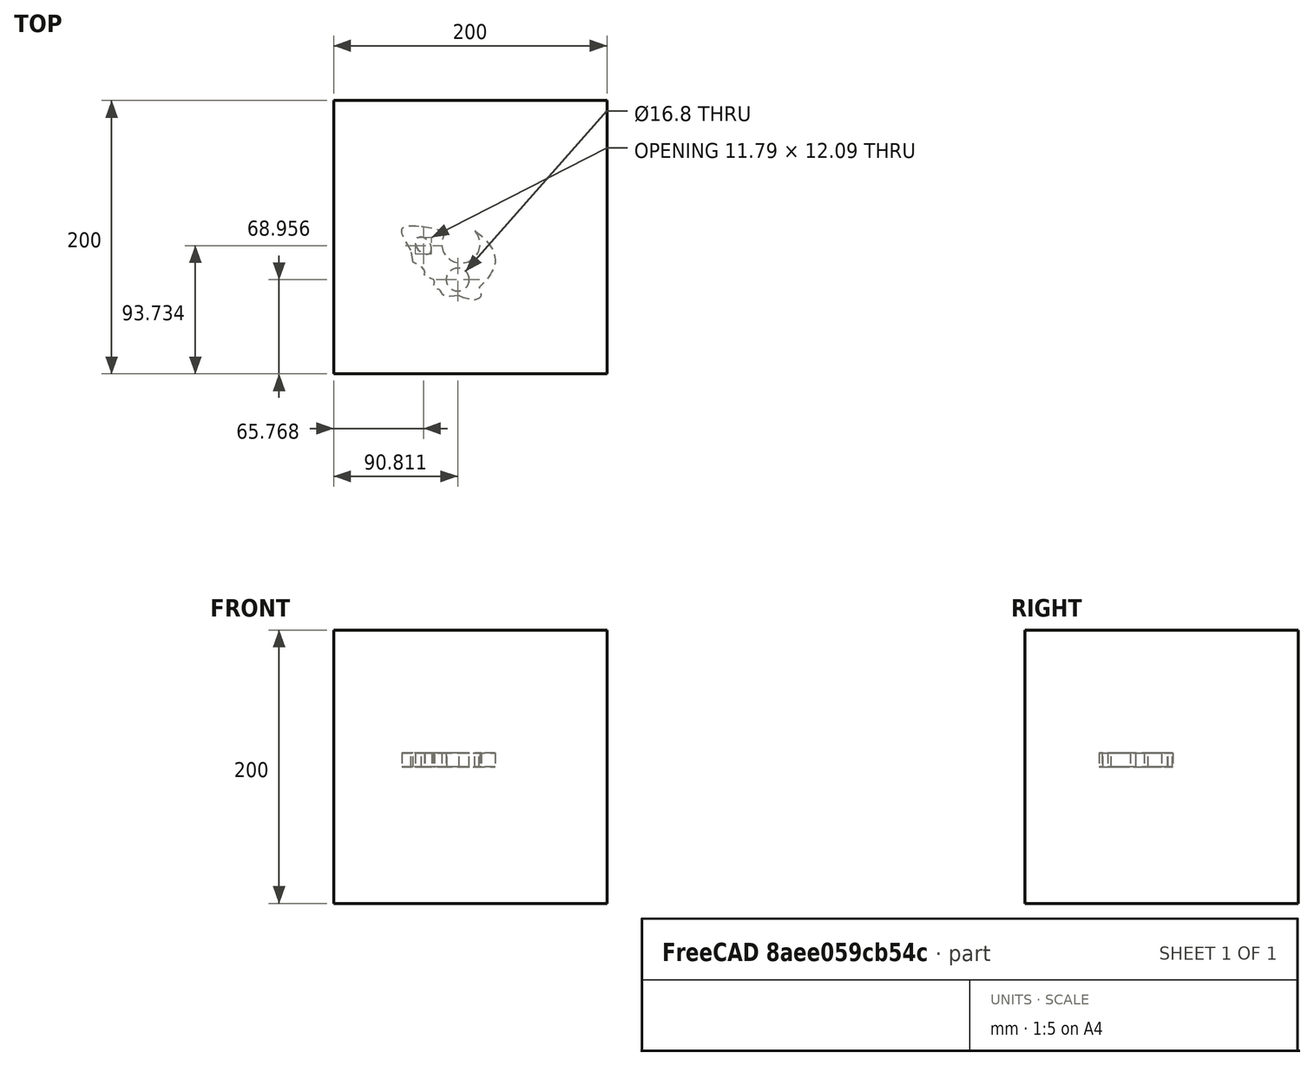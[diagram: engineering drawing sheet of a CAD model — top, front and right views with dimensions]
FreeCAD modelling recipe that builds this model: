
FCSTD DOCUMENT  (FreeCAD 0.21R33694 (Git))
Label: extrudeAllShapes
License: All rights reserved
LicenseURL: http://en.wikipedia.org/wiki/All_rights_reserved
objects: App::DocumentObjectGroupPython×1248, App::Part×2, Part::FeaturePython×1, Sketcher::SketchObject×1, Part::Extrusion×1
note: 3 computed .brp shape members not serialized (recipe doc carries the construction recipe); baked Part::Feature solids carry a one-line shape summary decoded from their .brp

FEATURE [App::DocumentObjectGroupPython] HALFPI  # scripted group (container) (typed FeaturePython)
  name = HALFPI
  value = pi/2.
FEATURE [App::DocumentObjectGroupPython] PI  # scripted group (container) (typed FeaturePython)
  name = PI
  value = 1.*pi
FEATURE [App::DocumentObjectGroupPython] TWOPI  # scripted group (container) (typed FeaturePython)
  name = TWOPI
  value = 2.*pi
FEATURE [App::DocumentObjectGroupPython] Constants  # scripted group (container) (typed FeaturePython)
  Group = -> [HALFPI,PI,TWOPI]
FEATURE [App::DocumentObjectGroupPython] Variables  # scripted group (container) (typed FeaturePython)
FEATURE [App::DocumentObjectGroupPython] Quantities  # scripted group (container) (typed FeaturePython)
FEATURE [App::DocumentObjectGroupPython] Isotopes  # scripted group (container) (typed FeaturePython)
FEATURE [App::DocumentObjectGroupPython] Elements  # scripted group (container) (typed FeaturePython)
FEATURE [App::DocumentObjectGroupPython] G4Isotopes  # scripted group (container) (typed FeaturePython)
FEATURE [App::DocumentObjectGroupPython] H_element  # scripted group (container) (typed FeaturePython)
  Z = 1
  atom_value = 1.008
  formula = H
  name = H_element
FEATURE [App::DocumentObjectGroupPython] He_element  # scripted group (container) (typed FeaturePython)
  Z = 2
  atom_value = 4.0026
  formula = He
  name = He_element
FEATURE [App::DocumentObjectGroupPython] Li_element  # scripted group (container) (typed FeaturePython)
  Z = 3
  atom_value = 6.94
  formula = Li
  name = Li_element
FEATURE [App::DocumentObjectGroupPython] Be_element  # scripted group (container) (typed FeaturePython)
  Z = 4
  atom_value = 9.01218
  formula = Be
  name = Be_element
FEATURE [App::DocumentObjectGroupPython] B_element  # scripted group (container) (typed FeaturePython)
  Z = 5
  atom_value = 10.81
  formula = B
  name = B_element
FEATURE [App::DocumentObjectGroupPython] C_element  # scripted group (container) (typed FeaturePython)
  Z = 6
  atom_value = 12.011
  formula = C
  name = C_element
FEATURE [App::DocumentObjectGroupPython] N_element  # scripted group (container) (typed FeaturePython)
  Z = 7
  atom_value = 14.007
  formula = N
  name = N_element
FEATURE [App::DocumentObjectGroupPython] O_element  # scripted group (container) (typed FeaturePython)
  Z = 8
  atom_value = 15.999
  formula = O
  name = O_element
FEATURE [App::DocumentObjectGroupPython] F_element  # scripted group (container) (typed FeaturePython)
  Z = 9
  atom_value = 18.9984
  formula = F
  name = F_element
FEATURE [App::DocumentObjectGroupPython] Ne_element  # scripted group (container) (typed FeaturePython)
  Z = 10
  atom_value = 20.1797
  formula = Ne
  name = Ne_element
FEATURE [App::DocumentObjectGroupPython] Na_element  # scripted group (container) (typed FeaturePython)
  Z = 11
  atom_value = 22.9898
  formula = Na
  name = Na_element
FEATURE [App::DocumentObjectGroupPython] Mg_element  # scripted group (container) (typed FeaturePython)
  Z = 12
  atom_value = 24.305
  formula = Mg
  name = Mg_element
FEATURE [App::DocumentObjectGroupPython] Al_element  # scripted group (container) (typed FeaturePython)
  Z = 13
  atom_value = 26.9815
  formula = Al
  name = Al_element
FEATURE [App::DocumentObjectGroupPython] Si_element  # scripted group (container) (typed FeaturePython)
  Z = 14
  atom_value = 28.085
  formula = Si
  name = Si_element
FEATURE [App::DocumentObjectGroupPython] P_element  # scripted group (container) (typed FeaturePython)
  Z = 15
  atom_value = 30.9738
  formula = P
  name = P_element
FEATURE [App::DocumentObjectGroupPython] S_element  # scripted group (container) (typed FeaturePython)
  Z = 16
  atom_value = 32.06
  formula = S
  name = S_element
FEATURE [App::DocumentObjectGroupPython] Cl_element  # scripted group (container) (typed FeaturePython)
  Z = 17
  atom_value = 35.45
  formula = Cl
  name = Cl_element
FEATURE [App::DocumentObjectGroupPython] Ar_element  # scripted group (container) (typed FeaturePython)
  Z = 18
  atom_value = 39.95
  formula = Ar
  name = Ar_element
FEATURE [App::DocumentObjectGroupPython] K_element  # scripted group (container) (typed FeaturePython)
  Z = 19
  atom_value = 39.0983
  formula = K
  name = K_element
FEATURE [App::DocumentObjectGroupPython] Ca_element  # scripted group (container) (typed FeaturePython)
  Z = 20
  atom_value = 40.078
  formula = Ca
  name = Ca_element
FEATURE [App::DocumentObjectGroupPython] Sc_element  # scripted group (container) (typed FeaturePython)
  Z = 21
  atom_value = 44.9559
  formula = Sc
  name = Sc_element
FEATURE [App::DocumentObjectGroupPython] Ti_element  # scripted group (container) (typed FeaturePython)
  Z = 22
  atom_value = 47.867
  formula = Ti
  name = Ti_element
FEATURE [App::DocumentObjectGroupPython] V_element  # scripted group (container) (typed FeaturePython)
  Z = 23
  atom_value = 50.9415
  formula = V
  name = V_element
FEATURE [App::DocumentObjectGroupPython] Cr_element  # scripted group (container) (typed FeaturePython)
  Z = 24
  atom_value = 51.9961
  formula = Cr
  name = Cr_element
FEATURE [App::DocumentObjectGroupPython] Mn_element  # scripted group (container) (typed FeaturePython)
  Z = 25
  atom_value = 54.938
  formula = Mn
  name = Mn_element
FEATURE [App::DocumentObjectGroupPython] Fe_element  # scripted group (container) (typed FeaturePython)
  Z = 26
  atom_value = 55.845
  formula = Fe
  name = Fe_element
FEATURE [App::DocumentObjectGroupPython] Co_element  # scripted group (container) (typed FeaturePython)
  Z = 27
  atom_value = 58.9332
  formula = Co
  name = Co_element
FEATURE [App::DocumentObjectGroupPython] Ni_element  # scripted group (container) (typed FeaturePython)
  Z = 28
  atom_value = 58.6934
  formula = Ni
  name = Ni_element
FEATURE [App::DocumentObjectGroupPython] Cu_element  # scripted group (container) (typed FeaturePython)
  Z = 29
  atom_value = 63.546
  formula = Cu
  name = Cu_element
FEATURE [App::DocumentObjectGroupPython] Zn_element  # scripted group (container) (typed FeaturePython)
  Z = 30
  atom_value = 65.38
  formula = Zn
  name = Zn_element
FEATURE [App::DocumentObjectGroupPython] Ga_element  # scripted group (container) (typed FeaturePython)
  Z = 31
  atom_value = 69.723
  formula = Ga
  name = Ga_element
FEATURE [App::DocumentObjectGroupPython] Ge_element  # scripted group (container) (typed FeaturePython)
  Z = 32
  atom_value = 72.63
  formula = Ge
  name = Ge_element
FEATURE [App::DocumentObjectGroupPython] As_element  # scripted group (container) (typed FeaturePython)
  Z = 33
  atom_value = 74.9216
  formula = As
  name = As_element
FEATURE [App::DocumentObjectGroupPython] Se_element  # scripted group (container) (typed FeaturePython)
  Z = 34
  atom_value = 78.971
  formula = Se
  name = Se_element
FEATURE [App::DocumentObjectGroupPython] Br_element  # scripted group (container) (typed FeaturePython)
  Z = 35
  atom_value = 79.904
  formula = Br
  name = Br_element
FEATURE [App::DocumentObjectGroupPython] Kr_element  # scripted group (container) (typed FeaturePython)
  Z = 36
  atom_value = 83.798
  formula = Kr
  name = Kr_element
FEATURE [App::DocumentObjectGroupPython] Rb_element  # scripted group (container) (typed FeaturePython)
  Z = 37
  atom_value = 85.4678
  formula = Rb
  name = Rb_element
FEATURE [App::DocumentObjectGroupPython] Sr_element  # scripted group (container) (typed FeaturePython)
  Z = 38
  atom_value = 87.62
  formula = Sr
  name = Sr_element
FEATURE [App::DocumentObjectGroupPython] Y_element  # scripted group (container) (typed FeaturePython)
  Z = 39
  atom_value = 88.9058
  formula = Y
  name = Y_element
FEATURE [App::DocumentObjectGroupPython] Zr_element  # scripted group (container) (typed FeaturePython)
  Z = 40
  atom_value = 91.224
  formula = Zr
  name = Zr_element
FEATURE [App::DocumentObjectGroupPython] Nb_element  # scripted group (container) (typed FeaturePython)
  Z = 41
  atom_value = 92.9064
  formula = Nb
  name = Nb_element
FEATURE [App::DocumentObjectGroupPython] Mo_element  # scripted group (container) (typed FeaturePython)
  Z = 42
  atom_value = 95.95
  formula = Mo
  name = Mo_element
FEATURE [App::DocumentObjectGroupPython] Tc_element  # scripted group (container) (typed FeaturePython)
  Z = 43
  atom_value = 97
  formula = Tc
  name = Tc_element
FEATURE [App::DocumentObjectGroupPython] Ru_element  # scripted group (container) (typed FeaturePython)
  Z = 44
  atom_value = 101.07
  formula = Ru
  name = Ru_element
FEATURE [App::DocumentObjectGroupPython] Rh_element  # scripted group (container) (typed FeaturePython)
  Z = 45
  atom_value = 102.905
  formula = Rh
  name = Rh_element
FEATURE [App::DocumentObjectGroupPython] Pd_element  # scripted group (container) (typed FeaturePython)
  Z = 46
  atom_value = 106.42
  formula = Pd
  name = Pd_element
FEATURE [App::DocumentObjectGroupPython] Ag_element  # scripted group (container) (typed FeaturePython)
  Z = 47
  atom_value = 107.868
  formula = Ag
  name = Ag_element
FEATURE [App::DocumentObjectGroupPython] Cd_element  # scripted group (container) (typed FeaturePython)
  Z = 48
  atom_value = 112.414
  formula = Cd
  name = Cd_element
FEATURE [App::DocumentObjectGroupPython] In_element  # scripted group (container) (typed FeaturePython)
  Z = 49
  atom_value = 114.818
  formula = In
  name = In_element
FEATURE [App::DocumentObjectGroupPython] Sn_element  # scripted group (container) (typed FeaturePython)
  Z = 50
  atom_value = 118.71
  formula = Sn
  name = Sn_element
FEATURE [App::DocumentObjectGroupPython] Sb_element  # scripted group (container) (typed FeaturePython)
  Z = 51
  atom_value = 121.76
  formula = Sb
  name = Sb_element
FEATURE [App::DocumentObjectGroupPython] Te_element  # scripted group (container) (typed FeaturePython)
  Z = 52
  atom_value = 127.6
  formula = Te
  name = Te_element
FEATURE [App::DocumentObjectGroupPython] I_element  # scripted group (container) (typed FeaturePython)
  Z = 53
  atom_value = 126.904
  formula = I
  name = I_element
FEATURE [App::DocumentObjectGroupPython] Xe_element  # scripted group (container) (typed FeaturePython)
  Z = 54
  atom_value = 131.293
  formula = Xe
  name = Xe_element
FEATURE [App::DocumentObjectGroupPython] Cs_element  # scripted group (container) (typed FeaturePython)
  Z = 55
  atom_value = 132.905
  formula = Cs
  name = Cs_element
FEATURE [App::DocumentObjectGroupPython] Ba_element  # scripted group (container) (typed FeaturePython)
  Z = 56
  atom_value = 137.327
  formula = Ba
  name = Ba_element
FEATURE [App::DocumentObjectGroupPython] La_element  # scripted group (container) (typed FeaturePython)
  Z = 57
  atom_value = 138.905
  formula = La
  name = La_element
FEATURE [App::DocumentObjectGroupPython] Ce_element  # scripted group (container) (typed FeaturePython)
  Z = 58
  atom_value = 140.116
  formula = Ce
  name = Ce_element
FEATURE [App::DocumentObjectGroupPython] Pr_element  # scripted group (container) (typed FeaturePython)
  Z = 59
  atom_value = 140.908
  formula = Pr
  name = Pr_element
FEATURE [App::DocumentObjectGroupPython] Nd_element  # scripted group (container) (typed FeaturePython)
  Z = 60
  atom_value = 144.242
  formula = Nd
  name = Nd_element
FEATURE [App::DocumentObjectGroupPython] Pm_element  # scripted group (container) (typed FeaturePython)
  Z = 61
  atom_value = 145
  formula = Pm
  name = Pm_element
FEATURE [App::DocumentObjectGroupPython] Sm_element  # scripted group (container) (typed FeaturePython)
  Z = 62
  atom_value = 150.36
  formula = Sm
  name = Sm_element
FEATURE [App::DocumentObjectGroupPython] Eu_element  # scripted group (container) (typed FeaturePython)
  Z = 63
  atom_value = 151.964
  formula = Eu
  name = Eu_element
FEATURE [App::DocumentObjectGroupPython] Gd_element  # scripted group (container) (typed FeaturePython)
  Z = 64
  atom_value = 157.25
  formula = Gd
  name = Gd_element
FEATURE [App::DocumentObjectGroupPython] Tb_element  # scripted group (container) (typed FeaturePython)
  Z = 65
  atom_value = 158.925
  formula = Tb
  name = Tb_element
FEATURE [App::DocumentObjectGroupPython] Dy_element  # scripted group (container) (typed FeaturePython)
  Z = 66
  atom_value = 162.5
  formula = Dy
  name = Dy_element
FEATURE [App::DocumentObjectGroupPython] Ho_element  # scripted group (container) (typed FeaturePython)
  Z = 67
  atom_value = 164.93
  formula = Ho
  name = Ho_element
FEATURE [App::DocumentObjectGroupPython] Er_element  # scripted group (container) (typed FeaturePython)
  Z = 68
  atom_value = 167.259
  formula = Er
  name = Er_element
FEATURE [App::DocumentObjectGroupPython] Tm_element  # scripted group (container) (typed FeaturePython)
  Z = 69
  atom_value = 168.934
  formula = Tm
  name = Tm_element
FEATURE [App::DocumentObjectGroupPython] Yb_element  # scripted group (container) (typed FeaturePython)
  Z = 70
  atom_value = 173.045
  formula = Yb
  name = Yb_element
FEATURE [App::DocumentObjectGroupPython] Lu_element  # scripted group (container) (typed FeaturePython)
  Z = 71
  atom_value = 174.967
  formula = Lu
  name = Lu_element
FEATURE [App::DocumentObjectGroupPython] Hf_element  # scripted group (container) (typed FeaturePython)
  Z = 72
  atom_value = 178.49
  formula = Hf
  name = Hf_element
FEATURE [App::DocumentObjectGroupPython] Ta_element  # scripted group (container) (typed FeaturePython)
  Z = 73
  atom_value = 180.948
  formula = Ta
  name = Ta_element
FEATURE [App::DocumentObjectGroupPython] W_element  # scripted group (container) (typed FeaturePython)
  Z = 74
  atom_value = 183.84
  formula = W
  name = W_element
FEATURE [App::DocumentObjectGroupPython] Re_element  # scripted group (container) (typed FeaturePython)
  Z = 75
  atom_value = 186.207
  formula = Re
  name = Re_element
FEATURE [App::DocumentObjectGroupPython] Os_element  # scripted group (container) (typed FeaturePython)
  Z = 76
  atom_value = 190.23
  formula = Os
  name = Os_element
FEATURE [App::DocumentObjectGroupPython] Ir_element  # scripted group (container) (typed FeaturePython)
  Z = 77
  atom_value = 192.217
  formula = Ir
  name = Ir_element
FEATURE [App::DocumentObjectGroupPython] Pt_element  # scripted group (container) (typed FeaturePython)
  Z = 78
  atom_value = 195.084
  formula = Pt
  name = Pt_element
FEATURE [App::DocumentObjectGroupPython] Au_element  # scripted group (container) (typed FeaturePython)
  Z = 79
  atom_value = 196.967
  formula = Au
  name = Au_element
FEATURE [App::DocumentObjectGroupPython] Hg_element  # scripted group (container) (typed FeaturePython)
  Z = 80
  atom_value = 200.592
  formula = Hg
  name = Hg_element
FEATURE [App::DocumentObjectGroupPython] Tl_element  # scripted group (container) (typed FeaturePython)
  Z = 81
  atom_value = 204.38
  formula = Tl
  name = Tl_element
FEATURE [App::DocumentObjectGroupPython] Pb_element  # scripted group (container) (typed FeaturePython)
  Z = 82
  atom_value = 207.2
  formula = Pb
  name = Pb_element
FEATURE [App::DocumentObjectGroupPython] Bi_element  # scripted group (container) (typed FeaturePython)
  Z = 83
  atom_value = 208.98
  formula = Bi
  name = Bi_element
FEATURE [App::DocumentObjectGroupPython] Po_element  # scripted group (container) (typed FeaturePython)
  Z = 84
  atom_value = 209
  formula = Po
  name = Po_element
FEATURE [App::DocumentObjectGroupPython] At_element  # scripted group (container) (typed FeaturePython)
  Z = 85
  atom_value = 210
  formula = At
  name = At_element
FEATURE [App::DocumentObjectGroupPython] Rn_element  # scripted group (container) (typed FeaturePython)
  Z = 86
  atom_value = 222
  formula = Rn
  name = Rn_element
FEATURE [App::DocumentObjectGroupPython] Fr_element  # scripted group (container) (typed FeaturePython)
  Z = 87
  atom_value = 223
  formula = Fr
  name = Fr_element
FEATURE [App::DocumentObjectGroupPython] Ra_element  # scripted group (container) (typed FeaturePython)
  Z = 88
  atom_value = 226
  formula = Ra
  name = Ra_element
FEATURE [App::DocumentObjectGroupPython] Ac_element  # scripted group (container) (typed FeaturePython)
  Z = 89
  atom_value = 227
  formula = Ac
  name = Ac_element
FEATURE [App::DocumentObjectGroupPython] Th_element  # scripted group (container) (typed FeaturePython)
  Z = 90
  atom_value = 232.038
  formula = Th
  name = Th_element
FEATURE [App::DocumentObjectGroupPython] Pa_element  # scripted group (container) (typed FeaturePython)
  Z = 91
  atom_value = 231.036
  formula = Pa
  name = Pa_element
FEATURE [App::DocumentObjectGroupPython] U_element  # scripted group (container) (typed FeaturePython)
  Z = 92
  atom_value = 238.029
  formula = U
  name = U_element
FEATURE [App::DocumentObjectGroupPython] Np_element  # scripted group (container) (typed FeaturePython)
  Z = 93
  atom_value = 237
  formula = Np
  name = Np_element
FEATURE [App::DocumentObjectGroupPython] Pu_element  # scripted group (container) (typed FeaturePython)
  Z = 94
  atom_value = 244
  formula = Pu
  name = Pu_element
FEATURE [App::DocumentObjectGroupPython] Am_element  # scripted group (container) (typed FeaturePython)
  Z = 95
  atom_value = 243
  formula = Am
  name = Am_element
FEATURE [App::DocumentObjectGroupPython] Cm_element  # scripted group (container) (typed FeaturePython)
  Z = 96
  atom_value = 247
  formula = Cm
  name = Cm_element
FEATURE [App::DocumentObjectGroupPython] Bk_element  # scripted group (container) (typed FeaturePython)
  Z = 97
  atom_value = 247
  formula = Bk
  name = Bk_element
FEATURE [App::DocumentObjectGroupPython] Cf_element  # scripted group (container) (typed FeaturePython)
  Z = 98
  atom_value = 251
  formula = Cf
  name = Cf_element
FEATURE [App::DocumentObjectGroupPython] G4Elements  # scripted group (container) (typed FeaturePython)
  Group = -> [H_element,He_element,Li_element,Be_element,B_element,C_element,N_element,O_element,F_element,Ne_element,Na_element,Mg_element,Al_element,Si_element,P_element,S_element,Cl_element,Ar_element,K_element,Ca_element,Sc_element,Ti_element,V_element,Cr_element,Mn_element,Fe_element,Co_element,Ni_element,Cu_element,Zn_element,Ga_element,Ge_element,As_element,Se_element,Br_element,Kr_element,Rb_element,+61 more]
FEATURE [App::DocumentObjectGroupPython] H_element001  label="H_element : 0.101"  # scripted group (container) (typed FeaturePython)
  n = 0.101327
FEATURE [App::DocumentObjectGroupPython] C_element001  label="C_element : 0.775"  # scripted group (container) (typed FeaturePython)
  n = 0.7755
FEATURE [App::DocumentObjectGroupPython] N_element001  label="N_element : 0.035"  # scripted group (container) (typed FeaturePython)
  n = 0.035057
FEATURE [App::DocumentObjectGroupPython] O_element001  label="O_element : 0.052"  # scripted group (container) (typed FeaturePython)
  n = 0.0523159
FEATURE [App::DocumentObjectGroupPython] F_element001  label="F_element : 0.017"  # scripted group (container) (typed FeaturePython)
  n = 0.017422
FEATURE [App::DocumentObjectGroupPython] Ca_element001  label="Ca_element : 0.018"  # scripted group (container) (typed FeaturePython)
  n = 0.018378
FEATURE [App::DocumentObjectGroupPython] G4_A_150_TISSUE  label="G4_A-150_TISSUE"  # scripted group (container) (typed FeaturePython)
  Dunit = g/cm3
  Dvalue = 1.127
  Group = -> [H_element001,C_element001,N_element001,O_element001,F_element001,Ca_element001]
  conduct = 2
  density = 1
  expand = 3
  formula = G4_A-150_TISSUE
  name = G4_A-150_TISSUE
  specific = 4
FEATURE [App::DocumentObjectGroupPython] C_element002  label="C_element : 3"  # scripted group (container) (typed FeaturePython)
  n = 3
  ref = C_element
FEATURE [App::DocumentObjectGroupPython] H_element002  label="H_element : 6"  # scripted group (container) (typed FeaturePython)
  n = 6
  ref = H_element
FEATURE [App::DocumentObjectGroupPython] O_element002  label="O_element : 1"  # scripted group (container) (typed FeaturePython)
  n = 1
  ref = O_element
FEATURE [App::DocumentObjectGroupPython] G4_ACETONE  # scripted group (container) (typed FeaturePython)
  Dunit = g/cm3
  Dvalue = 0.7899
  Group = -> [C_element002,H_element002,O_element002]
  conduct = 2
  density = 1
  expand = 3
  formula = G4_ACETONE
  name = G4_ACETONE
  specific = 4
FEATURE [App::DocumentObjectGroupPython] C_element003  label="C_element : 2"  # scripted group (container) (typed FeaturePython)
  n = 2
  ref = C_element
FEATURE [App::DocumentObjectGroupPython] H_element003  label="H_element : 2"  # scripted group (container) (typed FeaturePython)
  n = 2
  ref = H_element
FEATURE [App::DocumentObjectGroupPython] G4_ACETYLENE  # scripted group (container) (typed FeaturePython)
  Dunit = g/cm3
  Dvalue = 0.0010967
  Group = -> [C_element003,H_element003]
  conduct = 2
  density = 1
  expand = 3
  formula = G4_ACETYLENE
  name = G4_ACETYLENE
  specific = 4
FEATURE [App::DocumentObjectGroupPython] C_element004  label="C_element : 5"  # scripted group (container) (typed FeaturePython)
  n = 5
  ref = C_element
FEATURE [App::DocumentObjectGroupPython] H_element004  label="H_element : 5"  # scripted group (container) (typed FeaturePython)
  n = 5
  ref = H_element
FEATURE [App::DocumentObjectGroupPython] N_element002  label="N_element : 5"  # scripted group (container) (typed FeaturePython)
  n = 5
  ref = N_element
FEATURE [App::DocumentObjectGroupPython] G4_ADENINE  # scripted group (container) (typed FeaturePython)
  Dunit = g/cm3
  Dvalue = 1.6
  Group = -> [C_element004,H_element004,N_element002]
  conduct = 2
  density = 1
  expand = 3
  formula = G4_ADENINE
  name = G4_ADENINE
  specific = 4
FEATURE [App::DocumentObjectGroupPython] H_element005  label="H_element : 0.114"  # scripted group (container) (typed FeaturePython)
  n = 0.114
FEATURE [App::DocumentObjectGroupPython] C_element005  label="C_element : 0.598"  # scripted group (container) (typed FeaturePython)
  n = 0.598
FEATURE [App::DocumentObjectGroupPython] N_element003  label="N_element : 0.007"  # scripted group (container) (typed FeaturePython)
  n = 0.007
FEATURE [App::DocumentObjectGroupPython] O_element003  label="O_element : 0.278"  # scripted group (container) (typed FeaturePython)
  n = 0.278
FEATURE [App::DocumentObjectGroupPython] Na_element001  label="Na_element : 0.001"  # scripted group (container) (typed FeaturePython)
  n = 0.001
FEATURE [App::DocumentObjectGroupPython] S_element001  label="S_element : 0.001"  # scripted group (container) (typed FeaturePython)
  n = 0.001
FEATURE [App::DocumentObjectGroupPython] Cl_element001  label="Cl_element : 0.001"  # scripted group (container) (typed FeaturePython)
  n = 0.001
FEATURE [App::DocumentObjectGroupPython] G4_ADIPOSE_TISSUE_ICRP  # scripted group (container) (typed FeaturePython)
  Dunit = g/cm3
  Dvalue = 0.95
  Group = -> [H_element005,C_element005,N_element003,O_element003,Na_element001,S_element001,Cl_element001]
  conduct = 2
  density = 1
  expand = 3
  formula = G4_ADIPOSE_TISSUE_ICRP
  name = G4_ADIPOSE_TISSUE_ICRP
  specific = 4
FEATURE [App::DocumentObjectGroupPython] C_element006  label="C_element : 0.000"  # scripted group (container) (typed FeaturePython)
  n = 0.000124
FEATURE [App::DocumentObjectGroupPython] N_element004  label="N_element : 0.755"  # scripted group (container) (typed FeaturePython)
  n = 0.755268
FEATURE [App::DocumentObjectGroupPython] O_element004  label="O_element : 0.232"  # scripted group (container) (typed FeaturePython)
  n = 0.231781
FEATURE [App::DocumentObjectGroupPython] Ar_element001  label="Ar_element : 0.013"  # scripted group (container) (typed FeaturePython)
  n = 0.012827
FEATURE [App::DocumentObjectGroupPython] G4_AIR  # scripted group (container) (typed FeaturePython)
  Dunit = g/cm3
  Dvalue = 0.00120479
  Group = -> [C_element006,N_element004,O_element004,Ar_element001]
  conduct = 2
  density = 1
  expand = 3
  formula = G4_AIR
  name = G4_AIR
  specific = 4
FEATURE [App::DocumentObjectGroupPython] C_element007  label="C_element : 006"  # scripted group (container) (typed FeaturePython)
  n = 3
  ref = C_element
FEATURE [App::DocumentObjectGroupPython] H_element006  label="H_element : 7"  # scripted group (container) (typed FeaturePython)
  n = 7
  ref = H_element
FEATURE [App::DocumentObjectGroupPython] N_element005  label="N_element : 1"  # scripted group (container) (typed FeaturePython)
  n = 1
  ref = N_element
FEATURE [App::DocumentObjectGroupPython] O_element005  label="O_element : 2"  # scripted group (container) (typed FeaturePython)
  n = 2
  ref = O_element
FEATURE [App::DocumentObjectGroupPython] G4_ALANINE  # scripted group (container) (typed FeaturePython)
  Dunit = g/cm3
  Dvalue = 1.42
  Group = -> [C_element007,H_element006,N_element005,O_element005]
  conduct = 2
  density = 1
  expand = 3
  formula = G4_ALANINE
  name = G4_ALANINE
  specific = 4
FEATURE [App::DocumentObjectGroupPython] Al_element001  label="Al_element : 2"  # scripted group (container) (typed FeaturePython)
  n = 2
  ref = Al_element
FEATURE [App::DocumentObjectGroupPython] O_element006  label="O_element : 3"  # scripted group (container) (typed FeaturePython)
  n = 3
  ref = O_element
FEATURE [App::DocumentObjectGroupPython] G4_ALUMINUM_OXIDE  # scripted group (container) (typed FeaturePython)
  Dunit = g/cm3
  Dvalue = 3.97
  Group = -> [Al_element001,O_element006]
  conduct = 2
  density = 1
  expand = 3
  formula = G4_ALUMINUM_OXIDE
  name = G4_ALUMINUM_OXIDE
  specific = 4
FEATURE [App::DocumentObjectGroupPython] H_element007  label="H_element : 0.106"  # scripted group (container) (typed FeaturePython)
  n = 0.10593
FEATURE [App::DocumentObjectGroupPython] C_element008  label="C_element : 0.789"  # scripted group (container) (typed FeaturePython)
  n = 0.788974
FEATURE [App::DocumentObjectGroupPython] O_element007  label="O_element : 0.105"  # scripted group (container) (typed FeaturePython)
  n = 0.105096
FEATURE [App::DocumentObjectGroupPython] G4_AMBER  # scripted group (container) (typed FeaturePython)
  Dunit = g/cm3
  Dvalue = 1.1
  Group = -> [H_element007,C_element008,O_element007]
  conduct = 2
  density = 1
  expand = 3
  formula = G4_AMBER
  name = G4_AMBER
  specific = 4
FEATURE [App::DocumentObjectGroupPython] N_element006  label="N_element : 006"  # scripted group (container) (typed FeaturePython)
  n = 1
  ref = N_element
FEATURE [App::DocumentObjectGroupPython] H_element008  label="H_element : 3"  # scripted group (container) (typed FeaturePython)
  n = 3
  ref = H_element
FEATURE [App::DocumentObjectGroupPython] G4_AMMONIA  # scripted group (container) (typed FeaturePython)
  Dunit = g/cm3
  Dvalue = 0.000826019
  Group = -> [N_element006,H_element008]
  conduct = 2
  density = 1
  expand = 3
  formula = G4_AMMONIA
  name = G4_AMMONIA
  specific = 4
FEATURE [App::DocumentObjectGroupPython] C_element009  label="C_element : 6"  # scripted group (container) (typed FeaturePython)
  n = 6
  ref = C_element
FEATURE [App::DocumentObjectGroupPython] H_element009  label="H_element : 008"  # scripted group (container) (typed FeaturePython)
  n = 7
  ref = H_element
FEATURE [App::DocumentObjectGroupPython] N_element007  label="N_element : 007"  # scripted group (container) (typed FeaturePython)
  n = 1
  ref = N_element
FEATURE [App::DocumentObjectGroupPython] G4_ANILINE  # scripted group (container) (typed FeaturePython)
  Dunit = g/cm3
  Dvalue = 1.0235
  Group = -> [C_element009,H_element009,N_element007]
  conduct = 2
  density = 1
  expand = 3
  formula = G4_ANILINE
  name = G4_ANILINE
  specific = 4
FEATURE [App::DocumentObjectGroupPython] C_element010  label="C_element : 14"  # scripted group (container) (typed FeaturePython)
  n = 14
  ref = C_element
FEATURE [App::DocumentObjectGroupPython] H_element010  label="H_element : 10"  # scripted group (container) (typed FeaturePython)
  n = 10
  ref = H_element
FEATURE [App::DocumentObjectGroupPython] G4_ANTHRACENE  # scripted group (container) (typed FeaturePython)
  Dunit = g/cm3
  Dvalue = 1.283
  Group = -> [C_element010,H_element010]
  conduct = 2
  density = 1
  expand = 3
  formula = G4_ANTHRACENE
  name = G4_ANTHRACENE
  specific = 4
FEATURE [App::DocumentObjectGroupPython] H_element011  label="H_element : 0.065"  # scripted group (container) (typed FeaturePython)
  n = 0.0654709
FEATURE [App::DocumentObjectGroupPython] C_element011  label="C_element : 0.537"  # scripted group (container) (typed FeaturePython)
  n = 0.536944
FEATURE [App::DocumentObjectGroupPython] N_element008  label="N_element : 0.021"  # scripted group (container) (typed FeaturePython)
  n = 0.0215
FEATURE [App::DocumentObjectGroupPython] O_element008  label="O_element : 0.032"  # scripted group (container) (typed FeaturePython)
  n = 0.032085
FEATURE [App::DocumentObjectGroupPython] F_element002  label="F_element : 0.167"  # scripted group (container) (typed FeaturePython)
  n = 0.167411
FEATURE [App::DocumentObjectGroupPython] Ca_element002  label="Ca_element : 0.177"  # scripted group (container) (typed FeaturePython)
  n = 0.176589
FEATURE [App::DocumentObjectGroupPython] G4_B_100_BONE  label="G4_B-100_BONE"  # scripted group (container) (typed FeaturePython)
  Dunit = g/cm3
  Dvalue = 1.45
  Group = -> [H_element011,C_element011,N_element008,O_element008,F_element002,Ca_element002]
  conduct = 2
  density = 1
  expand = 3
  formula = G4_B-100_BONE
  name = G4_B-100_BONE
  specific = 4
FEATURE [App::DocumentObjectGroupPython] H_element012  label="H_element : 0.057"  # scripted group (container) (typed FeaturePython)
  n = 0.057441
FEATURE [App::DocumentObjectGroupPython] C_element012  label="C_element : 0.790"  # scripted group (container) (typed FeaturePython)
  n = 0.774591
FEATURE [App::DocumentObjectGroupPython] O_element009  label="O_element : 0.168"  # scripted group (container) (typed FeaturePython)
  n = 0.167968
FEATURE [App::DocumentObjectGroupPython] G4_BAKELITE  # scripted group (container) (typed FeaturePython)
  Dunit = g/cm3
  Dvalue = 1.25
  Group = -> [H_element012,C_element012,O_element009]
  conduct = 2
  density = 1
  expand = 3
  formula = G4_BAKELITE
  name = G4_BAKELITE
  specific = 4
FEATURE [App::DocumentObjectGroupPython] Ba_element001  label="Ba_element : 1"  # scripted group (container) (typed FeaturePython)
  n = 1
  ref = Ba_element
FEATURE [App::DocumentObjectGroupPython] F_element003  label="F_element : 2"  # scripted group (container) (typed FeaturePython)
  n = 2
  ref = F_element
FEATURE [App::DocumentObjectGroupPython] G4_BARIUM_FLUORIDE  # scripted group (container) (typed FeaturePython)
  Dunit = g/cm3
  Dvalue = 4.89
  Group = -> [Ba_element001,F_element003]
  conduct = 2
  density = 1
  expand = 3
  formula = G4_BARIUM_FLUORIDE
  name = G4_BARIUM_FLUORIDE
  specific = 4
FEATURE [App::DocumentObjectGroupPython] Ba_element002  label="Ba_element : 002"  # scripted group (container) (typed FeaturePython)
  n = 1
  ref = Ba_element
FEATURE [App::DocumentObjectGroupPython] S_element002  label="S_element : 1"  # scripted group (container) (typed FeaturePython)
  n = 1
  ref = S_element
FEATURE [App::DocumentObjectGroupPython] O_element010  label="O_element : 4"  # scripted group (container) (typed FeaturePython)
  n = 4
  ref = O_element
FEATURE [App::DocumentObjectGroupPython] G4_BARIUM_SULFATE  # scripted group (container) (typed FeaturePython)
  Dunit = g/cm3
  Dvalue = 4.5
  Group = -> [Ba_element002,S_element002,O_element010]
  conduct = 2
  density = 1
  expand = 3
  formula = G4_BARIUM_SULFATE
  name = G4_BARIUM_SULFATE
  specific = 4
FEATURE [App::DocumentObjectGroupPython] C_element013  label="C_element : 007"  # scripted group (container) (typed FeaturePython)
  n = 6
  ref = C_element
FEATURE [App::DocumentObjectGroupPython] H_element013  label="H_element : 009"  # scripted group (container) (typed FeaturePython)
  n = 6
  ref = H_element
FEATURE [App::DocumentObjectGroupPython] G4_BENZENE  # scripted group (container) (typed FeaturePython)
  Dunit = g/cm3
  Dvalue = 0.87865
  Group = -> [C_element013,H_element013]
  conduct = 2
  density = 1
  expand = 3
  formula = G4_BENZENE
  name = G4_BENZENE
  specific = 4
FEATURE [App::DocumentObjectGroupPython] Be_element001  label="Be_element : 1"  # scripted group (container) (typed FeaturePython)
  n = 1
  ref = Be_element
FEATURE [App::DocumentObjectGroupPython] O_element011  label="O_element : 005"  # scripted group (container) (typed FeaturePython)
  n = 1
  ref = O_element
FEATURE [App::DocumentObjectGroupPython] G4_BERYLLIUM_OXIDE  # scripted group (container) (typed FeaturePython)
  Dunit = g/cm3
  Dvalue = 3.01
  Group = -> [Be_element001,O_element011]
  conduct = 2
  density = 1
  expand = 3
  formula = G4_BERYLLIUM_OXIDE
  name = G4_BERYLLIUM_OXIDE
  specific = 4
FEATURE [App::DocumentObjectGroupPython] Bi_element001  label="Bi_element : 4"  # scripted group (container) (typed FeaturePython)
  n = 4
  ref = Bi_element
FEATURE [App::DocumentObjectGroupPython] Ge_element001  label="Ge_element : 3"  # scripted group (container) (typed FeaturePython)
  n = 3
  ref = Ge_element
FEATURE [App::DocumentObjectGroupPython] O_element012  label="O_element : 12"  # scripted group (container) (typed FeaturePython)
  n = 12
  ref = O_element
FEATURE [App::DocumentObjectGroupPython] G4_BGO  # scripted group (container) (typed FeaturePython)
  Dunit = g/cm3
  Dvalue = 7.13
  Group = -> [Bi_element001,Ge_element001,O_element012]
  conduct = 2
  density = 1
  expand = 3
  formula = G4_BGO
  name = G4_BGO
  specific = 4
FEATURE [App::DocumentObjectGroupPython] H_element014  label="H_element : 0.102"  # scripted group (container) (typed FeaturePython)
  n = 0.102
FEATURE [App::DocumentObjectGroupPython] C_element014  label="C_element : 0.110"  # scripted group (container) (typed FeaturePython)
  n = 0.11
FEATURE [App::DocumentObjectGroupPython] N_element009  label="N_element : 0.033"  # scripted group (container) (typed FeaturePython)
  n = 0.033
FEATURE [App::DocumentObjectGroupPython] O_element013  label="O_element : 0.745"  # scripted group (container) (typed FeaturePython)
  n = 0.745
FEATURE [App::DocumentObjectGroupPython] Na_element002  label="Na_element : 0.002"  # scripted group (container) (typed FeaturePython)
  n = 0.001
FEATURE [App::DocumentObjectGroupPython] P_element001  label="P_element : 0.001"  # scripted group (container) (typed FeaturePython)
  n = 0.001
FEATURE [App::DocumentObjectGroupPython] S_element003  label="S_element : 0.002"  # scripted group (container) (typed FeaturePython)
  n = 0.002
FEATURE [App::DocumentObjectGroupPython] Cl_element002  label="Cl_element : 0.003"  # scripted group (container) (typed FeaturePython)
  n = 0.003
FEATURE [App::DocumentObjectGroupPython] K_element001  label="K_element : 0.002"  # scripted group (container) (typed FeaturePython)
  n = 0.002
FEATURE [App::DocumentObjectGroupPython] Fe_element001  label="Fe_element : 0.001"  # scripted group (container) (typed FeaturePython)
  n = 0.001
FEATURE [App::DocumentObjectGroupPython] G4_BLOOD_ICRP  # scripted group (container) (typed FeaturePython)
  Dunit = g/cm3
  Dvalue = 1.06
  Group = -> [H_element014,C_element014,N_element009,O_element013,Na_element002,P_element001,S_element003,Cl_element002,K_element001,Fe_element001]
  conduct = 2
  density = 1
  expand = 3
  formula = G4_BLOOD_ICRP
  name = G4_BLOOD_ICRP
  specific = 4
FEATURE [App::DocumentObjectGroupPython] H_element015  label="H_element : 0.064"  # scripted group (container) (typed FeaturePython)
  n = 0.064
FEATURE [App::DocumentObjectGroupPython] C_element015  label="C_element : 0.278"  # scripted group (container) (typed FeaturePython)
  n = 0.278
FEATURE [App::DocumentObjectGroupPython] N_element010  label="N_element : 0.027"  # scripted group (container) (typed FeaturePython)
  n = 0.027
FEATURE [App::DocumentObjectGroupPython] O_element014  label="O_element : 0.410"  # scripted group (container) (typed FeaturePython)
  n = 0.41
FEATURE [App::DocumentObjectGroupPython] Mg_element001  label="Mg_element : 0.002"  # scripted group (container) (typed FeaturePython)
  n = 0.002
FEATURE [App::DocumentObjectGroupPython] P_element002  label="P_element : 0.070"  # scripted group (container) (typed FeaturePython)
  n = 0.07
FEATURE [App::DocumentObjectGroupPython] S_element004  label="S_element : 0.003"  # scripted group (container) (typed FeaturePython)
  n = 0.002
FEATURE [App::DocumentObjectGroupPython] Ca_element003  label="Ca_element : 0.147"  # scripted group (container) (typed FeaturePython)
  n = 0.147
FEATURE [App::DocumentObjectGroupPython] G4_BONE_COMPACT_ICRU  # scripted group (container) (typed FeaturePython)
  Dunit = g/cm3
  Dvalue = 1.85
  Group = -> [H_element015,C_element015,N_element010,O_element014,Mg_element001,P_element002,S_element004,Ca_element003]
  conduct = 2
  density = 1
  expand = 3
  formula = G4_BONE_COMPACT_ICRU
  name = G4_BONE_COMPACT_ICRU
  specific = 4
FEATURE [App::DocumentObjectGroupPython] H_element016  label="H_element : 0.034"  # scripted group (container) (typed FeaturePython)
  n = 0.034
FEATURE [App::DocumentObjectGroupPython] C_element016  label="C_element : 0.155"  # scripted group (container) (typed FeaturePython)
  n = 0.155
FEATURE [App::DocumentObjectGroupPython] N_element011  label="N_element : 0.042"  # scripted group (container) (typed FeaturePython)
  n = 0.042
FEATURE [App::DocumentObjectGroupPython] O_element015  label="O_element : 0.435"  # scripted group (container) (typed FeaturePython)
  n = 0.435
FEATURE [App::DocumentObjectGroupPython] Na_element003  label="Na_element : 0.003"  # scripted group (container) (typed FeaturePython)
  n = 0.001
FEATURE [App::DocumentObjectGroupPython] Mg_element002  label="Mg_element : 0.003"  # scripted group (container) (typed FeaturePython)
  n = 0.002
FEATURE [App::DocumentObjectGroupPython] P_element003  label="P_element : 0.103"  # scripted group (container) (typed FeaturePython)
  n = 0.103
FEATURE [App::DocumentObjectGroupPython] S_element005  label="S_element : 0.004"  # scripted group (container) (typed FeaturePython)
  n = 0.003
FEATURE [App::DocumentObjectGroupPython] Ca_element004  label="Ca_element : 0.225"  # scripted group (container) (typed FeaturePython)
  n = 0.225
FEATURE [App::DocumentObjectGroupPython] G4_BONE_CORTICAL_ICRP  # scripted group (container) (typed FeaturePython)
  Dunit = g/cm3
  Dvalue = 1.92
  Group = -> [H_element016,C_element016,N_element011,O_element015,Na_element003,Mg_element002,P_element003,S_element005,Ca_element004]
  conduct = 2
  density = 1
  expand = 3
  formula = G4_BONE_CORTICAL_ICRP
  name = G4_BONE_CORTICAL_ICRP
  specific = 4
FEATURE [App::DocumentObjectGroupPython] B_element001  label="B_element : 4"  # scripted group (container) (typed FeaturePython)
  n = 4
  ref = B_element
FEATURE [App::DocumentObjectGroupPython] C_element017  label="C_element : 1"  # scripted group (container) (typed FeaturePython)
  n = 1
  ref = C_element
FEATURE [App::DocumentObjectGroupPython] G4_BORON_CARBIDE  # scripted group (container) (typed FeaturePython)
  Dunit = g/cm3
  Dvalue = 2.52
  Group = -> [B_element001,C_element017]
  conduct = 2
  density = 1
  expand = 3
  formula = G4_BORON_CARBIDE
  name = G4_BORON_CARBIDE
  specific = 4
FEATURE [App::DocumentObjectGroupPython] B_element002  label="B_element : 2"  # scripted group (container) (typed FeaturePython)
  n = 2
  ref = B_element
FEATURE [App::DocumentObjectGroupPython] O_element016  label="O_element : 006"  # scripted group (container) (typed FeaturePython)
  n = 3
  ref = O_element
FEATURE [App::DocumentObjectGroupPython] G4_BORON_OXIDE  # scripted group (container) (typed FeaturePython)
  Dunit = g/cm3
  Dvalue = 1.812
  Group = -> [B_element002,O_element016]
  conduct = 2
  density = 1
  expand = 3
  formula = G4_BORON_OXIDE
  name = G4_BORON_OXIDE
  specific = 4
FEATURE [App::DocumentObjectGroupPython] H_element017  label="H_element : 0.107"  # scripted group (container) (typed FeaturePython)
  n = 0.107
FEATURE [App::DocumentObjectGroupPython] C_element018  label="C_element : 0.145"  # scripted group (container) (typed FeaturePython)
  n = 0.145
FEATURE [App::DocumentObjectGroupPython] N_element012  label="N_element : 0.022"  # scripted group (container) (typed FeaturePython)
  n = 0.022
FEATURE [App::DocumentObjectGroupPython] O_element017  label="O_element : 0.712"  # scripted group (container) (typed FeaturePython)
  n = 0.712
FEATURE [App::DocumentObjectGroupPython] Na_element004  label="Na_element : 0.004"  # scripted group (container) (typed FeaturePython)
  n = 0.002
FEATURE [App::DocumentObjectGroupPython] P_element004  label="P_element : 0.004"  # scripted group (container) (typed FeaturePython)
  n = 0.004
FEATURE [App::DocumentObjectGroupPython] S_element006  label="S_element : 0.005"  # scripted group (container) (typed FeaturePython)
  n = 0.002
FEATURE [App::DocumentObjectGroupPython] Cl_element003  label="Cl_element : 0.004"  # scripted group (container) (typed FeaturePython)
  n = 0.003
FEATURE [App::DocumentObjectGroupPython] K_element002  label="K_element : 0.003"  # scripted group (container) (typed FeaturePython)
  n = 0.003
FEATURE [App::DocumentObjectGroupPython] G4_BRAIN_ICRP  # scripted group (container) (typed FeaturePython)
  Dunit = g/cm3
  Dvalue = 1.04
  Group = -> [H_element017,C_element018,N_element012,O_element017,Na_element004,P_element004,S_element006,Cl_element003,K_element002]
  conduct = 2
  density = 1
  expand = 3
  formula = G4_BRAIN_ICRP
  name = G4_BRAIN_ICRP
  specific = 4
FEATURE [App::DocumentObjectGroupPython] C_element019  label="C_element : 4"  # scripted group (container) (typed FeaturePython)
  n = 4
  ref = C_element
FEATURE [App::DocumentObjectGroupPython] H_element018  label="H_element : 010"  # scripted group (container) (typed FeaturePython)
  n = 10
  ref = H_element
FEATURE [App::DocumentObjectGroupPython] G4_BUTANE  # scripted group (container) (typed FeaturePython)
  Dunit = g/cm3
  Dvalue = 0.00249343
  Group = -> [C_element019,H_element018]
  conduct = 2
  density = 1
  expand = 3
  formula = G4_BUTANE
  name = G4_BUTANE
  specific = 4
FEATURE [App::DocumentObjectGroupPython] C_element020  label="C_element : 008"  # scripted group (container) (typed FeaturePython)
  n = 4
  ref = C_element
FEATURE [App::DocumentObjectGroupPython] H_element019  label="H_element : 011"  # scripted group (container) (typed FeaturePython)
  n = 10
  ref = H_element
FEATURE [App::DocumentObjectGroupPython] O_element018  label="O_element : 007"  # scripted group (container) (typed FeaturePython)
  n = 1
  ref = O_element
FEATURE [App::DocumentObjectGroupPython] G4_N_BUTYL_ALCOHOL  label="G4_N-BUTYL_ALCOHOL"  # scripted group (container) (typed FeaturePython)
  Dunit = g/cm3
  Dvalue = 0.8098
  Group = -> [C_element020,H_element019,O_element018]
  conduct = 2
  density = 1
  expand = 3
  formula = G4_N-BUTYL_ALCOHOL
  name = G4_N-BUTYL_ALCOHOL
  specific = 4
FEATURE [App::DocumentObjectGroupPython] H_element020  label="H_element : 0.025"  # scripted group (container) (typed FeaturePython)
  n = 0.02468
FEATURE [App::DocumentObjectGroupPython] C_element021  label="C_element : 0.502"  # scripted group (container) (typed FeaturePython)
  n = 0.501611
FEATURE [App::DocumentObjectGroupPython] O_element019  label="O_element : 0.005"  # scripted group (container) (typed FeaturePython)
  n = 0.004527
FEATURE [App::DocumentObjectGroupPython] F_element004  label="F_element : 0.465"  # scripted group (container) (typed FeaturePython)
  n = 0.465209
FEATURE [App::DocumentObjectGroupPython] Si_element001  label="Si_element : 0.004"  # scripted group (container) (typed FeaturePython)
  n = 0.003973
FEATURE [App::DocumentObjectGroupPython] G4_C_552  label="G4_C-552"  # scripted group (container) (typed FeaturePython)
  Dunit = g/cm3
  Dvalue = 1.76
  Group = -> [H_element020,C_element021,O_element019,F_element004,Si_element001]
  conduct = 2
  density = 1
  expand = 3
  formula = G4_C-552
  name = G4_C-552
  specific = 4
FEATURE [App::DocumentObjectGroupPython] Cd_element001  label="Cd_element : 1"  # scripted group (container) (typed FeaturePython)
  n = 1
  ref = Cd_element
FEATURE [App::DocumentObjectGroupPython] Te_element001  label="Te_element : 1"  # scripted group (container) (typed FeaturePython)
  n = 1
  ref = Te_element
FEATURE [App::DocumentObjectGroupPython] G4_CADMIUM_TELLURIDE  # scripted group (container) (typed FeaturePython)
  Dunit = g/cm3
  Dvalue = 6.2
  Group = -> [Cd_element001,Te_element001]
  conduct = 2
  density = 1
  expand = 3
  formula = G4_CADMIUM_TELLURIDE
  name = G4_CADMIUM_TELLURIDE
  specific = 4
FEATURE [App::DocumentObjectGroupPython] Cd_element002  label="Cd_element : 002"  # scripted group (container) (typed FeaturePython)
  n = 1
  ref = Cd_element
FEATURE [App::DocumentObjectGroupPython] W_element001  label="W_element : 1"  # scripted group (container) (typed FeaturePython)
  n = 1
  ref = W_element
FEATURE [App::DocumentObjectGroupPython] O_element020  label="O_element : 008"  # scripted group (container) (typed FeaturePython)
  n = 4
  ref = O_element
FEATURE [App::DocumentObjectGroupPython] G4_CADMIUM_TUNGSTATE  # scripted group (container) (typed FeaturePython)
  Dunit = g/cm3
  Dvalue = 7.9
  Group = -> [Cd_element002,W_element001,O_element020]
  conduct = 2
  density = 1
  expand = 3
  formula = G4_CADMIUM_TUNGSTATE
  name = G4_CADMIUM_TUNGSTATE
  specific = 4
FEATURE [App::DocumentObjectGroupPython] Ca_element005  label="Ca_element : 1"  # scripted group (container) (typed FeaturePython)
  n = 1
  ref = Ca_element
FEATURE [App::DocumentObjectGroupPython] C_element022  label="C_element : 009"  # scripted group (container) (typed FeaturePython)
  n = 1
  ref = C_element
FEATURE [App::DocumentObjectGroupPython] O_element021  label="O_element : 009"  # scripted group (container) (typed FeaturePython)
  n = 3
  ref = O_element
FEATURE [App::DocumentObjectGroupPython] G4_CALCIUM_CARBONATE  # scripted group (container) (typed FeaturePython)
  Dunit = g/cm3
  Dvalue = 2.8
  Group = -> [Ca_element005,C_element022,O_element021]
  conduct = 2
  density = 1
  expand = 3
  formula = G4_CALCIUM_CARBONATE
  name = G4_CALCIUM_CARBONATE
  specific = 4
FEATURE [App::DocumentObjectGroupPython] Ca_element006  label="Ca_element : 002"  # scripted group (container) (typed FeaturePython)
  n = 1
  ref = Ca_element
FEATURE [App::DocumentObjectGroupPython] F_element005  label="F_element : 003"  # scripted group (container) (typed FeaturePython)
  n = 2
  ref = F_element
FEATURE [App::DocumentObjectGroupPython] G4_CALCIUM_FLUORIDE  # scripted group (container) (typed FeaturePython)
  Dunit = g/cm3
  Dvalue = 3.18
  Group = -> [Ca_element006,F_element005]
  conduct = 2
  density = 1
  expand = 3
  formula = G4_CALCIUM_FLUORIDE
  name = G4_CALCIUM_FLUORIDE
  specific = 4
FEATURE [App::DocumentObjectGroupPython] Ca_element007  label="Ca_element : 003"  # scripted group (container) (typed FeaturePython)
  n = 1
  ref = Ca_element
FEATURE [App::DocumentObjectGroupPython] O_element022  label="O_element : 010"  # scripted group (container) (typed FeaturePython)
  n = 1
  ref = O_element
FEATURE [App::DocumentObjectGroupPython] G4_CALCIUM_OXIDE  # scripted group (container) (typed FeaturePython)
  Dunit = g/cm3
  Dvalue = 3.3
  Group = -> [Ca_element007,O_element022]
  conduct = 2
  density = 1
  expand = 3
  formula = G4_CALCIUM_OXIDE
  name = G4_CALCIUM_OXIDE
  specific = 4
FEATURE [App::DocumentObjectGroupPython] Ca_element008  label="Ca_element : 004"  # scripted group (container) (typed FeaturePython)
  n = 1
  ref = Ca_element
FEATURE [App::DocumentObjectGroupPython] S_element007  label="S_element : 002"  # scripted group (container) (typed FeaturePython)
  n = 1
  ref = S_element
FEATURE [App::DocumentObjectGroupPython] O_element023  label="O_element : 011"  # scripted group (container) (typed FeaturePython)
  n = 4
  ref = O_element
FEATURE [App::DocumentObjectGroupPython] G4_CALCIUM_SULFATE  # scripted group (container) (typed FeaturePython)
  Dunit = g/cm3
  Dvalue = 2.96
  Group = -> [Ca_element008,S_element007,O_element023]
  conduct = 2
  density = 1
  expand = 3
  formula = G4_CALCIUM_SULFATE
  name = G4_CALCIUM_SULFATE
  specific = 4
FEATURE [App::DocumentObjectGroupPython] Ca_element009  label="Ca_element : 005"  # scripted group (container) (typed FeaturePython)
  n = 1
  ref = Ca_element
FEATURE [App::DocumentObjectGroupPython] W_element002  label="W_element : 002"  # scripted group (container) (typed FeaturePython)
  n = 1
  ref = W_element
FEATURE [App::DocumentObjectGroupPython] O_element024  label="O_element : 012"  # scripted group (container) (typed FeaturePython)
  n = 4
  ref = O_element
FEATURE [App::DocumentObjectGroupPython] G4_CALCIUM_TUNGSTATE  # scripted group (container) (typed FeaturePython)
  Dunit = g/cm3
  Dvalue = 6.062
  Group = -> [Ca_element009,W_element002,O_element024]
  conduct = 2
  density = 1
  expand = 3
  formula = G4_CALCIUM_TUNGSTATE
  name = G4_CALCIUM_TUNGSTATE
  specific = 4
FEATURE [App::DocumentObjectGroupPython] C_element023  label="C_element : 010"  # scripted group (container) (typed FeaturePython)
  n = 1
  ref = C_element
FEATURE [App::DocumentObjectGroupPython] O_element025  label="O_element : 013"  # scripted group (container) (typed FeaturePython)
  n = 2
  ref = O_element
FEATURE [App::DocumentObjectGroupPython] G4_CARBON_DIOXIDE  # scripted group (container) (typed FeaturePython)
  Dunit = g/cm3
  Dvalue = 0.00184212
  Group = -> [C_element023,O_element025]
  conduct = 2
  density = 1
  expand = 3
  formula = G4_CARBON_DIOXIDE
  name = G4_CARBON_DIOXIDE
  specific = 4
FEATURE [App::DocumentObjectGroupPython] C_element024  label="C_element : 011"  # scripted group (container) (typed FeaturePython)
  n = 1
  ref = C_element
FEATURE [App::DocumentObjectGroupPython] Cl_element004  label="Cl_element : 4"  # scripted group (container) (typed FeaturePython)
  n = 4
  ref = Cl_element
FEATURE [App::DocumentObjectGroupPython] G4_CARBON_TETRACHLORIDE  # scripted group (container) (typed FeaturePython)
  Dunit = g/cm3
  Dvalue = 1.594
  Group = -> [C_element024,Cl_element004]
  conduct = 2
  density = 1
  expand = 3
  formula = G4_CARBON_TETRACHLORIDE
  name = G4_CARBON_TETRACHLORIDE
  specific = 4
FEATURE [App::DocumentObjectGroupPython] C_element025  label="C_element : 012"  # scripted group (container) (typed FeaturePython)
  n = 6
  ref = C_element
FEATURE [App::DocumentObjectGroupPython] H_element021  label="H_element : 012"  # scripted group (container) (typed FeaturePython)
  n = 10
  ref = H_element
FEATURE [App::DocumentObjectGroupPython] O_element026  label="O_element : 5"  # scripted group (container) (typed FeaturePython)
  n = 5
  ref = O_element
FEATURE [App::DocumentObjectGroupPython] G4_CELLULOSE_CELLOPHANE  # scripted group (container) (typed FeaturePython)
  Dunit = g/cm3
  Dvalue = 1.42
  Group = -> [C_element025,H_element021,O_element026]
  conduct = 2
  density = 1
  expand = 3
  formula = G4_CELLULOSE_CELLOPHANE
  name = G4_CELLULOSE_CELLOPHANE
  specific = 4
FEATURE [App::DocumentObjectGroupPython] H_element022  label="H_element : 0.067"  # scripted group (container) (typed FeaturePython)
  n = 0.067125
FEATURE [App::DocumentObjectGroupPython] C_element026  label="C_element : 0.545"  # scripted group (container) (typed FeaturePython)
  n = 0.545403
FEATURE [App::DocumentObjectGroupPython] O_element027  label="O_element : 0.387"  # scripted group (container) (typed FeaturePython)
  n = 0.387472
FEATURE [App::DocumentObjectGroupPython] G4_CELLULOSE_BUTYRATE  # scripted group (container) (typed FeaturePython)
  Dunit = g/cm3
  Dvalue = 1.2
  Group = -> [H_element022,C_element026,O_element027]
  conduct = 2
  density = 1
  expand = 3
  formula = G4_CELLULOSE_BUTYRATE
  name = G4_CELLULOSE_BUTYRATE
  specific = 4
FEATURE [App::DocumentObjectGroupPython] H_element023  label="H_element : 0.029"  # scripted group (container) (typed FeaturePython)
  n = 0.029216
FEATURE [App::DocumentObjectGroupPython] C_element027  label="C_element : 0.271"  # scripted group (container) (typed FeaturePython)
  n = 0.271296
FEATURE [App::DocumentObjectGroupPython] N_element013  label="N_element : 0.121"  # scripted group (container) (typed FeaturePython)
  n = 0.121276
FEATURE [App::DocumentObjectGroupPython] O_element028  label="O_element : 0.578"  # scripted group (container) (typed FeaturePython)
  n = 0.578212
FEATURE [App::DocumentObjectGroupPython] G4_CELLULOSE_NITRATE  # scripted group (container) (typed FeaturePython)
  Dunit = g/cm3
  Dvalue = 1.49
  Group = -> [H_element023,C_element027,N_element013,O_element028]
  conduct = 2
  density = 1
  expand = 3
  formula = G4_CELLULOSE_NITRATE
  name = G4_CELLULOSE_NITRATE
  specific = 4
FEATURE [App::DocumentObjectGroupPython] H_element024  label="H_element : 0.108"  # scripted group (container) (typed FeaturePython)
  n = 0.107596
FEATURE [App::DocumentObjectGroupPython] N_element014  label="N_element : 0.001"  # scripted group (container) (typed FeaturePython)
  n = 0.0008
FEATURE [App::DocumentObjectGroupPython] O_element029  label="O_element : 0.875"  # scripted group (container) (typed FeaturePython)
  n = 0.874976
FEATURE [App::DocumentObjectGroupPython] S_element008  label="S_element : 0.015"  # scripted group (container) (typed FeaturePython)
  n = 0.014627
FEATURE [App::DocumentObjectGroupPython] Ce_element001  label="Ce_element : 0.002"  # scripted group (container) (typed FeaturePython)
  n = 0.002001
FEATURE [App::DocumentObjectGroupPython] G4_CERIC_SULFATE  # scripted group (container) (typed FeaturePython)
  Dunit = g/cm3
  Dvalue = 1.03
  Group = -> [H_element024,N_element014,O_element029,S_element008,Ce_element001]
  conduct = 2
  density = 1
  expand = 3
  formula = G4_CERIC_SULFATE
  name = G4_CERIC_SULFATE
  specific = 4
FEATURE [App::DocumentObjectGroupPython] Cs_element001  label="Cs_element : 1"  # scripted group (container) (typed FeaturePython)
  n = 1
  ref = Cs_element
FEATURE [App::DocumentObjectGroupPython] F_element006  label="F_element : 1"  # scripted group (container) (typed FeaturePython)
  n = 1
  ref = F_element
FEATURE [App::DocumentObjectGroupPython] G4_CESIUM_FLUORIDE  # scripted group (container) (typed FeaturePython)
  Dunit = g/cm3
  Dvalue = 4.115
  Group = -> [Cs_element001,F_element006]
  conduct = 2
  density = 1
  expand = 3
  formula = G4_CESIUM_FLUORIDE
  name = G4_CESIUM_FLUORIDE
  specific = 4
FEATURE [App::DocumentObjectGroupPython] Cs_element002  label="Cs_element : 002"  # scripted group (container) (typed FeaturePython)
  n = 1
  ref = Cs_element
FEATURE [App::DocumentObjectGroupPython] I_element001  label="I_element : 1"  # scripted group (container) (typed FeaturePython)
  n = 1
  ref = I_element
FEATURE [App::DocumentObjectGroupPython] G4_CESIUM_IODIDE  # scripted group (container) (typed FeaturePython)
  Dunit = g/cm3
  Dvalue = 4.51
  Group = -> [Cs_element002,I_element001]
  conduct = 2
  density = 1
  expand = 3
  formula = G4_CESIUM_IODIDE
  name = G4_CESIUM_IODIDE
  specific = 4
FEATURE [App::DocumentObjectGroupPython] C_element028  label="C_element : 013"  # scripted group (container) (typed FeaturePython)
  n = 6
  ref = C_element
FEATURE [App::DocumentObjectGroupPython] H_element025  label="H_element : 013"  # scripted group (container) (typed FeaturePython)
  n = 5
  ref = H_element
FEATURE [App::DocumentObjectGroupPython] Cl_element005  label="Cl_element : 1"  # scripted group (container) (typed FeaturePython)
  n = 1
  ref = Cl_element
FEATURE [App::DocumentObjectGroupPython] G4_CHLOROBENZENE  # scripted group (container) (typed FeaturePython)
  Dunit = g/cm3
  Dvalue = 1.1058
  Group = -> [C_element028,H_element025,Cl_element005]
  conduct = 2
  density = 1
  expand = 3
  formula = G4_CHLOROBENZENE
  name = G4_CHLOROBENZENE
  specific = 4
FEATURE [App::DocumentObjectGroupPython] C_element029  label="C_element : 014"  # scripted group (container) (typed FeaturePython)
  n = 1
  ref = C_element
FEATURE [App::DocumentObjectGroupPython] H_element026  label="H_element : 1"  # scripted group (container) (typed FeaturePython)
  n = 1
  ref = H_element
FEATURE [App::DocumentObjectGroupPython] Cl_element006  label="Cl_element : 3"  # scripted group (container) (typed FeaturePython)
  n = 3
  ref = Cl_element
FEATURE [App::DocumentObjectGroupPython] G4_CHLOROFORM  # scripted group (container) (typed FeaturePython)
  Dunit = g/cm3
  Dvalue = 1.4832
  Group = -> [C_element029,H_element026,Cl_element006]
  conduct = 2
  density = 1
  expand = 3
  formula = G4_CHLOROFORM
  name = G4_CHLOROFORM
  specific = 4
FEATURE [App::DocumentObjectGroupPython] H_element027  label="H_element : 0.010"  # scripted group (container) (typed FeaturePython)
  n = 0.01
FEATURE [App::DocumentObjectGroupPython] C_element030  label="C_element : 0.001"  # scripted group (container) (typed FeaturePython)
  n = 0.001
FEATURE [App::DocumentObjectGroupPython] O_element030  label="O_element : 0.529"  # scripted group (container) (typed FeaturePython)
  n = 0.529107
FEATURE [App::DocumentObjectGroupPython] Na_element005  label="Na_element : 0.016"  # scripted group (container) (typed FeaturePython)
  n = 0.016
FEATURE [App::DocumentObjectGroupPython] Mg_element003  label="Mg_element : 0.004"  # scripted group (container) (typed FeaturePython)
  n = 0.002
FEATURE [App::DocumentObjectGroupPython] Al_element002  label="Al_element : 0.034"  # scripted group (container) (typed FeaturePython)
  n = 0.033872
FEATURE [App::DocumentObjectGroupPython] Si_element002  label="Si_element : 0.337"  # scripted group (container) (typed FeaturePython)
  n = 0.337021
FEATURE [App::DocumentObjectGroupPython] K_element003  label="K_element : 0.013"  # scripted group (container) (typed FeaturePython)
  n = 0.013
FEATURE [App::DocumentObjectGroupPython] Ca_element010  label="Ca_element : 0.044"  # scripted group (container) (typed FeaturePython)
  n = 0.044
FEATURE [App::DocumentObjectGroupPython] Fe_element002  label="Fe_element : 0.014"  # scripted group (container) (typed FeaturePython)
  n = 0.014
FEATURE [App::DocumentObjectGroupPython] G4_CONCRETE  # scripted group (container) (typed FeaturePython)
  Dunit = g/cm3
  Dvalue = 2.3
  Group = -> [H_element027,C_element030,O_element030,Na_element005,Mg_element003,Al_element002,Si_element002,K_element003,Ca_element010,Fe_element002]
  conduct = 2
  density = 1
  expand = 3
  formula = G4_CONCRETE
  name = G4_CONCRETE
  specific = 4
FEATURE [App::DocumentObjectGroupPython] C_element031  label="C_element : 015"  # scripted group (container) (typed FeaturePython)
  n = 6
  ref = C_element
FEATURE [App::DocumentObjectGroupPython] H_element028  label="H_element : 12"  # scripted group (container) (typed FeaturePython)
  n = 12
  ref = H_element
FEATURE [App::DocumentObjectGroupPython] G4_CYCLOHEXANE  # scripted group (container) (typed FeaturePython)
  Dunit = g/cm3
  Dvalue = 0.779
  Group = -> [C_element031,H_element028]
  conduct = 2
  density = 1
  expand = 3
  formula = G4_CYCLOHEXANE
  name = G4_CYCLOHEXANE
  specific = 4
FEATURE [App::DocumentObjectGroupPython] C_element032  label="C_element : 016"  # scripted group (container) (typed FeaturePython)
  n = 6
  ref = C_element
FEATURE [App::DocumentObjectGroupPython] H_element029  label="H_element : 4"  # scripted group (container) (typed FeaturePython)
  n = 4
  ref = H_element
FEATURE [App::DocumentObjectGroupPython] Cl_element007  label="Cl_element : 2"  # scripted group (container) (typed FeaturePython)
  n = 2
  ref = Cl_element
FEATURE [App::DocumentObjectGroupPython] G4_1_2_DICHLOROBENZENE  label="G4_1.2-DICHLOROBENZENE"  # scripted group (container) (typed FeaturePython)
  Dunit = g/cm3
  Dvalue = 1.3048
  Group = -> [C_element032,H_element029,Cl_element007]
  conduct = 2
  density = 1
  expand = 3
  formula = G4_1.2-DICHLOROBENZENE
  name = G4_1.2-DICHLOROBENZENE
  specific = 4
FEATURE [App::DocumentObjectGroupPython] C_element033  label="C_element : 017"  # scripted group (container) (typed FeaturePython)
  n = 4
  ref = C_element
FEATURE [App::DocumentObjectGroupPython] H_element030  label="H_element : 8"  # scripted group (container) (typed FeaturePython)
  n = 8
  ref = H_element
FEATURE [App::DocumentObjectGroupPython] O_element031  label="O_element : 014"  # scripted group (container) (typed FeaturePython)
  n = 1
  ref = O_element
FEATURE [App::DocumentObjectGroupPython] Cl_element008  label="Cl_element : 005"  # scripted group (container) (typed FeaturePython)
  n = 2
  ref = Cl_element
FEATURE [App::DocumentObjectGroupPython] G4_DICHLORODIETHYL_ETHER  # scripted group (container) (typed FeaturePython)
  Dunit = g/cm3
  Dvalue = 1.2199
  Group = -> [C_element033,H_element030,O_element031,Cl_element008]
  conduct = 2
  density = 1
  expand = 3
  formula = G4_DICHLORODIETHYL_ETHER
  name = G4_DICHLORODIETHYL_ETHER
  specific = 4
FEATURE [App::DocumentObjectGroupPython] C_element034  label="C_element : 018"  # scripted group (container) (typed FeaturePython)
  n = 2
  ref = C_element
FEATURE [App::DocumentObjectGroupPython] H_element031  label="H_element : 014"  # scripted group (container) (typed FeaturePython)
  n = 4
  ref = H_element
FEATURE [App::DocumentObjectGroupPython] Cl_element009  label="Cl_element : 006"  # scripted group (container) (typed FeaturePython)
  n = 2
  ref = Cl_element
FEATURE [App::DocumentObjectGroupPython] G4_1_2_DICHLOROETHANE  label="G4_1.2-DICHLOROETHANE"  # scripted group (container) (typed FeaturePython)
  Dunit = g/cm3
  Dvalue = 1.2351
  Group = -> [C_element034,H_element031,Cl_element009]
  conduct = 2
  density = 1
  expand = 3
  formula = G4_1.2-DICHLOROETHANE
  name = G4_1.2-DICHLOROETHANE
  specific = 4
FEATURE [App::DocumentObjectGroupPython] C_element035  label="C_element : 019"  # scripted group (container) (typed FeaturePython)
  n = 4
  ref = C_element
FEATURE [App::DocumentObjectGroupPython] H_element032  label="H_element : 015"  # scripted group (container) (typed FeaturePython)
  n = 10
  ref = H_element
FEATURE [App::DocumentObjectGroupPython] O_element032  label="O_element : 015"  # scripted group (container) (typed FeaturePython)
  n = 1
  ref = O_element
FEATURE [App::DocumentObjectGroupPython] G4_DIETHYL_ETHER  # scripted group (container) (typed FeaturePython)
  Dunit = g/cm3
  Dvalue = 0.71378
  Group = -> [C_element035,H_element032,O_element032]
  conduct = 2
  density = 1
  expand = 3
  formula = G4_DIETHYL_ETHER
  name = G4_DIETHYL_ETHER
  specific = 4
FEATURE [App::DocumentObjectGroupPython] C_element036  label="C_element : 020"  # scripted group (container) (typed FeaturePython)
  n = 3
  ref = C_element
FEATURE [App::DocumentObjectGroupPython] H_element033  label="H_element : 016"  # scripted group (container) (typed FeaturePython)
  n = 7
  ref = H_element
FEATURE [App::DocumentObjectGroupPython] N_element015  label="N_element : 008"  # scripted group (container) (typed FeaturePython)
  n = 1
  ref = N_element
FEATURE [App::DocumentObjectGroupPython] O_element033  label="O_element : 016"  # scripted group (container) (typed FeaturePython)
  n = 1
  ref = O_element
FEATURE [App::DocumentObjectGroupPython] G4_N_N_DIMETHYL_FORMAMIDE  label="G4_N.N-DIMETHYL_FORMAMIDE"  # scripted group (container) (typed FeaturePython)
  Dunit = g/cm3
  Dvalue = 0.9487
  Group = -> [C_element036,H_element033,N_element015,O_element033]
  conduct = 2
  density = 1
  expand = 3
  formula = G4_N.N-DIMETHYL_FORMAMIDE
  name = G4_N.N-DIMETHYL_FORMAMIDE
  specific = 4
FEATURE [App::DocumentObjectGroupPython] C_element037  label="C_element : 021"  # scripted group (container) (typed FeaturePython)
  n = 2
  ref = C_element
FEATURE [App::DocumentObjectGroupPython] H_element034  label="H_element : 017"  # scripted group (container) (typed FeaturePython)
  n = 6
  ref = H_element
FEATURE [App::DocumentObjectGroupPython] O_element034  label="O_element : 017"  # scripted group (container) (typed FeaturePython)
  n = 1
  ref = O_element
FEATURE [App::DocumentObjectGroupPython] S_element009  label="S_element : 003"  # scripted group (container) (typed FeaturePython)
  n = 1
  ref = S_element
FEATURE [App::DocumentObjectGroupPython] G4_DIMETHYL_SULFOXIDE  # scripted group (container) (typed FeaturePython)
  Dunit = g/cm3
  Dvalue = 1.1014
  Group = -> [C_element037,H_element034,O_element034,S_element009]
  conduct = 2
  density = 1
  expand = 3
  formula = G4_DIMETHYL_SULFOXIDE
  name = G4_DIMETHYL_SULFOXIDE
  specific = 4
FEATURE [App::DocumentObjectGroupPython] C_element038  label="C_element : 022"  # scripted group (container) (typed FeaturePython)
  n = 2
  ref = C_element
FEATURE [App::DocumentObjectGroupPython] H_element035  label="H_element : 018"  # scripted group (container) (typed FeaturePython)
  n = 6
  ref = H_element
FEATURE [App::DocumentObjectGroupPython] G4_ETHANE  # scripted group (container) (typed FeaturePython)
  Dunit = g/cm3
  Dvalue = 0.00125324
  Group = -> [C_element038,H_element035]
  conduct = 2
  density = 1
  expand = 3
  formula = G4_ETHANE
  name = G4_ETHANE
  specific = 4
FEATURE [App::DocumentObjectGroupPython] C_element039  label="C_element : 023"  # scripted group (container) (typed FeaturePython)
  n = 2
  ref = C_element
FEATURE [App::DocumentObjectGroupPython] H_element036  label="H_element : 019"  # scripted group (container) (typed FeaturePython)
  n = 6
  ref = H_element
FEATURE [App::DocumentObjectGroupPython] O_element035  label="O_element : 018"  # scripted group (container) (typed FeaturePython)
  n = 1
  ref = O_element
FEATURE [App::DocumentObjectGroupPython] G4_ETHYL_ALCOHOL  # scripted group (container) (typed FeaturePython)
  Dunit = g/cm3
  Dvalue = 0.7893
  Group = -> [C_element039,H_element036,O_element035]
  conduct = 2
  density = 1
  expand = 3
  formula = G4_ETHYL_ALCOHOL
  name = G4_ETHYL_ALCOHOL
  specific = 4
FEATURE [App::DocumentObjectGroupPython] H_element037  label="H_element : 0.090"  # scripted group (container) (typed FeaturePython)
  n = 0.090027
FEATURE [App::DocumentObjectGroupPython] C_element040  label="C_element : 0.585"  # scripted group (container) (typed FeaturePython)
  n = 0.585182
FEATURE [App::DocumentObjectGroupPython] O_element036  label="O_element : 0.325"  # scripted group (container) (typed FeaturePython)
  n = 0.324791
FEATURE [App::DocumentObjectGroupPython] G4_ETHYL_CELLULOSE  # scripted group (container) (typed FeaturePython)
  Dunit = g/cm3
  Dvalue = 1.13
  Group = -> [H_element037,C_element040,O_element036]
  conduct = 2
  density = 1
  expand = 3
  formula = G4_ETHYL_CELLULOSE
  name = G4_ETHYL_CELLULOSE
  specific = 4
FEATURE [App::DocumentObjectGroupPython] C_element041  label="C_element : 024"  # scripted group (container) (typed FeaturePython)
  n = 2
  ref = C_element
FEATURE [App::DocumentObjectGroupPython] H_element038  label="H_element : 020"  # scripted group (container) (typed FeaturePython)
  n = 4
  ref = H_element
FEATURE [App::DocumentObjectGroupPython] G4_ETHYLENE  # scripted group (container) (typed FeaturePython)
  Dunit = g/cm3
  Dvalue = 0.00117497
  Group = -> [C_element041,H_element038]
  conduct = 2
  density = 1
  expand = 3
  formula = G4_ETHYLENE
  name = G4_ETHYLENE
  specific = 4
FEATURE [App::DocumentObjectGroupPython] H_element039  label="H_element : 0.096"  # scripted group (container) (typed FeaturePython)
  n = 0.096
FEATURE [App::DocumentObjectGroupPython] C_element042  label="C_element : 0.195"  # scripted group (container) (typed FeaturePython)
  n = 0.195
FEATURE [App::DocumentObjectGroupPython] N_element016  label="N_element : 0.057"  # scripted group (container) (typed FeaturePython)
  n = 0.057
FEATURE [App::DocumentObjectGroupPython] O_element037  label="O_element : 0.646"  # scripted group (container) (typed FeaturePython)
  n = 0.646
FEATURE [App::DocumentObjectGroupPython] Na_element006  label="Na_element : 0.017"  # scripted group (container) (typed FeaturePython)
  n = 0.001
FEATURE [App::DocumentObjectGroupPython] P_element005  label="P_element : 0.104"  # scripted group (container) (typed FeaturePython)
  n = 0.001
FEATURE [App::DocumentObjectGroupPython] S_element010  label="S_element : 0.016"  # scripted group (container) (typed FeaturePython)
  n = 0.003
FEATURE [App::DocumentObjectGroupPython] Cl_element010  label="Cl_element : 0.005"  # scripted group (container) (typed FeaturePython)
  n = 0.001
FEATURE [App::DocumentObjectGroupPython] G4_EYE_LENS_ICRP  # scripted group (container) (typed FeaturePython)
  Dunit = g/cm3
  Dvalue = 1.07
  Group = -> [H_element039,C_element042,N_element016,O_element037,Na_element006,P_element005,S_element010,Cl_element010]
  conduct = 2
  density = 1
  expand = 3
  formula = G4_EYE_LENS_ICRP
  name = G4_EYE_LENS_ICRP
  specific = 4
FEATURE [App::DocumentObjectGroupPython] Fe_element003  label="Fe_element : 2"  # scripted group (container) (typed FeaturePython)
  n = 2
  ref = Fe_element
FEATURE [App::DocumentObjectGroupPython] O_element038  label="O_element : 019"  # scripted group (container) (typed FeaturePython)
  n = 3
  ref = O_element
FEATURE [App::DocumentObjectGroupPython] G4_FERRIC_OXIDE  # scripted group (container) (typed FeaturePython)
  Dunit = g/cm3
  Dvalue = 5.2
  Group = -> [Fe_element003,O_element038]
  conduct = 2
  density = 1
  expand = 3
  formula = G4_FERRIC_OXIDE
  name = G4_FERRIC_OXIDE
  specific = 4
FEATURE [App::DocumentObjectGroupPython] Fe_element004  label="Fe_element : 1"  # scripted group (container) (typed FeaturePython)
  n = 1
  ref = Fe_element
FEATURE [App::DocumentObjectGroupPython] B_element003  label="B_element : 1"  # scripted group (container) (typed FeaturePython)
  n = 1
  ref = B_element
FEATURE [App::DocumentObjectGroupPython] G4_FERROBORIDE  # scripted group (container) (typed FeaturePython)
  Dunit = g/cm3
  Dvalue = 7.15
  Group = -> [Fe_element004,B_element003]
  conduct = 2
  density = 1
  expand = 3
  formula = G4_FERROBORIDE
  name = G4_FERROBORIDE
  specific = 4
FEATURE [App::DocumentObjectGroupPython] Fe_element005  label="Fe_element : 003"  # scripted group (container) (typed FeaturePython)
  n = 1
  ref = Fe_element
FEATURE [App::DocumentObjectGroupPython] O_element039  label="O_element : 020"  # scripted group (container) (typed FeaturePython)
  n = 1
  ref = O_element
FEATURE [App::DocumentObjectGroupPython] G4_FERROUS_OXIDE  # scripted group (container) (typed FeaturePython)
  Dunit = g/cm3
  Dvalue = 5.7
  Group = -> [Fe_element005,O_element039]
  conduct = 2
  density = 1
  expand = 3
  formula = G4_FERROUS_OXIDE
  name = G4_FERROUS_OXIDE
  specific = 4
FEATURE [App::DocumentObjectGroupPython] H_element040  label="H_element : 0.115"  # scripted group (container) (typed FeaturePython)
  n = 0.108259
FEATURE [App::DocumentObjectGroupPython] N_element017  label="N_element : 0.000"  # scripted group (container) (typed FeaturePython)
  n = 2.7e-05
FEATURE [App::DocumentObjectGroupPython] O_element040  label="O_element : 0.879"  # scripted group (container) (typed FeaturePython)
  n = 0.878636
FEATURE [App::DocumentObjectGroupPython] Na_element007  label="Na_element : 0.000"  # scripted group (container) (typed FeaturePython)
  n = 2.2e-05
FEATURE [App::DocumentObjectGroupPython] S_element011  label="S_element : 0.013"  # scripted group (container) (typed FeaturePython)
  n = 0.012968
FEATURE [App::DocumentObjectGroupPython] Cl_element011  label="Cl_element : 0.000"  # scripted group (container) (typed FeaturePython)
  n = 3.4e-05
FEATURE [App::DocumentObjectGroupPython] Fe_element006  label="Fe_element : 0.000"  # scripted group (container) (typed FeaturePython)
  n = 5.4e-05
FEATURE [App::DocumentObjectGroupPython] G4_FERROUS_SULFATE  # scripted group (container) (typed FeaturePython)
  Dunit = g/cm3
  Dvalue = 1.024
  Group = -> [H_element040,N_element017,O_element040,Na_element007,S_element011,Cl_element011,Fe_element006]
  conduct = 2
  density = 1
  expand = 3
  formula = G4_FERROUS_SULFATE
  name = G4_FERROUS_SULFATE
  specific = 4
FEATURE [App::DocumentObjectGroupPython] C_element043  label="C_element : 0.099"  # scripted group (container) (typed FeaturePython)
  n = 0.099335
FEATURE [App::DocumentObjectGroupPython] F_element007  label="F_element : 0.314"  # scripted group (container) (typed FeaturePython)
  n = 0.314247
FEATURE [App::DocumentObjectGroupPython] Cl_element012  label="Cl_element : 0.586"  # scripted group (container) (typed FeaturePython)
  n = 0.586418
FEATURE [App::DocumentObjectGroupPython] G4_FREON_12  label="G4_FREON-12"  # scripted group (container) (typed FeaturePython)
  Dunit = g/cm3
  Dvalue = 1.12
  Group = -> [C_element043,F_element007,Cl_element012]
  conduct = 2
  density = 1
  expand = 3
  formula = G4_FREON-12
  name = G4_FREON-12
  specific = 4
FEATURE [App::DocumentObjectGroupPython] C_element044  label="C_element : 0.057"  # scripted group (container) (typed FeaturePython)
  n = 0.057245
FEATURE [App::DocumentObjectGroupPython] F_element008  label="F_element : 0.181"  # scripted group (container) (typed FeaturePython)
  n = 0.181096
FEATURE [App::DocumentObjectGroupPython] Br_element001  label="Br_element : 0.762"  # scripted group (container) (typed FeaturePython)
  n = 0.761659
FEATURE [App::DocumentObjectGroupPython] G4_FREON_12B2  label="G4_FREON-12B2"  # scripted group (container) (typed FeaturePython)
  Dunit = g/cm3
  Dvalue = 1.8
  Group = -> [C_element044,F_element008,Br_element001]
  conduct = 2
  density = 1
  expand = 3
  formula = G4_FREON-12B2
  name = G4_FREON-12B2
  specific = 4
FEATURE [App::DocumentObjectGroupPython] C_element045  label="C_element : 0.115"  # scripted group (container) (typed FeaturePython)
  n = 0.114983
FEATURE [App::DocumentObjectGroupPython] F_element009  label="F_element : 0.546"  # scripted group (container) (typed FeaturePython)
  n = 0.545621
FEATURE [App::DocumentObjectGroupPython] Cl_element013  label="Cl_element : 0.339"  # scripted group (container) (typed FeaturePython)
  n = 0.339396
FEATURE [App::DocumentObjectGroupPython] G4_FREON_13  label="G4_FREON-13"  # scripted group (container) (typed FeaturePython)
  Dunit = g/cm3
  Dvalue = 0.95
  Group = -> [C_element045,F_element009,Cl_element013]
  conduct = 2
  density = 1
  expand = 3
  formula = G4_FREON-13
  name = G4_FREON-13
  specific = 4
FEATURE [App::DocumentObjectGroupPython] C_element046  label="C_element : 025"  # scripted group (container) (typed FeaturePython)
  n = 1
  ref = C_element
FEATURE [App::DocumentObjectGroupPython] F_element010  label="F_element : 3"  # scripted group (container) (typed FeaturePython)
  n = 3
  ref = F_element
FEATURE [App::DocumentObjectGroupPython] Br_element002  label="Br_element : 1"  # scripted group (container) (typed FeaturePython)
  n = 1
  ref = Br_element
FEATURE [App::DocumentObjectGroupPython] G4_FREON_13B1  label="G4_FREON-13B1"  # scripted group (container) (typed FeaturePython)
  Dunit = g/cm3
  Dvalue = 1.5
  Group = -> [C_element046,F_element010,Br_element002]
  conduct = 2
  density = 1
  expand = 3
  formula = G4_FREON-13B1
  name = G4_FREON-13B1
  specific = 4
FEATURE [App::DocumentObjectGroupPython] C_element047  label="C_element : 0.061"  # scripted group (container) (typed FeaturePython)
  n = 0.061309
FEATURE [App::DocumentObjectGroupPython] F_element011  label="F_element : 0.291"  # scripted group (container) (typed FeaturePython)
  n = 0.290924
FEATURE [App::DocumentObjectGroupPython] I_element002  label="I_element : 0.648"  # scripted group (container) (typed FeaturePython)
  n = 0.647767
FEATURE [App::DocumentObjectGroupPython] G4_FREON_13I1  label="G4_FREON-13I1"  # scripted group (container) (typed FeaturePython)
  Dunit = g/cm3
  Dvalue = 1.8
  Group = -> [C_element047,F_element011,I_element002]
  conduct = 2
  density = 1
  expand = 3
  formula = G4_FREON-13I1
  name = G4_FREON-13I1
  specific = 4
FEATURE [App::DocumentObjectGroupPython] Gd_element001  label="Gd_element : 2"  # scripted group (container) (typed FeaturePython)
  n = 2
  ref = Gd_element
FEATURE [App::DocumentObjectGroupPython] O_element041  label="O_element : 021"  # scripted group (container) (typed FeaturePython)
  n = 2
  ref = O_element
FEATURE [App::DocumentObjectGroupPython] S_element012  label="S_element : 004"  # scripted group (container) (typed FeaturePython)
  n = 1
  ref = S_element
FEATURE [App::DocumentObjectGroupPython] G4_GADOLINIUM_OXYSULFIDE  # scripted group (container) (typed FeaturePython)
  Dunit = g/cm3
  Dvalue = 7.44
  Group = -> [Gd_element001,O_element041,S_element012]
  conduct = 2
  density = 1
  expand = 3
  formula = G4_GADOLINIUM_OXYSULFIDE
  name = G4_GADOLINIUM_OXYSULFIDE
  specific = 4
FEATURE [App::DocumentObjectGroupPython] Ga_element001  label="Ga_element : 1"  # scripted group (container) (typed FeaturePython)
  n = 1
  ref = Ga_element
FEATURE [App::DocumentObjectGroupPython] As_element001  label="As_element : 1"  # scripted group (container) (typed FeaturePython)
  n = 1
  ref = As_element
FEATURE [App::DocumentObjectGroupPython] G4_GALLIUM_ARSENIDE  # scripted group (container) (typed FeaturePython)
  Dunit = g/cm3
  Dvalue = 5.31
  Group = -> [Ga_element001,As_element001]
  conduct = 2
  density = 1
  expand = 3
  formula = G4_GALLIUM_ARSENIDE
  name = G4_GALLIUM_ARSENIDE
  specific = 4
FEATURE [App::DocumentObjectGroupPython] H_element041  label="H_element : 0.081"  # scripted group (container) (typed FeaturePython)
  n = 0.08118
FEATURE [App::DocumentObjectGroupPython] C_element048  label="C_element : 0.416"  # scripted group (container) (typed FeaturePython)
  n = 0.41606
FEATURE [App::DocumentObjectGroupPython] N_element018  label="N_element : 0.111"  # scripted group (container) (typed FeaturePython)
  n = 0.11124
FEATURE [App::DocumentObjectGroupPython] O_element042  label="O_element : 0.381"  # scripted group (container) (typed FeaturePython)
  n = 0.38064
FEATURE [App::DocumentObjectGroupPython] S_element013  label="S_element : 0.011"  # scripted group (container) (typed FeaturePython)
  n = 0.01088
FEATURE [App::DocumentObjectGroupPython] G4_GEL_PHOTO_EMULSION  # scripted group (container) (typed FeaturePython)
  Dunit = g/cm3
  Dvalue = 1.2914
  Group = -> [H_element041,C_element048,N_element018,O_element042,S_element013]
  conduct = 2
  density = 1
  expand = 3
  formula = G4_GEL_PHOTO_EMULSION
  name = G4_GEL_PHOTO_EMULSION
  specific = 4
FEATURE [App::DocumentObjectGroupPython] B_element004  label="B_element : 0.040"  # scripted group (container) (typed FeaturePython)
  n = 0.0400639
FEATURE [App::DocumentObjectGroupPython] O_element043  label="O_element : 0.540"  # scripted group (container) (typed FeaturePython)
  n = 0.539561
FEATURE [App::DocumentObjectGroupPython] Na_element008  label="Na_element : 0.028"  # scripted group (container) (typed FeaturePython)
  n = 0.0281909
FEATURE [App::DocumentObjectGroupPython] Al_element003  label="Al_element : 0.012"  # scripted group (container) (typed FeaturePython)
  n = 0.011644
FEATURE [App::DocumentObjectGroupPython] Si_element003  label="Si_element : 0.377"  # scripted group (container) (typed FeaturePython)
  n = 0.377219
FEATURE [App::DocumentObjectGroupPython] K_element004  label="K_element : 0.014"  # scripted group (container) (typed FeaturePython)
  n = 0.00332099
FEATURE [App::DocumentObjectGroupPython] G4_Pyrex_Glass  # scripted group (container) (typed FeaturePython)
  Dunit = g/cm3
  Dvalue = 2.23
  Group = -> [B_element004,O_element043,Na_element008,Al_element003,Si_element003,K_element004]
  conduct = 2
  density = 1
  expand = 3
  formula = G4_Pyrex_Glass
  name = G4_Pyrex_Glass
  specific = 4
FEATURE [App::DocumentObjectGroupPython] O_element044  label="O_element : 0.156"  # scripted group (container) (typed FeaturePython)
  n = 0.156453
FEATURE [App::DocumentObjectGroupPython] Si_element004  label="Si_element : 0.081"  # scripted group (container) (typed FeaturePython)
  n = 0.080866
FEATURE [App::DocumentObjectGroupPython] Ti_element001  label="Ti_element : 0.008"  # scripted group (container) (typed FeaturePython)
  n = 0.008092
FEATURE [App::DocumentObjectGroupPython] As_element002  label="As_element : 0.003"  # scripted group (container) (typed FeaturePython)
  n = 0.002651
FEATURE [App::DocumentObjectGroupPython] Pb_element001  label="Pb_element : 0.752"  # scripted group (container) (typed FeaturePython)
  n = 0.751938
FEATURE [App::DocumentObjectGroupPython] G4_GLASS_LEAD  # scripted group (container) (typed FeaturePython)
  Dunit = g/cm3
  Dvalue = 6.22
  Group = -> [O_element044,Si_element004,Ti_element001,As_element002,Pb_element001]
  conduct = 2
  density = 1
  expand = 3
  formula = G4_GLASS_LEAD
  name = G4_GLASS_LEAD
  specific = 4
FEATURE [App::DocumentObjectGroupPython] O_element045  label="O_element : 0.460"  # scripted group (container) (typed FeaturePython)
  n = 0.4598
FEATURE [App::DocumentObjectGroupPython] Na_element009  label="Na_element : 0.096"  # scripted group (container) (typed FeaturePython)
  n = 0.0964411
FEATURE [App::DocumentObjectGroupPython] Si_element005  label="Si_element : 0.378"  # scripted group (container) (typed FeaturePython)
  n = 0.336553
FEATURE [App::DocumentObjectGroupPython] Ca_element011  label="Ca_element : 0.107"  # scripted group (container) (typed FeaturePython)
  n = 0.107205
FEATURE [App::DocumentObjectGroupPython] G4_GLASS_PLATE  # scripted group (container) (typed FeaturePython)
  Dunit = g/cm3
  Dvalue = 2.4
  Group = -> [O_element045,Na_element009,Si_element005,Ca_element011]
  conduct = 2
  density = 1
  expand = 3
  formula = G4_GLASS_PLATE
  name = G4_GLASS_PLATE
  specific = 4
FEATURE [App::DocumentObjectGroupPython] C_element049  label="C_element : 026"  # scripted group (container) (typed FeaturePython)
  n = 5
  ref = C_element
FEATURE [App::DocumentObjectGroupPython] H_element042  label="H_element : 021"  # scripted group (container) (typed FeaturePython)
  n = 10
  ref = H_element
FEATURE [App::DocumentObjectGroupPython] N_element019  label="N_element : 2"  # scripted group (container) (typed FeaturePython)
  n = 2
  ref = N_element
FEATURE [App::DocumentObjectGroupPython] O_element046  label="O_element : 022"  # scripted group (container) (typed FeaturePython)
  n = 3
  ref = O_element
FEATURE [App::DocumentObjectGroupPython] G4_GLUTAMINE  # scripted group (container) (typed FeaturePython)
  Dunit = g/cm3
  Dvalue = 1.46
  Group = -> [C_element049,H_element042,N_element019,O_element046]
  conduct = 2
  density = 1
  expand = 3
  formula = G4_GLUTAMINE
  name = G4_GLUTAMINE
  specific = 4
FEATURE [App::DocumentObjectGroupPython] C_element050  label="C_element : 027"  # scripted group (container) (typed FeaturePython)
  n = 3
  ref = C_element
FEATURE [App::DocumentObjectGroupPython] H_element043  label="H_element : 022"  # scripted group (container) (typed FeaturePython)
  n = 8
  ref = H_element
FEATURE [App::DocumentObjectGroupPython] O_element047  label="O_element : 023"  # scripted group (container) (typed FeaturePython)
  n = 3
  ref = O_element
FEATURE [App::DocumentObjectGroupPython] G4_GLYCEROL  # scripted group (container) (typed FeaturePython)
  Dunit = g/cm3
  Dvalue = 1.2613
  Group = -> [C_element050,H_element043,O_element047]
  conduct = 2
  density = 1
  expand = 3
  formula = G4_GLYCEROL
  name = G4_GLYCEROL
  specific = 4
FEATURE [App::DocumentObjectGroupPython] C_element051  label="C_element : 028"  # scripted group (container) (typed FeaturePython)
  n = 5
  ref = C_element
FEATURE [App::DocumentObjectGroupPython] H_element044  label="H_element : 023"  # scripted group (container) (typed FeaturePython)
  n = 5
  ref = H_element
FEATURE [App::DocumentObjectGroupPython] N_element020  label="N_element : 009"  # scripted group (container) (typed FeaturePython)
  n = 5
  ref = N_element
FEATURE [App::DocumentObjectGroupPython] O_element048  label="O_element : 024"  # scripted group (container) (typed FeaturePython)
  n = 1
  ref = O_element
FEATURE [App::DocumentObjectGroupPython] G4_GUANINE  # scripted group (container) (typed FeaturePython)
  Dunit = g/cm3
  Dvalue = 2.2
  Group = -> [C_element051,H_element044,N_element020,O_element048]
  conduct = 2
  density = 1
  expand = 3
  formula = G4_GUANINE
  name = G4_GUANINE
  specific = 4
FEATURE [App::DocumentObjectGroupPython] Ca_element012  label="Ca_element : 006"  # scripted group (container) (typed FeaturePython)
  n = 1
  ref = Ca_element
FEATURE [App::DocumentObjectGroupPython] S_element014  label="S_element : 005"  # scripted group (container) (typed FeaturePython)
  n = 1
  ref = S_element
FEATURE [App::DocumentObjectGroupPython] O_element049  label="O_element : 6"  # scripted group (container) (typed FeaturePython)
  n = 6
  ref = O_element
FEATURE [App::DocumentObjectGroupPython] H_element045  label="H_element : 024"  # scripted group (container) (typed FeaturePython)
  n = 4
  ref = H_element
FEATURE [App::DocumentObjectGroupPython] G4_GYPSUM  # scripted group (container) (typed FeaturePython)
  Dunit = g/cm3
  Dvalue = 2.32
  Group = -> [Ca_element012,S_element014,O_element049,H_element045]
  conduct = 2
  density = 1
  expand = 3
  formula = G4_GYPSUM
  name = G4_GYPSUM
  specific = 4
FEATURE [App::DocumentObjectGroupPython] C_element052  label="C_element : 7"  # scripted group (container) (typed FeaturePython)
  n = 7
  ref = C_element
FEATURE [App::DocumentObjectGroupPython] H_element046  label="H_element : 16"  # scripted group (container) (typed FeaturePython)
  n = 16
  ref = H_element
FEATURE [App::DocumentObjectGroupPython] G4_N_HEPTANE  label="G4_N-HEPTANE"  # scripted group (container) (typed FeaturePython)
  Dunit = g/cm3
  Dvalue = 0.68376
  Group = -> [C_element052,H_element046]
  conduct = 2
  density = 1
  expand = 3
  formula = G4_N-HEPTANE
  name = G4_N-HEPTANE
  specific = 4
FEATURE [App::DocumentObjectGroupPython] C_element053  label="C_element : 029"  # scripted group (container) (typed FeaturePython)
  n = 6
  ref = C_element
FEATURE [App::DocumentObjectGroupPython] H_element047  label="H_element : 14"  # scripted group (container) (typed FeaturePython)
  n = 14
  ref = H_element
FEATURE [App::DocumentObjectGroupPython] G4_N_HEXANE  label="G4_N-HEXANE"  # scripted group (container) (typed FeaturePython)
  Dunit = g/cm3
  Dvalue = 0.6603
  Group = -> [C_element053,H_element047]
  conduct = 2
  density = 1
  expand = 3
  formula = G4_N-HEXANE
  name = G4_N-HEXANE
  specific = 4
FEATURE [App::DocumentObjectGroupPython] C_element054  label="C_element : 22"  # scripted group (container) (typed FeaturePython)
  n = 22
  ref = C_element
FEATURE [App::DocumentObjectGroupPython] H_element048  label="H_element : 025"  # scripted group (container) (typed FeaturePython)
  n = 10
  ref = H_element
FEATURE [App::DocumentObjectGroupPython] N_element021  label="N_element : 010"  # scripted group (container) (typed FeaturePython)
  n = 2
  ref = N_element
FEATURE [App::DocumentObjectGroupPython] O_element050  label="O_element : 025"  # scripted group (container) (typed FeaturePython)
  n = 5
  ref = O_element
FEATURE [App::DocumentObjectGroupPython] G4_KAPTON  # scripted group (container) (typed FeaturePython)
  Dunit = g/cm3
  Dvalue = 1.42
  Group = -> [C_element054,H_element048,N_element021,O_element050]
  conduct = 2
  density = 1
  expand = 3
  formula = G4_KAPTON
  name = G4_KAPTON
  specific = 4
FEATURE [App::DocumentObjectGroupPython] La_element001  label="La_element : 1"  # scripted group (container) (typed FeaturePython)
  n = 1
  ref = La_element
FEATURE [App::DocumentObjectGroupPython] Br_element003  label="Br_element : 002"  # scripted group (container) (typed FeaturePython)
  n = 1
  ref = Br_element
FEATURE [App::DocumentObjectGroupPython] O_element051  label="O_element : 026"  # scripted group (container) (typed FeaturePython)
  n = 1
  ref = O_element
FEATURE [App::DocumentObjectGroupPython] G4_LANTHANUM_OXYBROMIDE  # scripted group (container) (typed FeaturePython)
  Dunit = g/cm3
  Dvalue = 6.28
  Group = -> [La_element001,Br_element003,O_element051]
  conduct = 2
  density = 1
  expand = 3
  formula = G4_LANTHANUM_OXYBROMIDE
  name = G4_LANTHANUM_OXYBROMIDE
  specific = 4
FEATURE [App::DocumentObjectGroupPython] La_element002  label="La_element : 2"  # scripted group (container) (typed FeaturePython)
  n = 2
  ref = La_element
FEATURE [App::DocumentObjectGroupPython] O_element052  label="O_element : 027"  # scripted group (container) (typed FeaturePython)
  n = 2
  ref = O_element
FEATURE [App::DocumentObjectGroupPython] S_element015  label="S_element : 006"  # scripted group (container) (typed FeaturePython)
  n = 1
  ref = S_element
FEATURE [App::DocumentObjectGroupPython] G4_LANTHANUM_OXYSULFIDE  # scripted group (container) (typed FeaturePython)
  Dunit = g/cm3
  Dvalue = 5.86
  Group = -> [La_element002,O_element052,S_element015]
  conduct = 2
  density = 1
  expand = 3
  formula = G4_LANTHANUM_OXYSULFIDE
  name = G4_LANTHANUM_OXYSULFIDE
  specific = 4
FEATURE [App::DocumentObjectGroupPython] O_element053  label="O_element : 0.072"  # scripted group (container) (typed FeaturePython)
  n = 0.071682
FEATURE [App::DocumentObjectGroupPython] Pb_element002  label="Pb_element : 0.928"  # scripted group (container) (typed FeaturePython)
  n = 0.928318
FEATURE [App::DocumentObjectGroupPython] G4_LEAD_OXIDE  # scripted group (container) (typed FeaturePython)
  Dunit = g/cm3
  Dvalue = 9.53
  Group = -> [O_element053,Pb_element002]
  conduct = 2
  density = 1
  expand = 3
  formula = G4_LEAD_OXIDE
  name = G4_LEAD_OXIDE
  specific = 4
FEATURE [App::DocumentObjectGroupPython] Li_element001  label="Li_element : 1"  # scripted group (container) (typed FeaturePython)
  n = 1
  ref = Li_element
FEATURE [App::DocumentObjectGroupPython] N_element022  label="N_element : 011"  # scripted group (container) (typed FeaturePython)
  n = 1
  ref = N_element
FEATURE [App::DocumentObjectGroupPython] H_element049  label="H_element : 026"  # scripted group (container) (typed FeaturePython)
  n = 2
  ref = H_element
FEATURE [App::DocumentObjectGroupPython] G4_LITHIUM_AMIDE  # scripted group (container) (typed FeaturePython)
  Dunit = g/cm3
  Dvalue = 1.178
  Group = -> [Li_element001,N_element022,H_element049]
  conduct = 2
  density = 1
  expand = 3
  formula = G4_LITHIUM_AMIDE
  name = G4_LITHIUM_AMIDE
  specific = 4
FEATURE [App::DocumentObjectGroupPython] Li_element002  label="Li_element : 2"  # scripted group (container) (typed FeaturePython)
  n = 2
  ref = Li_element
FEATURE [App::DocumentObjectGroupPython] C_element055  label="C_element : 030"  # scripted group (container) (typed FeaturePython)
  n = 1
  ref = C_element
FEATURE [App::DocumentObjectGroupPython] O_element054  label="O_element : 028"  # scripted group (container) (typed FeaturePython)
  n = 3
  ref = O_element
FEATURE [App::DocumentObjectGroupPython] G4_LITHIUM_CARBONATE  # scripted group (container) (typed FeaturePython)
  Dunit = g/cm3
  Dvalue = 2.11
  Group = -> [Li_element002,C_element055,O_element054]
  conduct = 2
  density = 1
  expand = 3
  formula = G4_LITHIUM_CARBONATE
  name = G4_LITHIUM_CARBONATE
  specific = 4
FEATURE [App::DocumentObjectGroupPython] Li_element003  label="Li_element : 003"  # scripted group (container) (typed FeaturePython)
  n = 1
  ref = Li_element
FEATURE [App::DocumentObjectGroupPython] F_element012  label="F_element : 004"  # scripted group (container) (typed FeaturePython)
  n = 1
  ref = F_element
FEATURE [App::DocumentObjectGroupPython] G4_LITHIUM_FLUORIDE  # scripted group (container) (typed FeaturePython)
  Dunit = g/cm3
  Dvalue = 2.635
  Group = -> [Li_element003,F_element012]
  conduct = 2
  density = 1
  expand = 3
  formula = G4_LITHIUM_FLUORIDE
  name = G4_LITHIUM_FLUORIDE
  specific = 4
FEATURE [App::DocumentObjectGroupPython] Li_element004  label="Li_element : 004"  # scripted group (container) (typed FeaturePython)
  n = 1
  ref = Li_element
FEATURE [App::DocumentObjectGroupPython] H_element050  label="H_element : 027"  # scripted group (container) (typed FeaturePython)
  n = 1
  ref = H_element
FEATURE [App::DocumentObjectGroupPython] G4_LITHIUM_HYDRIDE  # scripted group (container) (typed FeaturePython)
  Dunit = g/cm3
  Dvalue = 0.82
  Group = -> [Li_element004,H_element050]
  conduct = 2
  density = 1
  expand = 3
  formula = G4_LITHIUM_HYDRIDE
  name = G4_LITHIUM_HYDRIDE
  specific = 4
FEATURE [App::DocumentObjectGroupPython] Li_element005  label="Li_element : 005"  # scripted group (container) (typed FeaturePython)
  n = 1
  ref = Li_element
FEATURE [App::DocumentObjectGroupPython] I_element003  label="I_element : 002"  # scripted group (container) (typed FeaturePython)
  n = 1
  ref = I_element
FEATURE [App::DocumentObjectGroupPython] G4_LITHIUM_IODIDE  # scripted group (container) (typed FeaturePython)
  Dunit = g/cm3
  Dvalue = 3.494
  Group = -> [Li_element005,I_element003]
  conduct = 2
  density = 1
  expand = 3
  formula = G4_LITHIUM_IODIDE
  name = G4_LITHIUM_IODIDE
  specific = 4
FEATURE [App::DocumentObjectGroupPython] Li_element006  label="Li_element : 006"  # scripted group (container) (typed FeaturePython)
  n = 2
  ref = Li_element
FEATURE [App::DocumentObjectGroupPython] O_element055  label="O_element : 029"  # scripted group (container) (typed FeaturePython)
  n = 1
  ref = O_element
FEATURE [App::DocumentObjectGroupPython] G4_LITHIUM_OXIDE  # scripted group (container) (typed FeaturePython)
  Dunit = g/cm3
  Dvalue = 2.013
  Group = -> [Li_element006,O_element055]
  conduct = 2
  density = 1
  expand = 3
  formula = G4_LITHIUM_OXIDE
  name = G4_LITHIUM_OXIDE
  specific = 4
FEATURE [App::DocumentObjectGroupPython] Li_element007  label="Li_element : 007"  # scripted group (container) (typed FeaturePython)
  n = 2
  ref = Li_element
FEATURE [App::DocumentObjectGroupPython] B_element005  label="B_element : 005"  # scripted group (container) (typed FeaturePython)
  n = 4
  ref = B_element
FEATURE [App::DocumentObjectGroupPython] O_element056  label="O_element : 7"  # scripted group (container) (typed FeaturePython)
  n = 7
  ref = O_element
FEATURE [App::DocumentObjectGroupPython] G4_LITHIUM_TETRABORATE  # scripted group (container) (typed FeaturePython)
  Dunit = g/cm3
  Dvalue = 2.44
  Group = -> [Li_element007,B_element005,O_element056]
  conduct = 2
  density = 1
  expand = 3
  formula = G4_LITHIUM_TETRABORATE
  name = G4_LITHIUM_TETRABORATE
  specific = 4
FEATURE [App::DocumentObjectGroupPython] H_element051  label="H_element : 0.105"  # scripted group (container) (typed FeaturePython)
  n = 0.105
FEATURE [App::DocumentObjectGroupPython] C_element056  label="C_element : 0.083"  # scripted group (container) (typed FeaturePython)
  n = 0.083
FEATURE [App::DocumentObjectGroupPython] N_element023  label="N_element : 0.023"  # scripted group (container) (typed FeaturePython)
  n = 0.023
FEATURE [App::DocumentObjectGroupPython] O_element057  label="O_element : 0.779"  # scripted group (container) (typed FeaturePython)
  n = 0.779
FEATURE [App::DocumentObjectGroupPython] Na_element010  label="Na_element : 0.097"  # scripted group (container) (typed FeaturePython)
  n = 0.002
FEATURE [App::DocumentObjectGroupPython] P_element006  label="P_element : 0.105"  # scripted group (container) (typed FeaturePython)
  n = 0.001
FEATURE [App::DocumentObjectGroupPython] S_element016  label="S_element : 0.017"  # scripted group (container) (typed FeaturePython)
  n = 0.002
FEATURE [App::DocumentObjectGroupPython] Cl_element014  label="Cl_element : 0.587"  # scripted group (container) (typed FeaturePython)
  n = 0.003
FEATURE [App::DocumentObjectGroupPython] K_element005  label="K_element : 0.015"  # scripted group (container) (typed FeaturePython)
  n = 0.002
FEATURE [App::DocumentObjectGroupPython] G4_LUNG_ICRP  # scripted group (container) (typed FeaturePython)
  Dunit = g/cm3
  Dvalue = 1.04
  Group = -> [H_element051,C_element056,N_element023,O_element057,Na_element010,P_element006,S_element016,Cl_element014,K_element005]
  conduct = 2
  density = 1
  expand = 3
  formula = G4_LUNG_ICRP
  name = G4_LUNG_ICRP
  specific = 4
FEATURE [App::DocumentObjectGroupPython] H_element052  label="H_element : 0.116"  # scripted group (container) (typed FeaturePython)
  n = 0.114318
FEATURE [App::DocumentObjectGroupPython] C_element057  label="C_element : 0.656"  # scripted group (container) (typed FeaturePython)
  n = 0.655824
FEATURE [App::DocumentObjectGroupPython] O_element058  label="O_element : 0.092"  # scripted group (container) (typed FeaturePython)
  n = 0.0921831
FEATURE [App::DocumentObjectGroupPython] Mg_element004  label="Mg_element : 0.135"  # scripted group (container) (typed FeaturePython)
  n = 0.134792
FEATURE [App::DocumentObjectGroupPython] Ca_element013  label="Ca_element : 0.003"  # scripted group (container) (typed FeaturePython)
  n = 0.002883
FEATURE [App::DocumentObjectGroupPython] G4_M3_WAX  # scripted group (container) (typed FeaturePython)
  Dunit = g/cm3
  Dvalue = 1.05
  Group = -> [H_element052,C_element057,O_element058,Mg_element004,Ca_element013]
  conduct = 2
  density = 1
  expand = 3
  formula = G4_M3_WAX
  name = G4_M3_WAX
  specific = 4
FEATURE [App::DocumentObjectGroupPython] Mg_element005  label="Mg_element : 1"  # scripted group (container) (typed FeaturePython)
  n = 1
  ref = Mg_element
FEATURE [App::DocumentObjectGroupPython] C_element058  label="C_element : 031"  # scripted group (container) (typed FeaturePython)
  n = 1
  ref = C_element
FEATURE [App::DocumentObjectGroupPython] O_element059  label="O_element : 030"  # scripted group (container) (typed FeaturePython)
  n = 3
  ref = O_element
FEATURE [App::DocumentObjectGroupPython] G4_MAGNESIUM_CARBONATE  # scripted group (container) (typed FeaturePython)
  Dunit = g/cm3
  Dvalue = 2.958
  Group = -> [Mg_element005,C_element058,O_element059]
  conduct = 2
  density = 1
  expand = 3
  formula = G4_MAGNESIUM_CARBONATE
  name = G4_MAGNESIUM_CARBONATE
  specific = 4
FEATURE [App::DocumentObjectGroupPython] Mg_element006  label="Mg_element : 002"  # scripted group (container) (typed FeaturePython)
  n = 1
  ref = Mg_element
FEATURE [App::DocumentObjectGroupPython] F_element013  label="F_element : 005"  # scripted group (container) (typed FeaturePython)
  n = 2
  ref = F_element
FEATURE [App::DocumentObjectGroupPython] G4_MAGNESIUM_FLUORIDE  # scripted group (container) (typed FeaturePython)
  Dunit = g/cm3
  Dvalue = 3
  Group = -> [Mg_element006,F_element013]
  conduct = 2
  density = 1
  expand = 3
  formula = G4_MAGNESIUM_FLUORIDE
  name = G4_MAGNESIUM_FLUORIDE
  specific = 4
FEATURE [App::DocumentObjectGroupPython] Mg_element007  label="Mg_element : 003"  # scripted group (container) (typed FeaturePython)
  n = 1
  ref = Mg_element
FEATURE [App::DocumentObjectGroupPython] O_element060  label="O_element : 031"  # scripted group (container) (typed FeaturePython)
  n = 1
  ref = O_element
FEATURE [App::DocumentObjectGroupPython] G4_MAGNESIUM_OXIDE  # scripted group (container) (typed FeaturePython)
  Dunit = g/cm3
  Dvalue = 3.58
  Group = -> [Mg_element007,O_element060]
  conduct = 2
  density = 1
  expand = 3
  formula = G4_MAGNESIUM_OXIDE
  name = G4_MAGNESIUM_OXIDE
  specific = 4
FEATURE [App::DocumentObjectGroupPython] Mg_element008  label="Mg_element : 004"  # scripted group (container) (typed FeaturePython)
  n = 1
  ref = Mg_element
FEATURE [App::DocumentObjectGroupPython] B_element006  label="B_element : 006"  # scripted group (container) (typed FeaturePython)
  n = 4
  ref = B_element
FEATURE [App::DocumentObjectGroupPython] O_element061  label="O_element : 032"  # scripted group (container) (typed FeaturePython)
  n = 7
  ref = O_element
FEATURE [App::DocumentObjectGroupPython] G4_MAGNESIUM_TETRABORATE  # scripted group (container) (typed FeaturePython)
  Dunit = g/cm3
  Dvalue = 2.53
  Group = -> [Mg_element008,B_element006,O_element061]
  conduct = 2
  density = 1
  expand = 3
  formula = G4_MAGNESIUM_TETRABORATE
  name = G4_MAGNESIUM_TETRABORATE
  specific = 4
FEATURE [App::DocumentObjectGroupPython] Hg_element001  label="Hg_element : 1"  # scripted group (container) (typed FeaturePython)
  n = 1
  ref = Hg_element
FEATURE [App::DocumentObjectGroupPython] I_element004  label="I_element : 2"  # scripted group (container) (typed FeaturePython)
  n = 2
  ref = I_element
FEATURE [App::DocumentObjectGroupPython] G4_MERCURIC_IODIDE  # scripted group (container) (typed FeaturePython)
  Dunit = g/cm3
  Dvalue = 6.36
  Group = -> [Hg_element001,I_element004]
  conduct = 2
  density = 1
  expand = 3
  formula = G4_MERCURIC_IODIDE
  name = G4_MERCURIC_IODIDE
  specific = 4
FEATURE [App::DocumentObjectGroupPython] C_element059  label="C_element : 032"  # scripted group (container) (typed FeaturePython)
  n = 1
  ref = C_element
FEATURE [App::DocumentObjectGroupPython] H_element053  label="H_element : 028"  # scripted group (container) (typed FeaturePython)
  n = 4
  ref = H_element
FEATURE [App::DocumentObjectGroupPython] G4_METHANE  # scripted group (container) (typed FeaturePython)
  Dunit = g/cm3
  Dvalue = 0.000667151
  Group = -> [C_element059,H_element053]
  conduct = 2
  density = 1
  expand = 3
  formula = G4_METHANE
  name = G4_METHANE
  specific = 4
FEATURE [App::DocumentObjectGroupPython] C_element060  label="C_element : 033"  # scripted group (container) (typed FeaturePython)
  n = 1
  ref = C_element
FEATURE [App::DocumentObjectGroupPython] H_element054  label="H_element : 029"  # scripted group (container) (typed FeaturePython)
  n = 4
  ref = H_element
FEATURE [App::DocumentObjectGroupPython] O_element062  label="O_element : 033"  # scripted group (container) (typed FeaturePython)
  n = 1
  ref = O_element
FEATURE [App::DocumentObjectGroupPython] G4_METHANOL  # scripted group (container) (typed FeaturePython)
  Dunit = g/cm3
  Dvalue = 0.7914
  Group = -> [C_element060,H_element054,O_element062]
  conduct = 2
  density = 1
  expand = 3
  formula = G4_METHANOL
  name = G4_METHANOL
  specific = 4
FEATURE [App::DocumentObjectGroupPython] H_element055  label="H_element : 0.134"  # scripted group (container) (typed FeaturePython)
  n = 0.13404
FEATURE [App::DocumentObjectGroupPython] C_element061  label="C_element : 0.778"  # scripted group (container) (typed FeaturePython)
  n = 0.77796
FEATURE [App::DocumentObjectGroupPython] O_element063  label="O_element : 0.035"  # scripted group (container) (typed FeaturePython)
  n = 0.03502
FEATURE [App::DocumentObjectGroupPython] Mg_element009  label="Mg_element : 0.039"  # scripted group (container) (typed FeaturePython)
  n = 0.038594
FEATURE [App::DocumentObjectGroupPython] Ti_element002  label="Ti_element : 0.014"  # scripted group (container) (typed FeaturePython)
  n = 0.014386
FEATURE [App::DocumentObjectGroupPython] G4_MIX_D_WAX  # scripted group (container) (typed FeaturePython)
  Dunit = g/cm3
  Dvalue = 0.99
  Group = -> [H_element055,C_element061,O_element063,Mg_element009,Ti_element002]
  conduct = 2
  density = 1
  expand = 3
  formula = G4_MIX_D_WAX
  name = G4_MIX_D_WAX
  specific = 4
FEATURE [App::DocumentObjectGroupPython] H_element056  label="H_element : 0.135"  # scripted group (container) (typed FeaturePython)
  n = 0.081192
FEATURE [App::DocumentObjectGroupPython] C_element062  label="C_element : 0.583"  # scripted group (container) (typed FeaturePython)
  n = 0.583442
FEATURE [App::DocumentObjectGroupPython] N_element024  label="N_element : 0.018"  # scripted group (container) (typed FeaturePython)
  n = 0.017798
FEATURE [App::DocumentObjectGroupPython] O_element064  label="O_element : 0.186"  # scripted group (container) (typed FeaturePython)
  n = 0.186381
FEATURE [App::DocumentObjectGroupPython] Mg_element010  label="Mg_element : 0.130"  # scripted group (container) (typed FeaturePython)
  n = 0.130287
FEATURE [App::DocumentObjectGroupPython] Cl_element015  label="Cl_element : 0.588"  # scripted group (container) (typed FeaturePython)
  n = 0.0009
FEATURE [App::DocumentObjectGroupPython] G4_MS20_TISSUE  # scripted group (container) (typed FeaturePython)
  Dunit = g/cm3
  Dvalue = 1
  Group = -> [H_element056,C_element062,N_element024,O_element064,Mg_element010,Cl_element015]
  conduct = 2
  density = 1
  expand = 3
  formula = G4_MS20_TISSUE
  name = G4_MS20_TISSUE
  specific = 4
FEATURE [App::DocumentObjectGroupPython] H_element057  label="H_element : 0.136"  # scripted group (container) (typed FeaturePython)
  n = 0.102
FEATURE [App::DocumentObjectGroupPython] C_element063  label="C_element : 0.143"  # scripted group (container) (typed FeaturePython)
  n = 0.143
FEATURE [App::DocumentObjectGroupPython] N_element025  label="N_element : 0.034"  # scripted group (container) (typed FeaturePython)
  n = 0.034
FEATURE [App::DocumentObjectGroupPython] O_element065  label="O_element : 0.710"  # scripted group (container) (typed FeaturePython)
  n = 0.71
FEATURE [App::DocumentObjectGroupPython] Na_element011  label="Na_element : 0.098"  # scripted group (container) (typed FeaturePython)
  n = 0.001
FEATURE [App::DocumentObjectGroupPython] P_element007  label="P_element : 0.002"  # scripted group (container) (typed FeaturePython)
  n = 0.002
FEATURE [App::DocumentObjectGroupPython] S_element017  label="S_element : 0.018"  # scripted group (container) (typed FeaturePython)
  n = 0.003
FEATURE [App::DocumentObjectGroupPython] Cl_element016  label="Cl_element : 0.589"  # scripted group (container) (typed FeaturePython)
  n = 0.001
FEATURE [App::DocumentObjectGroupPython] K_element006  label="K_element : 0.004"  # scripted group (container) (typed FeaturePython)
  n = 0.004
FEATURE [App::DocumentObjectGroupPython] G4_MUSCLE_SKELETAL_ICRP  # scripted group (container) (typed FeaturePython)
  Dunit = g/cm3
  Dvalue = 1.05
  Group = -> [H_element057,C_element063,N_element025,O_element065,Na_element011,P_element007,S_element017,Cl_element016,K_element006]
  conduct = 2
  density = 1
  expand = 3
  formula = G4_MUSCLE_SKELETAL_ICRP
  name = G4_MUSCLE_SKELETAL_ICRP
  specific = 4
FEATURE [App::DocumentObjectGroupPython] H_element058  label="H_element : 0.137"  # scripted group (container) (typed FeaturePython)
  n = 0.102102
FEATURE [App::DocumentObjectGroupPython] C_element064  label="C_element : 0.123"  # scripted group (container) (typed FeaturePython)
  n = 0.123123
FEATURE [App::DocumentObjectGroupPython] N_element026  label="N_element : 0.756"  # scripted group (container) (typed FeaturePython)
  n = 0.035035
FEATURE [App::DocumentObjectGroupPython] O_element066  label="O_element : 0.730"  # scripted group (container) (typed FeaturePython)
  n = 0.72973
FEATURE [App::DocumentObjectGroupPython] Na_element012  label="Na_element : 0.099"  # scripted group (container) (typed FeaturePython)
  n = 0.001001
FEATURE [App::DocumentObjectGroupPython] P_element008  label="P_element : 0.106"  # scripted group (container) (typed FeaturePython)
  n = 0.002002
FEATURE [App::DocumentObjectGroupPython] S_element018  label="S_element : 0.019"  # scripted group (container) (typed FeaturePython)
  n = 0.004004
FEATURE [App::DocumentObjectGroupPython] K_element007  label="K_element : 0.016"  # scripted group (container) (typed FeaturePython)
  n = 0.003003
FEATURE [App::DocumentObjectGroupPython] G4_MUSCLE_STRIATED_ICRU  # scripted group (container) (typed FeaturePython)
  Dunit = g/cm3
  Dvalue = 1.04
  Group = -> [H_element058,C_element064,N_element026,O_element066,Na_element012,P_element008,S_element018,K_element007]
  conduct = 2
  density = 1
  expand = 3
  formula = G4_MUSCLE_STRIATED_ICRU
  name = G4_MUSCLE_STRIATED_ICRU
  specific = 4
FEATURE [App::DocumentObjectGroupPython] H_element059  label="H_element : 0.098"  # scripted group (container) (typed FeaturePython)
  n = 0.0982341
FEATURE [App::DocumentObjectGroupPython] C_element065  label="C_element : 0.156"  # scripted group (container) (typed FeaturePython)
  n = 0.156214
FEATURE [App::DocumentObjectGroupPython] N_element027  label="N_element : 0.757"  # scripted group (container) (typed FeaturePython)
  n = 0.035451
FEATURE [App::DocumentObjectGroupPython] O_element067  label="O_element : 0.880"  # scripted group (container) (typed FeaturePython)
  n = 0.710101
FEATURE [App::DocumentObjectGroupPython] G4_MUSCLE_WITH_SUCROSE  # scripted group (container) (typed FeaturePython)
  Dunit = g/cm3
  Dvalue = 1.11
  Group = -> [H_element059,C_element065,N_element027,O_element067]
  conduct = 2
  density = 1
  expand = 3
  formula = G4_MUSCLE_WITH_SUCROSE
  name = G4_MUSCLE_WITH_SUCROSE
  specific = 4
FEATURE [App::DocumentObjectGroupPython] H_element060  label="H_element : 0.138"  # scripted group (container) (typed FeaturePython)
  n = 0.101969
FEATURE [App::DocumentObjectGroupPython] C_element066  label="C_element : 0.120"  # scripted group (container) (typed FeaturePython)
  n = 0.120058
FEATURE [App::DocumentObjectGroupPython] N_element028  label="N_element : 0.758"  # scripted group (container) (typed FeaturePython)
  n = 0.035451
FEATURE [App::DocumentObjectGroupPython] O_element068  label="O_element : 0.743"  # scripted group (container) (typed FeaturePython)
  n = 0.742522
FEATURE [App::DocumentObjectGroupPython] G4_MUSCLE_WITHOUT_SUCROSE  # scripted group (container) (typed FeaturePython)
  Dunit = g/cm3
  Dvalue = 1.07
  Group = -> [H_element060,C_element066,N_element028,O_element068]
  conduct = 2
  density = 1
  expand = 3
  formula = G4_MUSCLE_WITHOUT_SUCROSE
  name = G4_MUSCLE_WITHOUT_SUCROSE
  specific = 4
FEATURE [App::DocumentObjectGroupPython] C_element067  label="C_element : 10"  # scripted group (container) (typed FeaturePython)
  n = 10
  ref = C_element
FEATURE [App::DocumentObjectGroupPython] H_element061  label="H_element : 030"  # scripted group (container) (typed FeaturePython)
  n = 8
  ref = H_element
FEATURE [App::DocumentObjectGroupPython] G4_NAPHTHALENE  # scripted group (container) (typed FeaturePython)
  Dunit = g/cm3
  Dvalue = 1.145
  Group = -> [C_element067,H_element061]
  conduct = 2
  density = 1
  expand = 3
  formula = G4_NAPHTHALENE
  name = G4_NAPHTHALENE
  specific = 4
FEATURE [App::DocumentObjectGroupPython] C_element068  label="C_element : 034"  # scripted group (container) (typed FeaturePython)
  n = 6
  ref = C_element
FEATURE [App::DocumentObjectGroupPython] H_element062  label="H_element : 031"  # scripted group (container) (typed FeaturePython)
  n = 5
  ref = H_element
FEATURE [App::DocumentObjectGroupPython] N_element029  label="N_element : 012"  # scripted group (container) (typed FeaturePython)
  n = 1
  ref = N_element
FEATURE [App::DocumentObjectGroupPython] O_element069  label="O_element : 034"  # scripted group (container) (typed FeaturePython)
  n = 2
  ref = O_element
FEATURE [App::DocumentObjectGroupPython] G4_NITROBENZENE  # scripted group (container) (typed FeaturePython)
  Dunit = g/cm3
  Dvalue = 1.19867
  Group = -> [C_element068,H_element062,N_element029,O_element069]
  conduct = 2
  density = 1
  expand = 3
  formula = G4_NITROBENZENE
  name = G4_NITROBENZENE
  specific = 4
FEATURE [App::DocumentObjectGroupPython] N_element030  label="N_element : 013"  # scripted group (container) (typed FeaturePython)
  n = 2
  ref = N_element
FEATURE [App::DocumentObjectGroupPython] O_element070  label="O_element : 035"  # scripted group (container) (typed FeaturePython)
  n = 1
  ref = O_element
FEATURE [App::DocumentObjectGroupPython] G4_NITROUS_OXIDE  # scripted group (container) (typed FeaturePython)
  Dunit = g/cm3
  Dvalue = 0.00183094
  Group = -> [N_element030,O_element070]
  conduct = 2
  density = 1
  expand = 3
  formula = G4_NITROUS_OXIDE
  name = G4_NITROUS_OXIDE
  specific = 4
FEATURE [App::DocumentObjectGroupPython] H_element063  label="H_element : 0.104"  # scripted group (container) (typed FeaturePython)
  n = 0.103509
FEATURE [App::DocumentObjectGroupPython] C_element069  label="C_element : 0.648"  # scripted group (container) (typed FeaturePython)
  n = 0.648416
FEATURE [App::DocumentObjectGroupPython] N_element031  label="N_element : 0.100"  # scripted group (container) (typed FeaturePython)
  n = 0.0995361
FEATURE [App::DocumentObjectGroupPython] O_element071  label="O_element : 0.149"  # scripted group (container) (typed FeaturePython)
  n = 0.148539
FEATURE [App::DocumentObjectGroupPython] G4_NYLON_8062  label="G4_NYLON-8062"  # scripted group (container) (typed FeaturePython)
  Dunit = g/cm3
  Dvalue = 1.08
  Group = -> [H_element063,C_element069,N_element031,O_element071]
  conduct = 2
  density = 1
  expand = 3
  formula = G4_NYLON-8062
  name = G4_NYLON-8062
  specific = 4
FEATURE [App::DocumentObjectGroupPython] C_element070  label="C_element : 035"  # scripted group (container) (typed FeaturePython)
  n = 6
  ref = C_element
FEATURE [App::DocumentObjectGroupPython] H_element064  label="H_element : 11"  # scripted group (container) (typed FeaturePython)
  n = 11
  ref = H_element
FEATURE [App::DocumentObjectGroupPython] N_element032  label="N_element : 014"  # scripted group (container) (typed FeaturePython)
  n = 1
  ref = N_element
FEATURE [App::DocumentObjectGroupPython] O_element072  label="O_element : 036"  # scripted group (container) (typed FeaturePython)
  n = 1
  ref = O_element
FEATURE [App::DocumentObjectGroupPython] G4_NYLON_6_6  label="G4_NYLON-6-6"  # scripted group (container) (typed FeaturePython)
  Dunit = g/cm3
  Dvalue = 1.14
  Group = -> [C_element070,H_element064,N_element032,O_element072]
  conduct = 2
  density = 1
  expand = 3
  formula = G4_NYLON-6-6
  name = G4_NYLON-6-6
  specific = 4
FEATURE [App::DocumentObjectGroupPython] H_element065  label="H_element : 0.139"  # scripted group (container) (typed FeaturePython)
  n = 0.107062
FEATURE [App::DocumentObjectGroupPython] C_element071  label="C_element : 0.680"  # scripted group (container) (typed FeaturePython)
  n = 0.680449
FEATURE [App::DocumentObjectGroupPython] N_element033  label="N_element : 0.099"  # scripted group (container) (typed FeaturePython)
  n = 0.099189
FEATURE [App::DocumentObjectGroupPython] O_element073  label="O_element : 0.113"  # scripted group (container) (typed FeaturePython)
  n = 0.1133
FEATURE [App::DocumentObjectGroupPython] G4_NYLON_6_10  label="G4_NYLON-6-10"  # scripted group (container) (typed FeaturePython)
  Dunit = g/cm3
  Dvalue = 1.14
  Group = -> [H_element065,C_element071,N_element033,O_element073]
  conduct = 2
  density = 1
  expand = 3
  formula = G4_NYLON-6-10
  name = G4_NYLON-6-10
  specific = 4
FEATURE [App::DocumentObjectGroupPython] H_element066  label="H_element : 0.140"  # scripted group (container) (typed FeaturePython)
  n = 0.115476
FEATURE [App::DocumentObjectGroupPython] C_element072  label="C_element : 0.721"  # scripted group (container) (typed FeaturePython)
  n = 0.720818
FEATURE [App::DocumentObjectGroupPython] N_element034  label="N_element : 0.076"  # scripted group (container) (typed FeaturePython)
  n = 0.0764169
FEATURE [App::DocumentObjectGroupPython] O_element074  label="O_element : 0.087"  # scripted group (container) (typed FeaturePython)
  n = 0.0872889
FEATURE [App::DocumentObjectGroupPython] G4_NYLON_11_RILSAN  label="G4_NYLON-11_RILSAN"  # scripted group (container) (typed FeaturePython)
  Dunit = g/cm3
  Dvalue = 1.425
  Group = -> [H_element066,C_element072,N_element034,O_element074]
  conduct = 2
  density = 1
  expand = 3
  formula = G4_NYLON-11_RILSAN
  name = G4_NYLON-11_RILSAN
  specific = 4
FEATURE [App::DocumentObjectGroupPython] C_element073  label="C_element : 8"  # scripted group (container) (typed FeaturePython)
  n = 8
  ref = C_element
FEATURE [App::DocumentObjectGroupPython] H_element067  label="H_element : 18"  # scripted group (container) (typed FeaturePython)
  n = 18
  ref = H_element
FEATURE [App::DocumentObjectGroupPython] G4_OCTANE  # scripted group (container) (typed FeaturePython)
  Dunit = g/cm3
  Dvalue = 0.7026
  Group = -> [C_element073,H_element067]
  conduct = 2
  density = 1
  expand = 3
  formula = G4_OCTANE
  name = G4_OCTANE
  specific = 4
FEATURE [App::DocumentObjectGroupPython] C_element074  label="C_element : 25"  # scripted group (container) (typed FeaturePython)
  n = 25
  ref = C_element
FEATURE [App::DocumentObjectGroupPython] H_element068  label="H_element : 52"  # scripted group (container) (typed FeaturePython)
  n = 52
  ref = H_element
FEATURE [App::DocumentObjectGroupPython] G4_PARAFFIN  # scripted group (container) (typed FeaturePython)
  Dunit = g/cm3
  Dvalue = 0.93
  Group = -> [C_element074,H_element068]
  conduct = 2
  density = 1
  expand = 3
  formula = G4_PARAFFIN
  name = G4_PARAFFIN
  specific = 4
FEATURE [App::DocumentObjectGroupPython] C_element075  label="C_element : 036"  # scripted group (container) (typed FeaturePython)
  n = 5
  ref = C_element
FEATURE [App::DocumentObjectGroupPython] H_element069  label="H_element : 032"  # scripted group (container) (typed FeaturePython)
  n = 12
  ref = H_element
FEATURE [App::DocumentObjectGroupPython] G4_N_PENTANE  label="G4_N-PENTANE"  # scripted group (container) (typed FeaturePython)
  Dunit = g/cm3
  Dvalue = 0.6262
  Group = -> [C_element075,H_element069]
  conduct = 2
  density = 1
  expand = 3
  formula = G4_N-PENTANE
  name = G4_N-PENTANE
  specific = 4
FEATURE [App::DocumentObjectGroupPython] H_element070  label="H_element : 0.014"  # scripted group (container) (typed FeaturePython)
  n = 0.0141
FEATURE [App::DocumentObjectGroupPython] C_element076  label="C_element : 0.072"  # scripted group (container) (typed FeaturePython)
  n = 0.072261
FEATURE [App::DocumentObjectGroupPython] N_element035  label="N_element : 0.019"  # scripted group (container) (typed FeaturePython)
  n = 0.01932
FEATURE [App::DocumentObjectGroupPython] O_element075  label="O_element : 0.066"  # scripted group (container) (typed FeaturePython)
  n = 0.066101
FEATURE [App::DocumentObjectGroupPython] S_element019  label="S_element : 0.020"  # scripted group (container) (typed FeaturePython)
  n = 0.00189
FEATURE [App::DocumentObjectGroupPython] Br_element004  label="Br_element : 0.349"  # scripted group (container) (typed FeaturePython)
  n = 0.349103
FEATURE [App::DocumentObjectGroupPython] Ag_element001  label="Ag_element : 0.474"  # scripted group (container) (typed FeaturePython)
  n = 0.474105
FEATURE [App::DocumentObjectGroupPython] I_element005  label="I_element : 0.003"  # scripted group (container) (typed FeaturePython)
  n = 0.00312
FEATURE [App::DocumentObjectGroupPython] G4_PHOTO_EMULSION  # scripted group (container) (typed FeaturePython)
  Dunit = g/cm3
  Dvalue = 3.815
  Group = -> [H_element070,C_element076,N_element035,O_element075,S_element019,Br_element004,Ag_element001,I_element005]
  conduct = 2
  density = 1
  expand = 3
  formula = G4_PHOTO_EMULSION
  name = G4_PHOTO_EMULSION
  specific = 4
FEATURE [App::DocumentObjectGroupPython] C_element077  label="C_element : 9"  # scripted group (container) (typed FeaturePython)
  n = 9
  ref = C_element
FEATURE [App::DocumentObjectGroupPython] H_element071  label="H_element : 033"  # scripted group (container) (typed FeaturePython)
  n = 10
  ref = H_element
FEATURE [App::DocumentObjectGroupPython] G4_PLASTIC_SC_VINYLTOLUENE  # scripted group (container) (typed FeaturePython)
  Dunit = g/cm3
  Dvalue = 1.032
  Group = -> [C_element077,H_element071]
  conduct = 2
  density = 1
  expand = 3
  formula = G4_PLASTIC_SC_VINYLTOLUENE
  name = G4_PLASTIC_SC_VINYLTOLUENE
  specific = 4
FEATURE [App::DocumentObjectGroupPython] Pu_element001  label="Pu_element : 1"  # scripted group (container) (typed FeaturePython)
  n = 1
  ref = Pu_element
FEATURE [App::DocumentObjectGroupPython] O_element076  label="O_element : 037"  # scripted group (container) (typed FeaturePython)
  n = 2
  ref = O_element
FEATURE [App::DocumentObjectGroupPython] G4_PLUTONIUM_DIOXIDE  # scripted group (container) (typed FeaturePython)
  Dunit = g/cm3
  Dvalue = 11.46
  Group = -> [Pu_element001,O_element076]
  conduct = 2
  density = 1
  expand = 3
  formula = G4_PLUTONIUM_DIOXIDE
  name = G4_PLUTONIUM_DIOXIDE
  specific = 4
FEATURE [App::DocumentObjectGroupPython] C_element078  label="C_element : 037"  # scripted group (container) (typed FeaturePython)
  n = 3
  ref = C_element
FEATURE [App::DocumentObjectGroupPython] H_element072  label="H_element : 034"  # scripted group (container) (typed FeaturePython)
  n = 3
  ref = H_element
FEATURE [App::DocumentObjectGroupPython] N_element036  label="N_element : 015"  # scripted group (container) (typed FeaturePython)
  n = 1
  ref = N_element
FEATURE [App::DocumentObjectGroupPython] G4_POLYACRYLONITRILE  # scripted group (container) (typed FeaturePython)
  Dunit = g/cm3
  Dvalue = 1.17
  Group = -> [C_element078,H_element072,N_element036]
  conduct = 2
  density = 1
  expand = 3
  formula = G4_POLYACRYLONITRILE
  name = G4_POLYACRYLONITRILE
  specific = 4
FEATURE [App::DocumentObjectGroupPython] C_element079  label="C_element : 16"  # scripted group (container) (typed FeaturePython)
  n = 16
  ref = C_element
FEATURE [App::DocumentObjectGroupPython] H_element073  label="H_element : 035"  # scripted group (container) (typed FeaturePython)
  n = 14
  ref = H_element
FEATURE [App::DocumentObjectGroupPython] O_element077  label="O_element : 038"  # scripted group (container) (typed FeaturePython)
  n = 3
  ref = O_element
FEATURE [App::DocumentObjectGroupPython] G4_POLYCARBONATE  # scripted group (container) (typed FeaturePython)
  Dunit = g/cm3
  Dvalue = 1.2
  Group = -> [C_element079,H_element073,O_element077]
  conduct = 2
  density = 1
  expand = 3
  formula = G4_POLYCARBONATE
  name = G4_POLYCARBONATE
  specific = 4
FEATURE [App::DocumentObjectGroupPython] C_element080  label="C_element : 038"  # scripted group (container) (typed FeaturePython)
  n = 8
  ref = C_element
FEATURE [App::DocumentObjectGroupPython] H_element074  label="H_element : 036"  # scripted group (container) (typed FeaturePython)
  n = 7
  ref = H_element
FEATURE [App::DocumentObjectGroupPython] Cl_element017  label="Cl_element : 007"  # scripted group (container) (typed FeaturePython)
  n = 1
  ref = Cl_element
FEATURE [App::DocumentObjectGroupPython] G4_POLYCHLOROSTYRENE  # scripted group (container) (typed FeaturePython)
  Dunit = g/cm3
  Dvalue = 1.3
  Group = -> [C_element080,H_element074,Cl_element017]
  conduct = 2
  density = 1
  expand = 3
  formula = G4_POLYCHLOROSTYRENE
  name = G4_POLYCHLOROSTYRENE
  specific = 4
FEATURE [App::DocumentObjectGroupPython] C_element081  label="C_element : 039"  # scripted group (container) (typed FeaturePython)
  n = 1
  ref = C_element
FEATURE [App::DocumentObjectGroupPython] H_element075  label="H_element : 037"  # scripted group (container) (typed FeaturePython)
  n = 2
  ref = H_element
FEATURE [App::DocumentObjectGroupPython] G4_POLYETHYLENE  # scripted group (container) (typed FeaturePython)
  Dunit = g/cm3
  Dvalue = 0.94
  Group = -> [C_element081,H_element075]
  conduct = 2
  density = 1
  expand = 3
  formula = G4_POLYETHYLENE
  name = G4_POLYETHYLENE
  specific = 4
FEATURE [App::DocumentObjectGroupPython] C_element082  label="C_element : 040"  # scripted group (container) (typed FeaturePython)
  n = 10
  ref = C_element
FEATURE [App::DocumentObjectGroupPython] H_element076  label="H_element : 038"  # scripted group (container) (typed FeaturePython)
  n = 8
  ref = H_element
FEATURE [App::DocumentObjectGroupPython] O_element078  label="O_element : 039"  # scripted group (container) (typed FeaturePython)
  n = 4
  ref = O_element
FEATURE [App::DocumentObjectGroupPython] G4_MYLAR  # scripted group (container) (typed FeaturePython)
  Dunit = g/cm3
  Dvalue = 1.4
  Group = -> [C_element082,H_element076,O_element078]
  conduct = 2
  density = 1
  expand = 3
  formula = G4_MYLAR
  name = G4_MYLAR
  specific = 4
FEATURE [App::DocumentObjectGroupPython] C_element083  label="C_element : 041"  # scripted group (container) (typed FeaturePython)
  n = 5
  ref = C_element
FEATURE [App::DocumentObjectGroupPython] H_element077  label="H_element : 039"  # scripted group (container) (typed FeaturePython)
  n = 8
  ref = H_element
FEATURE [App::DocumentObjectGroupPython] O_element079  label="O_element : 040"  # scripted group (container) (typed FeaturePython)
  n = 2
  ref = O_element
FEATURE [App::DocumentObjectGroupPython] G4_PLEXIGLASS  # scripted group (container) (typed FeaturePython)
  Dunit = g/cm3
  Dvalue = 1.19
  Group = -> [C_element083,H_element077,O_element079]
  conduct = 2
  density = 1
  expand = 3
  formula = G4_PLEXIGLASS
  name = G4_PLEXIGLASS
  specific = 4
FEATURE [App::DocumentObjectGroupPython] C_element084  label="C_element : 042"  # scripted group (container) (typed FeaturePython)
  n = 1
  ref = C_element
FEATURE [App::DocumentObjectGroupPython] H_element078  label="H_element : 040"  # scripted group (container) (typed FeaturePython)
  n = 2
  ref = H_element
FEATURE [App::DocumentObjectGroupPython] O_element080  label="O_element : 041"  # scripted group (container) (typed FeaturePython)
  n = 1
  ref = O_element
FEATURE [App::DocumentObjectGroupPython] G4_POLYOXYMETHYLENE  # scripted group (container) (typed FeaturePython)
  Dunit = g/cm3
  Dvalue = 1.425
  Group = -> [C_element084,H_element078,O_element080]
  conduct = 2
  density = 1
  expand = 3
  formula = G4_POLYOXYMETHYLENE
  name = G4_POLYOXYMETHYLENE
  specific = 4
FEATURE [App::DocumentObjectGroupPython] C_element085  label="C_element : 043"  # scripted group (container) (typed FeaturePython)
  n = 2
  ref = C_element
FEATURE [App::DocumentObjectGroupPython] H_element079  label="H_element : 041"  # scripted group (container) (typed FeaturePython)
  n = 4
  ref = H_element
FEATURE [App::DocumentObjectGroupPython] G4_POLYPROPYLENE  # scripted group (container) (typed FeaturePython)
  Dunit = g/cm3
  Dvalue = 0.9
  Group = -> [C_element085,H_element079]
  conduct = 2
  density = 1
  expand = 3
  formula = G4_POLYPROPYLENE
  name = G4_POLYPROPYLENE
  specific = 4
FEATURE [App::DocumentObjectGroupPython] C_element086  label="C_element : 044"  # scripted group (container) (typed FeaturePython)
  n = 8
  ref = C_element
FEATURE [App::DocumentObjectGroupPython] H_element080  label="H_element : 042"  # scripted group (container) (typed FeaturePython)
  n = 8
  ref = H_element
FEATURE [App::DocumentObjectGroupPython] G4_POLYSTYRENE  # scripted group (container) (typed FeaturePython)
  Dunit = g/cm3
  Dvalue = 1.06
  Group = -> [C_element086,H_element080]
  conduct = 2
  density = 1
  expand = 3
  formula = G4_POLYSTYRENE
  name = G4_POLYSTYRENE
  specific = 4
FEATURE [App::DocumentObjectGroupPython] C_element087  label="C_element : 045"  # scripted group (container) (typed FeaturePython)
  n = 2
  ref = C_element
FEATURE [App::DocumentObjectGroupPython] F_element014  label="F_element : 4"  # scripted group (container) (typed FeaturePython)
  n = 4
  ref = F_element
FEATURE [App::DocumentObjectGroupPython] G4_TEFLON  # scripted group (container) (typed FeaturePython)
  Dunit = g/cm3
  Dvalue = 2.2
  Group = -> [C_element087,F_element014]
  conduct = 2
  density = 1
  expand = 3
  formula = G4_TEFLON
  name = G4_TEFLON
  specific = 4
FEATURE [App::DocumentObjectGroupPython] C_element088  label="C_element : 046"  # scripted group (container) (typed FeaturePython)
  n = 2
  ref = C_element
FEATURE [App::DocumentObjectGroupPython] F_element015  label="F_element : 006"  # scripted group (container) (typed FeaturePython)
  n = 3
  ref = F_element
FEATURE [App::DocumentObjectGroupPython] Cl_element018  label="Cl_element : 008"  # scripted group (container) (typed FeaturePython)
  n = 1
  ref = Cl_element
FEATURE [App::DocumentObjectGroupPython] G4_POLYTRIFLUOROCHLOROETHYLENE  # scripted group (container) (typed FeaturePython)
  Dunit = g/cm3
  Dvalue = 2.1
  Group = -> [C_element088,F_element015,Cl_element018]
  conduct = 2
  density = 1
  expand = 3
  formula = G4_POLYTRIFLUOROCHLOROETHYLENE
  name = G4_POLYTRIFLUOROCHLOROETHYLENE
  specific = 4
FEATURE [App::DocumentObjectGroupPython] C_element089  label="C_element : 047"  # scripted group (container) (typed FeaturePython)
  n = 4
  ref = C_element
FEATURE [App::DocumentObjectGroupPython] H_element081  label="H_element : 043"  # scripted group (container) (typed FeaturePython)
  n = 6
  ref = H_element
FEATURE [App::DocumentObjectGroupPython] O_element081  label="O_element : 042"  # scripted group (container) (typed FeaturePython)
  n = 2
  ref = O_element
FEATURE [App::DocumentObjectGroupPython] G4_POLYVINYL_ACETATE  # scripted group (container) (typed FeaturePython)
  Dunit = g/cm3
  Dvalue = 1.19
  Group = -> [C_element089,H_element081,O_element081]
  conduct = 2
  density = 1
  expand = 3
  formula = G4_POLYVINYL_ACETATE
  name = G4_POLYVINYL_ACETATE
  specific = 4
FEATURE [App::DocumentObjectGroupPython] C_element090  label="C_element : 048"  # scripted group (container) (typed FeaturePython)
  n = 2
  ref = C_element
FEATURE [App::DocumentObjectGroupPython] H_element082  label="H_element : 044"  # scripted group (container) (typed FeaturePython)
  n = 4
  ref = H_element
FEATURE [App::DocumentObjectGroupPython] O_element082  label="O_element : 043"  # scripted group (container) (typed FeaturePython)
  n = 1
  ref = O_element
FEATURE [App::DocumentObjectGroupPython] G4_POLYVINYL_ALCOHOL  # scripted group (container) (typed FeaturePython)
  Dunit = g/cm3
  Dvalue = 1.3
  Group = -> [C_element090,H_element082,O_element082]
  conduct = 2
  density = 1
  expand = 3
  formula = G4_POLYVINYL_ALCOHOL
  name = G4_POLYVINYL_ALCOHOL
  specific = 4
FEATURE [App::DocumentObjectGroupPython] C_element091  label="C_element : 049"  # scripted group (container) (typed FeaturePython)
  n = 8
  ref = C_element
FEATURE [App::DocumentObjectGroupPython] H_element083  label="H_element : 045"  # scripted group (container) (typed FeaturePython)
  n = 14
  ref = H_element
FEATURE [App::DocumentObjectGroupPython] O_element083  label="O_element : 044"  # scripted group (container) (typed FeaturePython)
  n = 2
  ref = O_element
FEATURE [App::DocumentObjectGroupPython] G4_POLYVINYL_BUTYRAL  # scripted group (container) (typed FeaturePython)
  Dunit = g/cm3
  Dvalue = 1.12
  Group = -> [C_element091,H_element083,O_element083]
  conduct = 2
  density = 1
  expand = 3
  formula = G4_POLYVINYL_BUTYRAL
  name = G4_POLYVINYL_BUTYRAL
  specific = 4
FEATURE [App::DocumentObjectGroupPython] C_element092  label="C_element : 050"  # scripted group (container) (typed FeaturePython)
  n = 2
  ref = C_element
FEATURE [App::DocumentObjectGroupPython] H_element084  label="H_element : 046"  # scripted group (container) (typed FeaturePython)
  n = 3
  ref = H_element
FEATURE [App::DocumentObjectGroupPython] Cl_element019  label="Cl_element : 009"  # scripted group (container) (typed FeaturePython)
  n = 1
  ref = Cl_element
FEATURE [App::DocumentObjectGroupPython] G4_POLYVINYL_CHLORIDE  # scripted group (container) (typed FeaturePython)
  Dunit = g/cm3
  Dvalue = 1.3
  Group = -> [C_element092,H_element084,Cl_element019]
  conduct = 2
  density = 1
  expand = 3
  formula = G4_POLYVINYL_CHLORIDE
  name = G4_POLYVINYL_CHLORIDE
  specific = 4
FEATURE [App::DocumentObjectGroupPython] C_element093  label="C_element : 051"  # scripted group (container) (typed FeaturePython)
  n = 2
  ref = C_element
FEATURE [App::DocumentObjectGroupPython] H_element085  label="H_element : 047"  # scripted group (container) (typed FeaturePython)
  n = 2
  ref = H_element
FEATURE [App::DocumentObjectGroupPython] Cl_element020  label="Cl_element : 010"  # scripted group (container) (typed FeaturePython)
  n = 2
  ref = Cl_element
FEATURE [App::DocumentObjectGroupPython] G4_POLYVINYLIDENE_CHLORIDE  # scripted group (container) (typed FeaturePython)
  Dunit = g/cm3
  Dvalue = 1.7
  Group = -> [C_element093,H_element085,Cl_element020]
  conduct = 2
  density = 1
  expand = 3
  formula = G4_POLYVINYLIDENE_CHLORIDE
  name = G4_POLYVINYLIDENE_CHLORIDE
  specific = 4
FEATURE [App::DocumentObjectGroupPython] C_element094  label="C_element : 052"  # scripted group (container) (typed FeaturePython)
  n = 2
  ref = C_element
FEATURE [App::DocumentObjectGroupPython] H_element086  label="H_element : 048"  # scripted group (container) (typed FeaturePython)
  n = 2
  ref = H_element
FEATURE [App::DocumentObjectGroupPython] F_element016  label="F_element : 007"  # scripted group (container) (typed FeaturePython)
  n = 2
  ref = F_element
FEATURE [App::DocumentObjectGroupPython] G4_POLYVINYLIDENE_FLUORIDE  # scripted group (container) (typed FeaturePython)
  Dunit = g/cm3
  Dvalue = 1.76
  Group = -> [C_element094,H_element086,F_element016]
  conduct = 2
  density = 1
  expand = 3
  formula = G4_POLYVINYLIDENE_FLUORIDE
  name = G4_POLYVINYLIDENE_FLUORIDE
  specific = 4
FEATURE [App::DocumentObjectGroupPython] C_element095  label="C_element : 053"  # scripted group (container) (typed FeaturePython)
  n = 6
  ref = C_element
FEATURE [App::DocumentObjectGroupPython] H_element087  label="H_element : 9"  # scripted group (container) (typed FeaturePython)
  n = 9
  ref = H_element
FEATURE [App::DocumentObjectGroupPython] N_element037  label="N_element : 016"  # scripted group (container) (typed FeaturePython)
  n = 1
  ref = N_element
FEATURE [App::DocumentObjectGroupPython] O_element084  label="O_element : 045"  # scripted group (container) (typed FeaturePython)
  n = 1
  ref = O_element
FEATURE [App::DocumentObjectGroupPython] G4_POLYVINYL_PYRROLIDONE  # scripted group (container) (typed FeaturePython)
  Dunit = g/cm3
  Dvalue = 1.25
  Group = -> [C_element095,H_element087,N_element037,O_element084]
  conduct = 2
  density = 1
  expand = 3
  formula = G4_POLYVINYL_PYRROLIDONE
  name = G4_POLYVINYL_PYRROLIDONE
  specific = 4
FEATURE [App::DocumentObjectGroupPython] K_element008  label="K_element : 1"  # scripted group (container) (typed FeaturePython)
  n = 1
  ref = K_element
FEATURE [App::DocumentObjectGroupPython] I_element006  label="I_element : 003"  # scripted group (container) (typed FeaturePython)
  n = 1
  ref = I_element
FEATURE [App::DocumentObjectGroupPython] G4_POTASSIUM_IODIDE  # scripted group (container) (typed FeaturePython)
  Dunit = g/cm3
  Dvalue = 3.13
  Group = -> [K_element008,I_element006]
  conduct = 2
  density = 1
  expand = 3
  formula = G4_POTASSIUM_IODIDE
  name = G4_POTASSIUM_IODIDE
  specific = 4
FEATURE [App::DocumentObjectGroupPython] K_element009  label="K_element : 2"  # scripted group (container) (typed FeaturePython)
  n = 2
  ref = K_element
FEATURE [App::DocumentObjectGroupPython] O_element085  label="O_element : 046"  # scripted group (container) (typed FeaturePython)
  n = 1
  ref = O_element
FEATURE [App::DocumentObjectGroupPython] G4_POTASSIUM_OXIDE  # scripted group (container) (typed FeaturePython)
  Dunit = g/cm3
  Dvalue = 2.32
  Group = -> [K_element009,O_element085]
  conduct = 2
  density = 1
  expand = 3
  formula = G4_POTASSIUM_OXIDE
  name = G4_POTASSIUM_OXIDE
  specific = 4
FEATURE [App::DocumentObjectGroupPython] C_element096  label="C_element : 054"  # scripted group (container) (typed FeaturePython)
  n = 3
  ref = C_element
FEATURE [App::DocumentObjectGroupPython] H_element088  label="H_element : 049"  # scripted group (container) (typed FeaturePython)
  n = 8
  ref = H_element
FEATURE [App::DocumentObjectGroupPython] G4_PROPANE  # scripted group (container) (typed FeaturePython)
  Dunit = g/cm3
  Dvalue = 0.00187939
  Group = -> [C_element096,H_element088]
  conduct = 2
  density = 1
  expand = 3
  formula = G4_PROPANE
  name = G4_PROPANE
  specific = 4
FEATURE [App::DocumentObjectGroupPython] C_element097  label="C_element : 055"  # scripted group (container) (typed FeaturePython)
  n = 3
  ref = C_element
FEATURE [App::DocumentObjectGroupPython] H_element089  label="H_element : 050"  # scripted group (container) (typed FeaturePython)
  n = 8
  ref = H_element
FEATURE [App::DocumentObjectGroupPython] G4_lPROPANE  # scripted group (container) (typed FeaturePython)
  Dunit = g/cm3
  Dvalue = 0.43
  Group = -> [C_element097,H_element089]
  conduct = 2
  density = 1
  expand = 3
  formula = G4_lPROPANE
  name = G4_lPROPANE
  specific = 4
FEATURE [App::DocumentObjectGroupPython] C_element098  label="C_element : 056"  # scripted group (container) (typed FeaturePython)
  n = 3
  ref = C_element
FEATURE [App::DocumentObjectGroupPython] H_element090  label="H_element : 051"  # scripted group (container) (typed FeaturePython)
  n = 8
  ref = H_element
FEATURE [App::DocumentObjectGroupPython] O_element086  label="O_element : 047"  # scripted group (container) (typed FeaturePython)
  n = 1
  ref = O_element
FEATURE [App::DocumentObjectGroupPython] G4_N_PROPYL_ALCOHOL  label="G4_N-PROPYL_ALCOHOL"  # scripted group (container) (typed FeaturePython)
  Dunit = g/cm3
  Dvalue = 0.8035
  Group = -> [C_element098,H_element090,O_element086]
  conduct = 2
  density = 1
  expand = 3
  formula = G4_N-PROPYL_ALCOHOL
  name = G4_N-PROPYL_ALCOHOL
  specific = 4
FEATURE [App::DocumentObjectGroupPython] C_element099  label="C_element : 057"  # scripted group (container) (typed FeaturePython)
  n = 5
  ref = C_element
FEATURE [App::DocumentObjectGroupPython] H_element091  label="H_element : 052"  # scripted group (container) (typed FeaturePython)
  n = 5
  ref = H_element
FEATURE [App::DocumentObjectGroupPython] N_element038  label="N_element : 017"  # scripted group (container) (typed FeaturePython)
  n = 1
  ref = N_element
FEATURE [App::DocumentObjectGroupPython] G4_PYRIDINE  # scripted group (container) (typed FeaturePython)
  Dunit = g/cm3
  Dvalue = 0.9819
  Group = -> [C_element099,H_element091,N_element038]
  conduct = 2
  density = 1
  expand = 3
  formula = G4_PYRIDINE
  name = G4_PYRIDINE
  specific = 4
FEATURE [App::DocumentObjectGroupPython] H_element092  label="H_element : 0.144"  # scripted group (container) (typed FeaturePython)
  n = 0.143711
FEATURE [App::DocumentObjectGroupPython] C_element100  label="C_element : 0.856"  # scripted group (container) (typed FeaturePython)
  n = 0.856289
FEATURE [App::DocumentObjectGroupPython] G4_RUBBER_BUTYL  # scripted group (container) (typed FeaturePython)
  Dunit = g/cm3
  Dvalue = 0.92
  Group = -> [H_element092,C_element100]
  conduct = 2
  density = 1
  expand = 3
  formula = G4_RUBBER_BUTYL
  name = G4_RUBBER_BUTYL
  specific = 4
FEATURE [App::DocumentObjectGroupPython] H_element093  label="H_element : 0.118"  # scripted group (container) (typed FeaturePython)
  n = 0.118371
FEATURE [App::DocumentObjectGroupPython] C_element101  label="C_element : 0.882"  # scripted group (container) (typed FeaturePython)
  n = 0.881629
FEATURE [App::DocumentObjectGroupPython] G4_RUBBER_NATURAL  # scripted group (container) (typed FeaturePython)
  Dunit = g/cm3
  Dvalue = 0.92
  Group = -> [H_element093,C_element101]
  conduct = 2
  density = 1
  expand = 3
  formula = G4_RUBBER_NATURAL
  name = G4_RUBBER_NATURAL
  specific = 4
FEATURE [App::DocumentObjectGroupPython] H_element094  label="H_element : 0.145"  # scripted group (container) (typed FeaturePython)
  n = 0.05692
FEATURE [App::DocumentObjectGroupPython] C_element102  label="C_element : 0.543"  # scripted group (container) (typed FeaturePython)
  n = 0.542646
FEATURE [App::DocumentObjectGroupPython] Cl_element021  label="Cl_element : 0.400"  # scripted group (container) (typed FeaturePython)
  n = 0.400434
FEATURE [App::DocumentObjectGroupPython] G4_RUBBER_NEOPRENE  # scripted group (container) (typed FeaturePython)
  Dunit = g/cm3
  Dvalue = 1.23
  Group = -> [H_element094,C_element102,Cl_element021]
  conduct = 2
  density = 1
  expand = 3
  formula = G4_RUBBER_NEOPRENE
  name = G4_RUBBER_NEOPRENE
  specific = 4
FEATURE [App::DocumentObjectGroupPython] Si_element006  label="Si_element : 1"  # scripted group (container) (typed FeaturePython)
  n = 1
  ref = Si_element
FEATURE [App::DocumentObjectGroupPython] O_element087  label="O_element : 048"  # scripted group (container) (typed FeaturePython)
  n = 2
  ref = O_element
FEATURE [App::DocumentObjectGroupPython] G4_SILICON_DIOXIDE  # scripted group (container) (typed FeaturePython)
  Dunit = g/cm3
  Dvalue = 2.32
  Group = -> [Si_element006,O_element087]
  conduct = 2
  density = 1
  expand = 3
  formula = G4_SILICON_DIOXIDE
  name = G4_SILICON_DIOXIDE
  specific = 4
FEATURE [App::DocumentObjectGroupPython] Ag_element002  label="Ag_element : 1"  # scripted group (container) (typed FeaturePython)
  n = 1
  ref = Ag_element
FEATURE [App::DocumentObjectGroupPython] Br_element005  label="Br_element : 003"  # scripted group (container) (typed FeaturePython)
  n = 1
  ref = Br_element
FEATURE [App::DocumentObjectGroupPython] G4_SILVER_BROMIDE  # scripted group (container) (typed FeaturePython)
  Dunit = g/cm3
  Dvalue = 6.473
  Group = -> [Ag_element002,Br_element005]
  conduct = 2
  density = 1
  expand = 3
  formula = G4_SILVER_BROMIDE
  name = G4_SILVER_BROMIDE
  specific = 4
FEATURE [App::DocumentObjectGroupPython] Ag_element003  label="Ag_element : 002"  # scripted group (container) (typed FeaturePython)
  n = 1
  ref = Ag_element
FEATURE [App::DocumentObjectGroupPython] Cl_element022  label="Cl_element : 011"  # scripted group (container) (typed FeaturePython)
  n = 1
  ref = Cl_element
FEATURE [App::DocumentObjectGroupPython] G4_SILVER_CHLORIDE  # scripted group (container) (typed FeaturePython)
  Dunit = g/cm3
  Dvalue = 5.56
  Group = -> [Ag_element003,Cl_element022]
  conduct = 2
  density = 1
  expand = 3
  formula = G4_SILVER_CHLORIDE
  name = G4_SILVER_CHLORIDE
  specific = 4
FEATURE [App::DocumentObjectGroupPython] Br_element006  label="Br_element : 0.423"  # scripted group (container) (typed FeaturePython)
  n = 0.422895
FEATURE [App::DocumentObjectGroupPython] Ag_element004  label="Ag_element : 0.574"  # scripted group (container) (typed FeaturePython)
  n = 0.573748
FEATURE [App::DocumentObjectGroupPython] I_element007  label="I_element : 0.649"  # scripted group (container) (typed FeaturePython)
  n = 0.003357
FEATURE [App::DocumentObjectGroupPython] G4_SILVER_HALIDES  # scripted group (container) (typed FeaturePython)
  Dunit = g/cm3
  Dvalue = 6.47
  Group = -> [Br_element006,Ag_element004,I_element007]
  conduct = 2
  density = 1
  expand = 3
  formula = G4_SILVER_HALIDES
  name = G4_SILVER_HALIDES
  specific = 4
FEATURE [App::DocumentObjectGroupPython] Ag_element005  label="Ag_element : 003"  # scripted group (container) (typed FeaturePython)
  n = 1
  ref = Ag_element
FEATURE [App::DocumentObjectGroupPython] I_element008  label="I_element : 004"  # scripted group (container) (typed FeaturePython)
  n = 1
  ref = I_element
FEATURE [App::DocumentObjectGroupPython] G4_SILVER_IODIDE  # scripted group (container) (typed FeaturePython)
  Dunit = g/cm3
  Dvalue = 6.01
  Group = -> [Ag_element005,I_element008]
  conduct = 2
  density = 1
  expand = 3
  formula = G4_SILVER_IODIDE
  name = G4_SILVER_IODIDE
  specific = 4
FEATURE [App::DocumentObjectGroupPython] H_element095  label="H_element : 0.100"  # scripted group (container) (typed FeaturePython)
  n = 0.1
FEATURE [App::DocumentObjectGroupPython] C_element103  label="C_element : 0.204"  # scripted group (container) (typed FeaturePython)
  n = 0.204
FEATURE [App::DocumentObjectGroupPython] N_element039  label="N_element : 0.759"  # scripted group (container) (typed FeaturePython)
  n = 0.042
FEATURE [App::DocumentObjectGroupPython] O_element088  label="O_element : 0.645"  # scripted group (container) (typed FeaturePython)
  n = 0.645
FEATURE [App::DocumentObjectGroupPython] Na_element013  label="Na_element : 0.100"  # scripted group (container) (typed FeaturePython)
  n = 0.002
FEATURE [App::DocumentObjectGroupPython] P_element009  label="P_element : 0.107"  # scripted group (container) (typed FeaturePython)
  n = 0.001
FEATURE [App::DocumentObjectGroupPython] S_element020  label="S_element : 0.021"  # scripted group (container) (typed FeaturePython)
  n = 0.002
FEATURE [App::DocumentObjectGroupPython] Cl_element023  label="Cl_element : 0.590"  # scripted group (container) (typed FeaturePython)
  n = 0.003
FEATURE [App::DocumentObjectGroupPython] K_element010  label="K_element : 0.001"  # scripted group (container) (typed FeaturePython)
  n = 0.001
FEATURE [App::DocumentObjectGroupPython] G4_SKIN_ICRP  # scripted group (container) (typed FeaturePython)
  Dunit = g/cm3
  Dvalue = 1.09
  Group = -> [H_element095,C_element103,N_element039,O_element088,Na_element013,P_element009,S_element020,Cl_element023,K_element010]
  conduct = 2
  density = 1
  expand = 3
  formula = G4_SKIN_ICRP
  name = G4_SKIN_ICRP
  specific = 4
FEATURE [App::DocumentObjectGroupPython] Na_element014  label="Na_element : 2"  # scripted group (container) (typed FeaturePython)
  n = 2
  ref = Na_element
FEATURE [App::DocumentObjectGroupPython] C_element104  label="C_element : 058"  # scripted group (container) (typed FeaturePython)
  n = 1
  ref = C_element
FEATURE [App::DocumentObjectGroupPython] O_element089  label="O_element : 049"  # scripted group (container) (typed FeaturePython)
  n = 3
  ref = O_element
FEATURE [App::DocumentObjectGroupPython] G4_SODIUM_CARBONATE  # scripted group (container) (typed FeaturePython)
  Dunit = g/cm3
  Dvalue = 2.532
  Group = -> [Na_element014,C_element104,O_element089]
  conduct = 2
  density = 1
  expand = 3
  formula = G4_SODIUM_CARBONATE
  name = G4_SODIUM_CARBONATE
  specific = 4
FEATURE [App::DocumentObjectGroupPython] Na_element015  label="Na_element : 1"  # scripted group (container) (typed FeaturePython)
  n = 1
  ref = Na_element
FEATURE [App::DocumentObjectGroupPython] I_element009  label="I_element : 005"  # scripted group (container) (typed FeaturePython)
  n = 1
  ref = I_element
FEATURE [App::DocumentObjectGroupPython] G4_SODIUM_IODIDE  # scripted group (container) (typed FeaturePython)
  Dunit = g/cm3
  Dvalue = 3.667
  Group = -> [Na_element015,I_element009]
  conduct = 2
  density = 1
  expand = 3
  formula = G4_SODIUM_IODIDE
  name = G4_SODIUM_IODIDE
  specific = 4
FEATURE [App::DocumentObjectGroupPython] Na_element016  label="Na_element : 003"  # scripted group (container) (typed FeaturePython)
  n = 2
  ref = Na_element
FEATURE [App::DocumentObjectGroupPython] O_element090  label="O_element : 050"  # scripted group (container) (typed FeaturePython)
  n = 1
  ref = O_element
FEATURE [App::DocumentObjectGroupPython] G4_SODIUM_MONOXIDE  # scripted group (container) (typed FeaturePython)
  Dunit = g/cm3
  Dvalue = 2.27
  Group = -> [Na_element016,O_element090]
  conduct = 2
  density = 1
  expand = 3
  formula = G4_SODIUM_MONOXIDE
  name = G4_SODIUM_MONOXIDE
  specific = 4
FEATURE [App::DocumentObjectGroupPython] Na_element017  label="Na_element : 004"  # scripted group (container) (typed FeaturePython)
  n = 1
  ref = Na_element
FEATURE [App::DocumentObjectGroupPython] N_element040  label="N_element : 018"  # scripted group (container) (typed FeaturePython)
  n = 1
  ref = N_element
FEATURE [App::DocumentObjectGroupPython] O_element091  label="O_element : 051"  # scripted group (container) (typed FeaturePython)
  n = 3
  ref = O_element
FEATURE [App::DocumentObjectGroupPython] G4_SODIUM_NITRATE  # scripted group (container) (typed FeaturePython)
  Dunit = g/cm3
  Dvalue = 2.261
  Group = -> [Na_element017,N_element040,O_element091]
  conduct = 2
  density = 1
  expand = 3
  formula = G4_SODIUM_NITRATE
  name = G4_SODIUM_NITRATE
  specific = 4
FEATURE [App::DocumentObjectGroupPython] C_element105  label="C_element : 059"  # scripted group (container) (typed FeaturePython)
  n = 14
  ref = C_element
FEATURE [App::DocumentObjectGroupPython] H_element096  label="H_element : 053"  # scripted group (container) (typed FeaturePython)
  n = 12
  ref = H_element
FEATURE [App::DocumentObjectGroupPython] G4_STILBENE  # scripted group (container) (typed FeaturePython)
  Dunit = g/cm3
  Dvalue = 0.9707
  Group = -> [C_element105,H_element096]
  conduct = 2
  density = 1
  expand = 3
  formula = G4_STILBENE
  name = G4_STILBENE
  specific = 4
FEATURE [App::DocumentObjectGroupPython] C_element106  label="C_element : 12"  # scripted group (container) (typed FeaturePython)
  n = 12
  ref = C_element
FEATURE [App::DocumentObjectGroupPython] H_element097  label="H_element : 22"  # scripted group (container) (typed FeaturePython)
  n = 22
  ref = H_element
FEATURE [App::DocumentObjectGroupPython] O_element092  label="O_element : 11"  # scripted group (container) (typed FeaturePython)
  n = 11
  ref = O_element
FEATURE [App::DocumentObjectGroupPython] G4_SUCROSE  # scripted group (container) (typed FeaturePython)
  Dunit = g/cm3
  Dvalue = 1.5805
  Group = -> [C_element106,H_element097,O_element092]
  conduct = 2
  density = 1
  expand = 3
  formula = G4_SUCROSE
  name = G4_SUCROSE
  specific = 4
FEATURE [App::DocumentObjectGroupPython] C_element107  label="C_element : 18"  # scripted group (container) (typed FeaturePython)
  n = 18
  ref = C_element
FEATURE [App::DocumentObjectGroupPython] H_element098  label="H_element : 054"  # scripted group (container) (typed FeaturePython)
  n = 14
  ref = H_element
FEATURE [App::DocumentObjectGroupPython] G4_TERPHENYL  # scripted group (container) (typed FeaturePython)
  Dunit = g/cm3
  Dvalue = 1.24
  Group = -> [C_element107,H_element098]
  conduct = 2
  density = 1
  expand = 3
  formula = G4_TERPHENYL
  name = G4_TERPHENYL
  specific = 4
FEATURE [App::DocumentObjectGroupPython] H_element099  label="H_element : 0.146"  # scripted group (container) (typed FeaturePython)
  n = 0.106
FEATURE [App::DocumentObjectGroupPython] C_element108  label="C_element : 0.883"  # scripted group (container) (typed FeaturePython)
  n = 0.099
FEATURE [App::DocumentObjectGroupPython] N_element041  label="N_element : 0.020"  # scripted group (container) (typed FeaturePython)
  n = 0.02
FEATURE [App::DocumentObjectGroupPython] O_element093  label="O_element : 0.766"  # scripted group (container) (typed FeaturePython)
  n = 0.766
FEATURE [App::DocumentObjectGroupPython] Na_element018  label="Na_element : 0.101"  # scripted group (container) (typed FeaturePython)
  n = 0.002
FEATURE [App::DocumentObjectGroupPython] P_element010  label="P_element : 0.108"  # scripted group (container) (typed FeaturePython)
  n = 0.001
FEATURE [App::DocumentObjectGroupPython] S_element021  label="S_element : 0.022"  # scripted group (container) (typed FeaturePython)
  n = 0.002
FEATURE [App::DocumentObjectGroupPython] Cl_element024  label="Cl_element : 0.002"  # scripted group (container) (typed FeaturePython)
  n = 0.002
FEATURE [App::DocumentObjectGroupPython] K_element011  label="K_element : 0.017"  # scripted group (container) (typed FeaturePython)
  n = 0.002
FEATURE [App::DocumentObjectGroupPython] G4_TESTIS_ICRP  # scripted group (container) (typed FeaturePython)
  Dunit = g/cm3
  Dvalue = 1.04
  Group = -> [H_element099,C_element108,N_element041,O_element093,Na_element018,P_element010,S_element021,Cl_element024,K_element011]
  conduct = 2
  density = 1
  expand = 3
  formula = G4_TESTIS_ICRP
  name = G4_TESTIS_ICRP
  specific = 4
FEATURE [App::DocumentObjectGroupPython] C_element109  label="C_element : 060"  # scripted group (container) (typed FeaturePython)
  n = 2
  ref = C_element
FEATURE [App::DocumentObjectGroupPython] Cl_element025  label="Cl_element : 012"  # scripted group (container) (typed FeaturePython)
  n = 4
  ref = Cl_element
FEATURE [App::DocumentObjectGroupPython] G4_TETRACHLOROETHYLENE  # scripted group (container) (typed FeaturePython)
  Dunit = g/cm3
  Dvalue = 1.625
  Group = -> [C_element109,Cl_element025]
  conduct = 2
  density = 1
  expand = 3
  formula = G4_TETRACHLOROETHYLENE
  name = G4_TETRACHLOROETHYLENE
  specific = 4
FEATURE [App::DocumentObjectGroupPython] Tl_element001  label="Tl_element : 1"  # scripted group (container) (typed FeaturePython)
  n = 1
  ref = Tl_element
FEATURE [App::DocumentObjectGroupPython] Cl_element026  label="Cl_element : 013"  # scripted group (container) (typed FeaturePython)
  n = 1
  ref = Cl_element
FEATURE [App::DocumentObjectGroupPython] G4_THALLIUM_CHLORIDE  # scripted group (container) (typed FeaturePython)
  Dunit = g/cm3
  Dvalue = 7.004
  Group = -> [Tl_element001,Cl_element026]
  conduct = 2
  density = 1
  expand = 3
  formula = G4_THALLIUM_CHLORIDE
  name = G4_THALLIUM_CHLORIDE
  specific = 4
FEATURE [App::DocumentObjectGroupPython] H_element100  label="H_element : 0.147"  # scripted group (container) (typed FeaturePython)
  n = 0.105
FEATURE [App::DocumentObjectGroupPython] C_element110  label="C_element : 0.256"  # scripted group (container) (typed FeaturePython)
  n = 0.256
FEATURE [App::DocumentObjectGroupPython] N_element042  label="N_element : 0.760"  # scripted group (container) (typed FeaturePython)
  n = 0.027
FEATURE [App::DocumentObjectGroupPython] O_element094  label="O_element : 0.602"  # scripted group (container) (typed FeaturePython)
  n = 0.602
FEATURE [App::DocumentObjectGroupPython] Na_element019  label="Na_element : 0.102"  # scripted group (container) (typed FeaturePython)
  n = 0.001
FEATURE [App::DocumentObjectGroupPython] P_element011  label="P_element : 0.109"  # scripted group (container) (typed FeaturePython)
  n = 0.002
FEATURE [App::DocumentObjectGroupPython] S_element022  label="S_element : 0.023"  # scripted group (container) (typed FeaturePython)
  n = 0.003
FEATURE [App::DocumentObjectGroupPython] Cl_element027  label="Cl_element : 0.591"  # scripted group (container) (typed FeaturePython)
  n = 0.002
FEATURE [App::DocumentObjectGroupPython] K_element012  label="K_element : 0.018"  # scripted group (container) (typed FeaturePython)
  n = 0.002
FEATURE [App::DocumentObjectGroupPython] G4_TISSUE_SOFT_ICRP  # scripted group (container) (typed FeaturePython)
  Dunit = g/cm3
  Dvalue = 1.03
  Group = -> [H_element100,C_element110,N_element042,O_element094,Na_element019,P_element011,S_element022,Cl_element027,K_element012]
  conduct = 2
  density = 1
  expand = 3
  formula = G4_TISSUE_SOFT_ICRP
  name = G4_TISSUE_SOFT_ICRP
  specific = 4
FEATURE [App::DocumentObjectGroupPython] H_element101  label="H_element : 0.148"  # scripted group (container) (typed FeaturePython)
  n = 0.101
FEATURE [App::DocumentObjectGroupPython] C_element111  label="C_element : 0.111"  # scripted group (container) (typed FeaturePython)
  n = 0.111
FEATURE [App::DocumentObjectGroupPython] N_element043  label="N_element : 0.026"  # scripted group (container) (typed FeaturePython)
  n = 0.026
FEATURE [App::DocumentObjectGroupPython] O_element095  label="O_element : 0.762"  # scripted group (container) (typed FeaturePython)
  n = 0.762
FEATURE [App::DocumentObjectGroupPython] G4_TISSUE_SOFT_ICRU_4  label="G4_TISSUE_SOFT_ICRU-4"  # scripted group (container) (typed FeaturePython)
  Dunit = g/cm3
  Dvalue = 1
  Group = -> [H_element101,C_element111,N_element043,O_element095]
  conduct = 2
  density = 1
  expand = 3
  formula = G4_TISSUE_SOFT_ICRU-4
  name = G4_TISSUE_SOFT_ICRU-4
  specific = 4
FEATURE [App::DocumentObjectGroupPython] H_element102  label="H_element : 0.149"  # scripted group (container) (typed FeaturePython)
  n = 0.101869
FEATURE [App::DocumentObjectGroupPython] C_element112  label="C_element : 0.456"  # scripted group (container) (typed FeaturePython)
  n = 0.456179
FEATURE [App::DocumentObjectGroupPython] N_element044  label="N_element : 0.761"  # scripted group (container) (typed FeaturePython)
  n = 0.035172
FEATURE [App::DocumentObjectGroupPython] O_element096  label="O_element : 0.407"  # scripted group (container) (typed FeaturePython)
  n = 0.40678
FEATURE [App::DocumentObjectGroupPython] G4_TISSUE_METHANE  label="G4_TISSUE-METHANE"  # scripted group (container) (typed FeaturePython)
  Dunit = g/cm3
  Dvalue = 0.00106409
  Group = -> [H_element102,C_element112,N_element044,O_element096]
  conduct = 2
  density = 1
  expand = 3
  formula = G4_TISSUE-METHANE
  name = G4_TISSUE-METHANE
  specific = 4
FEATURE [App::DocumentObjectGroupPython] H_element103  label="H_element : 0.103"  # scripted group (container) (typed FeaturePython)
  n = 0.102672
FEATURE [App::DocumentObjectGroupPython] C_element113  label="C_element : 0.569"  # scripted group (container) (typed FeaturePython)
  n = 0.56894
FEATURE [App::DocumentObjectGroupPython] N_element045  label="N_element : 0.762"  # scripted group (container) (typed FeaturePython)
  n = 0.035022
FEATURE [App::DocumentObjectGroupPython] O_element097  label="O_element : 0.293"  # scripted group (container) (typed FeaturePython)
  n = 0.293366
FEATURE [App::DocumentObjectGroupPython] G4_TISSUE_PROPANE  label="G4_TISSUE-PROPANE"  # scripted group (container) (typed FeaturePython)
  Dunit = g/cm3
  Dvalue = 0.00182628
  Group = -> [H_element103,C_element113,N_element045,O_element097]
  conduct = 2
  density = 1
  expand = 3
  formula = G4_TISSUE-PROPANE
  name = G4_TISSUE-PROPANE
  specific = 4
FEATURE [App::DocumentObjectGroupPython] Ti_element003  label="Ti_element : 1"  # scripted group (container) (typed FeaturePython)
  n = 1
  ref = Ti_element
FEATURE [App::DocumentObjectGroupPython] O_element098  label="O_element : 052"  # scripted group (container) (typed FeaturePython)
  n = 2
  ref = O_element
FEATURE [App::DocumentObjectGroupPython] G4_TITANIUM_DIOXIDE  # scripted group (container) (typed FeaturePython)
  Dunit = g/cm3
  Dvalue = 4.26
  Group = -> [Ti_element003,O_element098]
  conduct = 2
  density = 1
  expand = 3
  formula = G4_TITANIUM_DIOXIDE
  name = G4_TITANIUM_DIOXIDE
  specific = 4
FEATURE [App::DocumentObjectGroupPython] C_element114  label="C_element : 061"  # scripted group (container) (typed FeaturePython)
  n = 7
  ref = C_element
FEATURE [App::DocumentObjectGroupPython] H_element104  label="H_element : 055"  # scripted group (container) (typed FeaturePython)
  n = 8
  ref = H_element
FEATURE [App::DocumentObjectGroupPython] G4_TOLUENE  # scripted group (container) (typed FeaturePython)
  Dunit = g/cm3
  Dvalue = 0.8669
  Group = -> [C_element114,H_element104]
  conduct = 2
  density = 1
  expand = 3
  formula = G4_TOLUENE
  name = G4_TOLUENE
  specific = 4
FEATURE [App::DocumentObjectGroupPython] C_element115  label="C_element : 062"  # scripted group (container) (typed FeaturePython)
  n = 2
  ref = C_element
FEATURE [App::DocumentObjectGroupPython] H_element105  label="H_element : 056"  # scripted group (container) (typed FeaturePython)
  n = 1
  ref = H_element
FEATURE [App::DocumentObjectGroupPython] Cl_element028  label="Cl_element : 014"  # scripted group (container) (typed FeaturePython)
  n = 3
  ref = Cl_element
FEATURE [App::DocumentObjectGroupPython] G4_TRICHLOROETHYLENE  # scripted group (container) (typed FeaturePython)
  Dunit = g/cm3
  Dvalue = 1.46
  Group = -> [C_element115,H_element105,Cl_element028]
  conduct = 2
  density = 1
  expand = 3
  formula = G4_TRICHLOROETHYLENE
  name = G4_TRICHLOROETHYLENE
  specific = 4
FEATURE [App::DocumentObjectGroupPython] C_element116  label="C_element : 063"  # scripted group (container) (typed FeaturePython)
  n = 6
  ref = C_element
FEATURE [App::DocumentObjectGroupPython] H_element106  label="H_element : 15"  # scripted group (container) (typed FeaturePython)
  n = 15
  ref = H_element
FEATURE [App::DocumentObjectGroupPython] O_element099  label="O_element : 053"  # scripted group (container) (typed FeaturePython)
  n = 4
  ref = O_element
FEATURE [App::DocumentObjectGroupPython] P_element012  label="P_element : 1"  # scripted group (container) (typed FeaturePython)
  n = 1
  ref = P_element
FEATURE [App::DocumentObjectGroupPython] G4_TRIETHYL_PHOSPHATE  # scripted group (container) (typed FeaturePython)
  Dunit = g/cm3
  Dvalue = 1.07
  Group = -> [C_element116,H_element106,O_element099,P_element012]
  conduct = 2
  density = 1
  expand = 3
  formula = G4_TRIETHYL_PHOSPHATE
  name = G4_TRIETHYL_PHOSPHATE
  specific = 4
FEATURE [App::DocumentObjectGroupPython] W_element003  label="W_element : 003"  # scripted group (container) (typed FeaturePython)
  n = 1
  ref = W_element
FEATURE [App::DocumentObjectGroupPython] F_element017  label="F_element : 6"  # scripted group (container) (typed FeaturePython)
  n = 6
  ref = F_element
FEATURE [App::DocumentObjectGroupPython] G4_TUNGSTEN_HEXAFLUORIDE  # scripted group (container) (typed FeaturePython)
  Dunit = g/cm3
  Dvalue = 2.4
  Group = -> [W_element003,F_element017]
  conduct = 2
  density = 1
  expand = 3
  formula = G4_TUNGSTEN_HEXAFLUORIDE
  name = G4_TUNGSTEN_HEXAFLUORIDE
  specific = 4
FEATURE [App::DocumentObjectGroupPython] U_element001  label="U_element : 1"  # scripted group (container) (typed FeaturePython)
  n = 1
  ref = U_element
FEATURE [App::DocumentObjectGroupPython] C_element117  label="C_element : 064"  # scripted group (container) (typed FeaturePython)
  n = 2
  ref = C_element
FEATURE [App::DocumentObjectGroupPython] G4_URANIUM_DICARBIDE  # scripted group (container) (typed FeaturePython)
  Dunit = g/cm3
  Dvalue = 11.28
  Group = -> [U_element001,C_element117]
  conduct = 2
  density = 1
  expand = 3
  formula = G4_URANIUM_DICARBIDE
  name = G4_URANIUM_DICARBIDE
  specific = 4
FEATURE [App::DocumentObjectGroupPython] U_element002  label="U_element : 002"  # scripted group (container) (typed FeaturePython)
  n = 1
  ref = U_element
FEATURE [App::DocumentObjectGroupPython] C_element118  label="C_element : 065"  # scripted group (container) (typed FeaturePython)
  n = 1
  ref = C_element
FEATURE [App::DocumentObjectGroupPython] G4_URANIUM_MONOCARBIDE  # scripted group (container) (typed FeaturePython)
  Dunit = g/cm3
  Dvalue = 13.63
  Group = -> [U_element002,C_element118]
  conduct = 2
  density = 1
  expand = 3
  formula = G4_URANIUM_MONOCARBIDE
  name = G4_URANIUM_MONOCARBIDE
  specific = 4
FEATURE [App::DocumentObjectGroupPython] U_element003  label="U_element : 003"  # scripted group (container) (typed FeaturePython)
  n = 1
  ref = U_element
FEATURE [App::DocumentObjectGroupPython] O_element100  label="O_element : 054"  # scripted group (container) (typed FeaturePython)
  n = 2
  ref = O_element
FEATURE [App::DocumentObjectGroupPython] G4_URANIUM_OXIDE  # scripted group (container) (typed FeaturePython)
  Dunit = g/cm3
  Dvalue = 10.96
  Group = -> [U_element003,O_element100]
  conduct = 2
  density = 1
  expand = 3
  formula = G4_URANIUM_OXIDE
  name = G4_URANIUM_OXIDE
  specific = 4
FEATURE [App::DocumentObjectGroupPython] C_element119  label="C_element : 066"  # scripted group (container) (typed FeaturePython)
  n = 1
  ref = C_element
FEATURE [App::DocumentObjectGroupPython] H_element107  label="H_element : 057"  # scripted group (container) (typed FeaturePython)
  n = 4
  ref = H_element
FEATURE [App::DocumentObjectGroupPython] N_element046  label="N_element : 019"  # scripted group (container) (typed FeaturePython)
  n = 2
  ref = N_element
FEATURE [App::DocumentObjectGroupPython] O_element101  label="O_element : 055"  # scripted group (container) (typed FeaturePython)
  n = 1
  ref = O_element
FEATURE [App::DocumentObjectGroupPython] G4_UREA  # scripted group (container) (typed FeaturePython)
  Dunit = g/cm3
  Dvalue = 1.323
  Group = -> [C_element119,H_element107,N_element046,O_element101]
  conduct = 2
  density = 1
  expand = 3
  formula = G4_UREA
  name = G4_UREA
  specific = 4
FEATURE [App::DocumentObjectGroupPython] C_element120  label="C_element : 067"  # scripted group (container) (typed FeaturePython)
  n = 5
  ref = C_element
FEATURE [App::DocumentObjectGroupPython] H_element108  label="H_element : 058"  # scripted group (container) (typed FeaturePython)
  n = 11
  ref = H_element
FEATURE [App::DocumentObjectGroupPython] N_element047  label="N_element : 020"  # scripted group (container) (typed FeaturePython)
  n = 1
  ref = N_element
FEATURE [App::DocumentObjectGroupPython] O_element102  label="O_element : 056"  # scripted group (container) (typed FeaturePython)
  n = 2
  ref = O_element
FEATURE [App::DocumentObjectGroupPython] G4_VALINE  # scripted group (container) (typed FeaturePython)
  Dunit = g/cm3
  Dvalue = 1.23
  Group = -> [C_element120,H_element108,N_element047,O_element102]
  conduct = 2
  density = 1
  expand = 3
  formula = G4_VALINE
  name = G4_VALINE
  specific = 4
FEATURE [App::DocumentObjectGroupPython] H_element109  label="H_element : 0.009"  # scripted group (container) (typed FeaturePython)
  n = 0.009417
FEATURE [App::DocumentObjectGroupPython] C_element121  label="C_element : 0.281"  # scripted group (container) (typed FeaturePython)
  n = 0.280555
FEATURE [App::DocumentObjectGroupPython] F_element018  label="F_element : 0.710"  # scripted group (container) (typed FeaturePython)
  n = 0.710028
FEATURE [App::DocumentObjectGroupPython] G4_VITON  # scripted group (container) (typed FeaturePython)
  Dunit = g/cm3
  Dvalue = 1.8
  Group = -> [H_element109,C_element121,F_element018]
  conduct = 2
  density = 1
  expand = 3
  formula = G4_VITON
  name = G4_VITON
  specific = 4
FEATURE [App::DocumentObjectGroupPython] H_element110  label="H_element : 059"  # scripted group (container) (typed FeaturePython)
  n = 2
  ref = H_element
FEATURE [App::DocumentObjectGroupPython] O_element103  label="O_element : 057"  # scripted group (container) (typed FeaturePython)
  n = 1
  ref = O_element
FEATURE [App::DocumentObjectGroupPython] G4_WATER  # scripted group (container) (typed FeaturePython)
  Dunit = g/cm3
  Dvalue = 1
  Group = -> [H_element110,O_element103]
  conduct = 2
  density = 1
  expand = 3
  formula = G4_WATER
  name = G4_WATER
  specific = 4
FEATURE [App::DocumentObjectGroupPython] H_element111  label="H_element : 060"  # scripted group (container) (typed FeaturePython)
  n = 2
  ref = H_element
FEATURE [App::DocumentObjectGroupPython] O_element104  label="O_element : 058"  # scripted group (container) (typed FeaturePython)
  n = 1
  ref = O_element
FEATURE [App::DocumentObjectGroupPython] G4_WATER_VAPOR  # scripted group (container) (typed FeaturePython)
  Dunit = g/cm3
  Dvalue = 0.000756182
  Group = -> [H_element111,O_element104]
  conduct = 2
  density = 1
  expand = 3
  formula = G4_WATER_VAPOR
  name = G4_WATER_VAPOR
  specific = 4
FEATURE [App::DocumentObjectGroupPython] C_element122  label="C_element : 068"  # scripted group (container) (typed FeaturePython)
  n = 8
  ref = C_element
FEATURE [App::DocumentObjectGroupPython] H_element112  label="H_element : 061"  # scripted group (container) (typed FeaturePython)
  n = 10
  ref = H_element
FEATURE [App::DocumentObjectGroupPython] G4_XYLENE  # scripted group (container) (typed FeaturePython)
  Dunit = g/cm3
  Dvalue = 0.87
  Group = -> [C_element122,H_element112]
  conduct = 2
  density = 1
  expand = 3
  formula = G4_XYLENE
  name = G4_XYLENE
  specific = 4
FEATURE [App::DocumentObjectGroupPython] C_element123  label="C_element : 069"  # scripted group (container) (typed FeaturePython)
  n = 1
  ref = C_element
FEATURE [App::DocumentObjectGroupPython] G4_GRAPHITE  # scripted group (container) (typed FeaturePython)
  Dunit = g/cm3
  Dvalue = 2.21
  Group = -> [C_element123]
  conduct = 2
  density = 1
  expand = 3
  formula = G4_GRAPHITE
  name = G4_GRAPHITE
  specific = 4
FEATURE [App::DocumentObjectGroupPython] NIST  # scripted group (container) (typed FeaturePython)
  Group = -> [G4_A_150_TISSUE,G4_ACETONE,G4_ACETYLENE,G4_ADENINE,G4_ADIPOSE_TISSUE_ICRP,G4_AIR,G4_ALANINE,G4_ALUMINUM_OXIDE,G4_AMBER,G4_AMMONIA,G4_ANILINE,G4_ANTHRACENE,G4_B_100_BONE,G4_BAKELITE,G4_BARIUM_FLUORIDE,G4_BARIUM_SULFATE,G4_BENZENE,G4_BERYLLIUM_OXIDE,G4_BGO,G4_BLOOD_ICRP,G4_BONE_COMPACT_ICRU,G4_BONE_CORTICAL_ICRP,G4_BORON_CARBIDE,G4_BORON_OXIDE,G4_BRAIN_ICRP,G4_BUTANE,G4_N_BUTYL_ALCOHOL,G4_C_552,+152 more]
FEATURE [App::DocumentObjectGroupPython] H_element113  label="H_element : 062"  # scripted group (container) (typed FeaturePython)
  n = 1
  ref = H_element
FEATURE [App::DocumentObjectGroupPython] G4_H  # scripted group (container) (typed FeaturePython)
  Dunit = g/cm3
  Dvalue = 8.3748e-05
  Group = -> [H_element113]
  conduct = 2
  density = 1
  expand = 3
  formula = H
  name = G4_H
  specific = 4
FEATURE [App::DocumentObjectGroupPython] He_element001  label="He_element : 1"  # scripted group (container) (typed FeaturePython)
  n = 1
  ref = He_element
FEATURE [App::DocumentObjectGroupPython] G4_He  # scripted group (container) (typed FeaturePython)
  Dunit = g/cm3
  Dvalue = 0.000166322
  Group = -> [He_element001]
  conduct = 2
  density = 1
  expand = 3
  formula = He
  name = G4_He
  specific = 4
FEATURE [App::DocumentObjectGroupPython] Li_element008  label="Li_element : 008"  # scripted group (container) (typed FeaturePython)
  n = 1
  ref = Li_element
FEATURE [App::DocumentObjectGroupPython] G4_Li  # scripted group (container) (typed FeaturePython)
  Dunit = g/cm3
  Dvalue = 0.534
  Group = -> [Li_element008]
  conduct = 2
  density = 1
  expand = 3
  formula = Li
  name = G4_Li
  specific = 4
FEATURE [App::DocumentObjectGroupPython] Be_element002  label="Be_element : 002"  # scripted group (container) (typed FeaturePython)
  n = 1
  ref = Be_element
FEATURE [App::DocumentObjectGroupPython] G4_Be  # scripted group (container) (typed FeaturePython)
  Dunit = g/cm3
  Dvalue = 1.848
  Group = -> [Be_element002]
  conduct = 2
  density = 1
  expand = 3
  formula = Be
  name = G4_Be
  specific = 4
FEATURE [App::DocumentObjectGroupPython] B_element007  label="B_element : 007"  # scripted group (container) (typed FeaturePython)
  n = 1
  ref = B_element
FEATURE [App::DocumentObjectGroupPython] G4_B  # scripted group (container) (typed FeaturePython)
  Dunit = g/cm3
  Dvalue = 2.37
  Group = -> [B_element007]
  conduct = 2
  density = 1
  expand = 3
  formula = B
  name = G4_B
  specific = 4
FEATURE [App::DocumentObjectGroupPython] C_element124  label="C_element : 070"  # scripted group (container) (typed FeaturePython)
  n = 1
  ref = C_element
FEATURE [App::DocumentObjectGroupPython] G4_C  # scripted group (container) (typed FeaturePython)
  Dunit = g/cm3
  Dvalue = 2
  Group = -> [C_element124]
  conduct = 2
  density = 1
  expand = 3
  formula = C
  name = G4_C
  specific = 4
FEATURE [App::DocumentObjectGroupPython] N_element048  label="N_element : 021"  # scripted group (container) (typed FeaturePython)
  n = 1
  ref = N_element
FEATURE [App::DocumentObjectGroupPython] G4_N  # scripted group (container) (typed FeaturePython)
  Dunit = g/cm3
  Dvalue = 0.0011652
  Group = -> [N_element048]
  conduct = 2
  density = 1
  expand = 3
  formula = N
  name = G4_N
  specific = 4
FEATURE [App::DocumentObjectGroupPython] O_element105  label="O_element : 059"  # scripted group (container) (typed FeaturePython)
  n = 1
  ref = O_element
FEATURE [App::DocumentObjectGroupPython] G4_O  # scripted group (container) (typed FeaturePython)
  Dunit = g/cm3
  Dvalue = 0.00133151
  Group = -> [O_element105]
  conduct = 2
  density = 1
  expand = 3
  formula = O
  name = G4_O
  specific = 4
FEATURE [App::DocumentObjectGroupPython] F_element019  label="F_element : 008"  # scripted group (container) (typed FeaturePython)
  n = 1
  ref = F_element
FEATURE [App::DocumentObjectGroupPython] G4_F  # scripted group (container) (typed FeaturePython)
  Dunit = g/cm3
  Dvalue = 0.00158029
  Group = -> [F_element019]
  conduct = 2
  density = 1
  expand = 3
  formula = F
  name = G4_F
  specific = 4
FEATURE [App::DocumentObjectGroupPython] Ne_element001  label="Ne_element : 1"  # scripted group (container) (typed FeaturePython)
  n = 1
  ref = Ne_element
FEATURE [App::DocumentObjectGroupPython] G4_Ne  # scripted group (container) (typed FeaturePython)
  Dunit = g/cm3
  Dvalue = 0.000838505
  Group = -> [Ne_element001]
  conduct = 2
  density = 1
  expand = 3
  formula = Ne
  name = G4_Ne
  specific = 4
FEATURE [App::DocumentObjectGroupPython] Na_element020  label="Na_element : 005"  # scripted group (container) (typed FeaturePython)
  n = 1
  ref = Na_element
FEATURE [App::DocumentObjectGroupPython] G4_Na  # scripted group (container) (typed FeaturePython)
  Dunit = g/cm3
  Dvalue = 0.971
  Group = -> [Na_element020]
  conduct = 2
  density = 1
  expand = 3
  formula = Na
  name = G4_Na
  specific = 4
FEATURE [App::DocumentObjectGroupPython] Mg_element011  label="Mg_element : 005"  # scripted group (container) (typed FeaturePython)
  n = 1
  ref = Mg_element
FEATURE [App::DocumentObjectGroupPython] G4_Mg  # scripted group (container) (typed FeaturePython)
  Dunit = g/cm3
  Dvalue = 1.74
  Group = -> [Mg_element011]
  conduct = 2
  density = 1
  expand = 3
  formula = Mg
  name = G4_Mg
  specific = 4
FEATURE [App::DocumentObjectGroupPython] Al_element004  label="Al_element : 1"  # scripted group (container) (typed FeaturePython)
  n = 1
  ref = Al_element
FEATURE [App::DocumentObjectGroupPython] G4_Al  # scripted group (container) (typed FeaturePython)
  Dunit = g/cm3
  Dvalue = 2.699
  Group = -> [Al_element004]
  conduct = 2
  density = 1
  expand = 3
  formula = Al
  name = G4_Al
  specific = 4
FEATURE [App::DocumentObjectGroupPython] Si_element007  label="Si_element : 002"  # scripted group (container) (typed FeaturePython)
  n = 1
  ref = Si_element
FEATURE [App::DocumentObjectGroupPython] G4_Si  # scripted group (container) (typed FeaturePython)
  Dunit = g/cm3
  Dvalue = 2.33
  Group = -> [Si_element007]
  conduct = 2
  density = 1
  expand = 3
  formula = Si
  name = G4_Si
  specific = 4
FEATURE [App::DocumentObjectGroupPython] P_element013  label="P_element : 002"  # scripted group (container) (typed FeaturePython)
  n = 1
  ref = P_element
FEATURE [App::DocumentObjectGroupPython] G4_P  # scripted group (container) (typed FeaturePython)
  Dunit = g/cm3
  Dvalue = 2.2
  Group = -> [P_element013]
  conduct = 2
  density = 1
  expand = 3
  formula = P
  name = G4_P
  specific = 4
FEATURE [App::DocumentObjectGroupPython] S_element023  label="S_element : 007"  # scripted group (container) (typed FeaturePython)
  n = 1
  ref = S_element
FEATURE [App::DocumentObjectGroupPython] G4_S  # scripted group (container) (typed FeaturePython)
  Dunit = g/cm3
  Dvalue = 2
  Group = -> [S_element023]
  conduct = 2
  density = 1
  expand = 3
  formula = S
  name = G4_S
  specific = 4
FEATURE [App::DocumentObjectGroupPython] Cl_element029  label="Cl_element : 015"  # scripted group (container) (typed FeaturePython)
  n = 1
  ref = Cl_element
FEATURE [App::DocumentObjectGroupPython] G4_Cl  # scripted group (container) (typed FeaturePython)
  Dunit = g/cm3
  Dvalue = 0.00299473
  Group = -> [Cl_element029]
  conduct = 2
  density = 1
  expand = 3
  formula = Cl
  name = G4_Cl
  specific = 4
FEATURE [App::DocumentObjectGroupPython] Ar_element002  label="Ar_element : 1"  # scripted group (container) (typed FeaturePython)
  n = 1
  ref = Ar_element
FEATURE [App::DocumentObjectGroupPython] G4_Ar  # scripted group (container) (typed FeaturePython)
  Dunit = g/cm3
  Dvalue = 0.00166201
  Group = -> [Ar_element002]
  conduct = 2
  density = 1
  expand = 3
  formula = Ar
  name = G4_Ar
  specific = 4
FEATURE [App::DocumentObjectGroupPython] K_element013  label="K_element : 003"  # scripted group (container) (typed FeaturePython)
  n = 1
  ref = K_element
FEATURE [App::DocumentObjectGroupPython] G4_K  # scripted group (container) (typed FeaturePython)
  Dunit = g/cm3
  Dvalue = 0.862
  Group = -> [K_element013]
  conduct = 2
  density = 1
  expand = 3
  formula = K
  name = G4_K
  specific = 4
FEATURE [App::DocumentObjectGroupPython] Ca_element014  label="Ca_element : 007"  # scripted group (container) (typed FeaturePython)
  n = 1
  ref = Ca_element
FEATURE [App::DocumentObjectGroupPython] G4_Ca  # scripted group (container) (typed FeaturePython)
  Dunit = g/cm3
  Dvalue = 1.55
  Group = -> [Ca_element014]
  conduct = 2
  density = 1
  expand = 3
  formula = Ca
  name = G4_Ca
  specific = 4
FEATURE [App::DocumentObjectGroupPython] Sc_element001  label="Sc_element : 1"  # scripted group (container) (typed FeaturePython)
  n = 1
  ref = Sc_element
FEATURE [App::DocumentObjectGroupPython] G4_Sc  # scripted group (container) (typed FeaturePython)
  Dunit = g/cm3
  Dvalue = 2.989
  Group = -> [Sc_element001]
  conduct = 2
  density = 1
  expand = 3
  formula = Sc
  name = G4_Sc
  specific = 4
FEATURE [App::DocumentObjectGroupPython] Ti_element004  label="Ti_element : 002"  # scripted group (container) (typed FeaturePython)
  n = 1
  ref = Ti_element
FEATURE [App::DocumentObjectGroupPython] G4_Ti  # scripted group (container) (typed FeaturePython)
  Dunit = g/cm3
  Dvalue = 4.54
  Group = -> [Ti_element004]
  conduct = 2
  density = 1
  expand = 3
  formula = Ti
  name = G4_Ti
  specific = 4
FEATURE [App::DocumentObjectGroupPython] V_element001  label="V_element : 1"  # scripted group (container) (typed FeaturePython)
  n = 1
  ref = V_element
FEATURE [App::DocumentObjectGroupPython] G4_V  # scripted group (container) (typed FeaturePython)
  Dunit = g/cm3
  Dvalue = 6.11
  Group = -> [V_element001]
  conduct = 2
  density = 1
  expand = 3
  formula = V
  name = G4_V
  specific = 4
FEATURE [App::DocumentObjectGroupPython] Cr_element001  label="Cr_element : 1"  # scripted group (container) (typed FeaturePython)
  n = 1
  ref = Cr_element
FEATURE [App::DocumentObjectGroupPython] G4_Cr  # scripted group (container) (typed FeaturePython)
  Dunit = g/cm3
  Dvalue = 7.18
  Group = -> [Cr_element001]
  conduct = 2
  density = 1
  expand = 3
  formula = Cr
  name = G4_Cr
  specific = 4
FEATURE [App::DocumentObjectGroupPython] Mn_element001  label="Mn_element : 1"  # scripted group (container) (typed FeaturePython)
  n = 1
  ref = Mn_element
FEATURE [App::DocumentObjectGroupPython] G4_Mn  # scripted group (container) (typed FeaturePython)
  Dunit = g/cm3
  Dvalue = 7.44
  Group = -> [Mn_element001]
  conduct = 2
  density = 1
  expand = 3
  formula = Mn
  name = G4_Mn
  specific = 4
FEATURE [App::DocumentObjectGroupPython] Fe_element007  label="Fe_element : 004"  # scripted group (container) (typed FeaturePython)
  n = 1
  ref = Fe_element
FEATURE [App::DocumentObjectGroupPython] G4_Fe  # scripted group (container) (typed FeaturePython)
  Dunit = g/cm3
  Dvalue = 7.874
  Group = -> [Fe_element007]
  conduct = 2
  density = 1
  expand = 3
  formula = Fe
  name = G4_Fe
  specific = 4
FEATURE [App::DocumentObjectGroupPython] Co_element001  label="Co_element : 1"  # scripted group (container) (typed FeaturePython)
  n = 1
  ref = Co_element
FEATURE [App::DocumentObjectGroupPython] G4_Co  # scripted group (container) (typed FeaturePython)
  Dunit = g/cm3
  Dvalue = 8.9
  Group = -> [Co_element001]
  conduct = 2
  density = 1
  expand = 3
  formula = Co
  name = G4_Co
  specific = 4
FEATURE [App::DocumentObjectGroupPython] Ni_element001  label="Ni_element : 1"  # scripted group (container) (typed FeaturePython)
  n = 1
  ref = Ni_element
FEATURE [App::DocumentObjectGroupPython] G4_Ni  # scripted group (container) (typed FeaturePython)
  Dunit = g/cm3
  Dvalue = 8.902
  Group = -> [Ni_element001]
  conduct = 2
  density = 1
  expand = 3
  formula = Ni
  name = G4_Ni
  specific = 4
FEATURE [App::DocumentObjectGroupPython] Cu_element001  label="Cu_element : 1"  # scripted group (container) (typed FeaturePython)
  n = 1
  ref = Cu_element
FEATURE [App::DocumentObjectGroupPython] G4_Cu  # scripted group (container) (typed FeaturePython)
  Dunit = g/cm3
  Dvalue = 8.96
  Group = -> [Cu_element001]
  conduct = 2
  density = 1
  expand = 3
  formula = Cu
  name = G4_Cu
  specific = 4
FEATURE [App::DocumentObjectGroupPython] Zn_element001  label="Zn_element : 1"  # scripted group (container) (typed FeaturePython)
  n = 1
  ref = Zn_element
FEATURE [App::DocumentObjectGroupPython] G4_Zn  # scripted group (container) (typed FeaturePython)
  Dunit = g/cm3
  Dvalue = 7.133
  Group = -> [Zn_element001]
  conduct = 2
  density = 1
  expand = 3
  formula = Zn
  name = G4_Zn
  specific = 4
FEATURE [App::DocumentObjectGroupPython] Ga_element002  label="Ga_element : 002"  # scripted group (container) (typed FeaturePython)
  n = 1
  ref = Ga_element
FEATURE [App::DocumentObjectGroupPython] G4_Ga  # scripted group (container) (typed FeaturePython)
  Dunit = g/cm3
  Dvalue = 5.904
  Group = -> [Ga_element002]
  conduct = 2
  density = 1
  expand = 3
  formula = Ga
  name = G4_Ga
  specific = 4
FEATURE [App::DocumentObjectGroupPython] Ge_element002  label="Ge_element : 1"  # scripted group (container) (typed FeaturePython)
  n = 1
  ref = Ge_element
FEATURE [App::DocumentObjectGroupPython] G4_Ge  # scripted group (container) (typed FeaturePython)
  Dunit = g/cm3
  Dvalue = 5.323
  Group = -> [Ge_element002]
  conduct = 2
  density = 1
  expand = 3
  formula = Ge
  name = G4_Ge
  specific = 4
FEATURE [App::DocumentObjectGroupPython] As_element003  label="As_element : 002"  # scripted group (container) (typed FeaturePython)
  n = 1
  ref = As_element
FEATURE [App::DocumentObjectGroupPython] G4_As  # scripted group (container) (typed FeaturePython)
  Dunit = g/cm3
  Dvalue = 5.73
  Group = -> [As_element003]
  conduct = 2
  density = 1
  expand = 3
  formula = As
  name = G4_As
  specific = 4
FEATURE [App::DocumentObjectGroupPython] Se_element001  label="Se_element : 1"  # scripted group (container) (typed FeaturePython)
  n = 1
  ref = Se_element
FEATURE [App::DocumentObjectGroupPython] G4_Se  # scripted group (container) (typed FeaturePython)
  Dunit = g/cm3
  Dvalue = 4.5
  Group = -> [Se_element001]
  conduct = 2
  density = 1
  expand = 3
  formula = Se
  name = G4_Se
  specific = 4
FEATURE [App::DocumentObjectGroupPython] Br_element007  label="Br_element : 004"  # scripted group (container) (typed FeaturePython)
  n = 1
  ref = Br_element
FEATURE [App::DocumentObjectGroupPython] G4_Br  # scripted group (container) (typed FeaturePython)
  Dunit = g/cm3
  Dvalue = 0.0070721
  Group = -> [Br_element007]
  conduct = 2
  density = 1
  expand = 3
  formula = Br
  name = G4_Br
  specific = 4
FEATURE [App::DocumentObjectGroupPython] Kr_element001  label="Kr_element : 1"  # scripted group (container) (typed FeaturePython)
  n = 1
  ref = Kr_element
FEATURE [App::DocumentObjectGroupPython] G4_Kr  # scripted group (container) (typed FeaturePython)
  Dunit = g/cm3
  Dvalue = 0.00347832
  Group = -> [Kr_element001]
  conduct = 2
  density = 1
  expand = 3
  formula = Kr
  name = G4_Kr
  specific = 4
FEATURE [App::DocumentObjectGroupPython] Rb_element001  label="Rb_element : 1"  # scripted group (container) (typed FeaturePython)
  n = 1
  ref = Rb_element
FEATURE [App::DocumentObjectGroupPython] G4_Rb  # scripted group (container) (typed FeaturePython)
  Dunit = g/cm3
  Dvalue = 1.532
  Group = -> [Rb_element001]
  conduct = 2
  density = 1
  expand = 3
  formula = Rb
  name = G4_Rb
  specific = 4
FEATURE [App::DocumentObjectGroupPython] Sr_element001  label="Sr_element : 1"  # scripted group (container) (typed FeaturePython)
  n = 1
  ref = Sr_element
FEATURE [App::DocumentObjectGroupPython] G4_Sr  # scripted group (container) (typed FeaturePython)
  Dunit = g/cm3
  Dvalue = 2.54
  Group = -> [Sr_element001]
  conduct = 2
  density = 1
  expand = 3
  formula = Sr
  name = G4_Sr
  specific = 4
FEATURE [App::DocumentObjectGroupPython] Y_element001  label="Y_element : 1"  # scripted group (container) (typed FeaturePython)
  n = 1
  ref = Y_element
FEATURE [App::DocumentObjectGroupPython] G4_Y  # scripted group (container) (typed FeaturePython)
  Dunit = g/cm3
  Dvalue = 4.469
  Group = -> [Y_element001]
  conduct = 2
  density = 1
  expand = 3
  formula = Y
  name = G4_Y
  specific = 4
FEATURE [App::DocumentObjectGroupPython] Zr_element001  label="Zr_element : 1"  # scripted group (container) (typed FeaturePython)
  n = 1
  ref = Zr_element
FEATURE [App::DocumentObjectGroupPython] G4_Zr  # scripted group (container) (typed FeaturePython)
  Dunit = g/cm3
  Dvalue = 6.506
  Group = -> [Zr_element001]
  conduct = 2
  density = 1
  expand = 3
  formula = Zr
  name = G4_Zr
  specific = 4
FEATURE [App::DocumentObjectGroupPython] Nb_element001  label="Nb_element : 1"  # scripted group (container) (typed FeaturePython)
  n = 1
  ref = Nb_element
FEATURE [App::DocumentObjectGroupPython] G4_Nb  # scripted group (container) (typed FeaturePython)
  Dunit = g/cm3
  Dvalue = 8.57
  Group = -> [Nb_element001]
  conduct = 2
  density = 1
  expand = 3
  formula = Nb
  name = G4_Nb
  specific = 4
FEATURE [App::DocumentObjectGroupPython] Mo_element001  label="Mo_element : 1"  # scripted group (container) (typed FeaturePython)
  n = 1
  ref = Mo_element
FEATURE [App::DocumentObjectGroupPython] G4_Mo  # scripted group (container) (typed FeaturePython)
  Dunit = g/cm3
  Dvalue = 10.22
  Group = -> [Mo_element001]
  conduct = 2
  density = 1
  expand = 3
  formula = Mo
  name = G4_Mo
  specific = 4
FEATURE [App::DocumentObjectGroupPython] Tc_element001  label="Tc_element : 1"  # scripted group (container) (typed FeaturePython)
  n = 1
  ref = Tc_element
FEATURE [App::DocumentObjectGroupPython] G4_Tc  # scripted group (container) (typed FeaturePython)
  Dunit = g/cm3
  Dvalue = 11.5
  Group = -> [Tc_element001]
  conduct = 2
  density = 1
  expand = 3
  formula = Tc
  name = G4_Tc
  specific = 4
FEATURE [App::DocumentObjectGroupPython] Ru_element001  label="Ru_element : 1"  # scripted group (container) (typed FeaturePython)
  n = 1
  ref = Ru_element
FEATURE [App::DocumentObjectGroupPython] G4_Ru  # scripted group (container) (typed FeaturePython)
  Dunit = g/cm3
  Dvalue = 12.41
  Group = -> [Ru_element001]
  conduct = 2
  density = 1
  expand = 3
  formula = Ru
  name = G4_Ru
  specific = 4
FEATURE [App::DocumentObjectGroupPython] Rh_element001  label="Rh_element : 1"  # scripted group (container) (typed FeaturePython)
  n = 1
  ref = Rh_element
FEATURE [App::DocumentObjectGroupPython] G4_Rh  # scripted group (container) (typed FeaturePython)
  Dunit = g/cm3
  Dvalue = 12.41
  Group = -> [Rh_element001]
  conduct = 2
  density = 1
  expand = 3
  formula = Rh
  name = G4_Rh
  specific = 4
FEATURE [App::DocumentObjectGroupPython] Pd_element001  label="Pd_element : 1"  # scripted group (container) (typed FeaturePython)
  n = 1
  ref = Pd_element
FEATURE [App::DocumentObjectGroupPython] G4_Pd  # scripted group (container) (typed FeaturePython)
  Dunit = g/cm3
  Dvalue = 12.02
  Group = -> [Pd_element001]
  conduct = 2
  density = 1
  expand = 3
  formula = Pd
  name = G4_Pd
  specific = 4
FEATURE [App::DocumentObjectGroupPython] Ag_element006  label="Ag_element : 004"  # scripted group (container) (typed FeaturePython)
  n = 1
  ref = Ag_element
FEATURE [App::DocumentObjectGroupPython] G4_Ag  # scripted group (container) (typed FeaturePython)
  Dunit = g/cm3
  Dvalue = 10.5
  Group = -> [Ag_element006]
  conduct = 2
  density = 1
  expand = 3
  formula = Ag
  name = G4_Ag
  specific = 4
FEATURE [App::DocumentObjectGroupPython] Cd_element003  label="Cd_element : 003"  # scripted group (container) (typed FeaturePython)
  n = 1
  ref = Cd_element
FEATURE [App::DocumentObjectGroupPython] G4_Cd  # scripted group (container) (typed FeaturePython)
  Dunit = g/cm3
  Dvalue = 8.65
  Group = -> [Cd_element003]
  conduct = 2
  density = 1
  expand = 3
  formula = Cd
  name = G4_Cd
  specific = 4
FEATURE [App::DocumentObjectGroupPython] In_element001  label="In_element : 1"  # scripted group (container) (typed FeaturePython)
  n = 1
  ref = In_element
FEATURE [App::DocumentObjectGroupPython] G4_In  # scripted group (container) (typed FeaturePython)
  Dunit = g/cm3
  Dvalue = 7.31
  Group = -> [In_element001]
  conduct = 2
  density = 1
  expand = 3
  formula = In
  name = G4_In
  specific = 4
FEATURE [App::DocumentObjectGroupPython] Sn_element001  label="Sn_element : 1"  # scripted group (container) (typed FeaturePython)
  n = 1
  ref = Sn_element
FEATURE [App::DocumentObjectGroupPython] G4_Sn  # scripted group (container) (typed FeaturePython)
  Dunit = g/cm3
  Dvalue = 7.31
  Group = -> [Sn_element001]
  conduct = 2
  density = 1
  expand = 3
  formula = Sn
  name = G4_Sn
  specific = 4
FEATURE [App::DocumentObjectGroupPython] Sb_element001  label="Sb_element : 1"  # scripted group (container) (typed FeaturePython)
  n = 1
  ref = Sb_element
FEATURE [App::DocumentObjectGroupPython] G4_Sb  # scripted group (container) (typed FeaturePython)
  Dunit = g/cm3
  Dvalue = 6.691
  Group = -> [Sb_element001]
  conduct = 2
  density = 1
  expand = 3
  formula = Sb
  name = G4_Sb
  specific = 4
FEATURE [App::DocumentObjectGroupPython] Te_element002  label="Te_element : 002"  # scripted group (container) (typed FeaturePython)
  n = 1
  ref = Te_element
FEATURE [App::DocumentObjectGroupPython] G4_Te  # scripted group (container) (typed FeaturePython)
  Dunit = g/cm3
  Dvalue = 6.24
  Group = -> [Te_element002]
  conduct = 2
  density = 1
  expand = 3
  formula = Te
  name = G4_Te
  specific = 4
FEATURE [App::DocumentObjectGroupPython] I_element010  label="I_element : 006"  # scripted group (container) (typed FeaturePython)
  n = 1
  ref = I_element
FEATURE [App::DocumentObjectGroupPython] G4_I  # scripted group (container) (typed FeaturePython)
  Dunit = g/cm3
  Dvalue = 4.93
  Group = -> [I_element010]
  conduct = 2
  density = 1
  expand = 3
  formula = I
  name = G4_I
  specific = 4
FEATURE [App::DocumentObjectGroupPython] Xe_element001  label="Xe_element : 1"  # scripted group (container) (typed FeaturePython)
  n = 1
  ref = Xe_element
FEATURE [App::DocumentObjectGroupPython] G4_Xe  # scripted group (container) (typed FeaturePython)
  Dunit = g/cm3
  Dvalue = 0.00548536
  Group = -> [Xe_element001]
  conduct = 2
  density = 1
  expand = 3
  formula = Xe
  name = G4_Xe
  specific = 4
FEATURE [App::DocumentObjectGroupPython] Cs_element003  label="Cs_element : 003"  # scripted group (container) (typed FeaturePython)
  n = 1
  ref = Cs_element
FEATURE [App::DocumentObjectGroupPython] G4_Cs  # scripted group (container) (typed FeaturePython)
  Dunit = g/cm3
  Dvalue = 1.873
  Group = -> [Cs_element003]
  conduct = 2
  density = 1
  expand = 3
  formula = Cs
  name = G4_Cs
  specific = 4
FEATURE [App::DocumentObjectGroupPython] Ba_element003  label="Ba_element : 003"  # scripted group (container) (typed FeaturePython)
  n = 1
  ref = Ba_element
FEATURE [App::DocumentObjectGroupPython] G4_Ba  # scripted group (container) (typed FeaturePython)
  Dunit = g/cm3
  Dvalue = 3.5
  Group = -> [Ba_element003]
  conduct = 2
  density = 1
  expand = 3
  formula = Ba
  name = G4_Ba
  specific = 4
FEATURE [App::DocumentObjectGroupPython] La_element003  label="La_element : 003"  # scripted group (container) (typed FeaturePython)
  n = 1
  ref = La_element
FEATURE [App::DocumentObjectGroupPython] G4_La  # scripted group (container) (typed FeaturePython)
  Dunit = g/cm3
  Dvalue = 6.154
  Group = -> [La_element003]
  conduct = 2
  density = 1
  expand = 3
  formula = La
  name = G4_La
  specific = 4
FEATURE [App::DocumentObjectGroupPython] Ce_element002  label="Ce_element : 1"  # scripted group (container) (typed FeaturePython)
  n = 1
  ref = Ce_element
FEATURE [App::DocumentObjectGroupPython] G4_Ce  # scripted group (container) (typed FeaturePython)
  Dunit = g/cm3
  Dvalue = 6.657
  Group = -> [Ce_element002]
  conduct = 2
  density = 1
  expand = 3
  formula = Ce
  name = G4_Ce
  specific = 4
FEATURE [App::DocumentObjectGroupPython] Pr_element001  label="Pr_element : 1"  # scripted group (container) (typed FeaturePython)
  n = 1
  ref = Pr_element
FEATURE [App::DocumentObjectGroupPython] G4_Pr  # scripted group (container) (typed FeaturePython)
  Dunit = g/cm3
  Dvalue = 6.71
  Group = -> [Pr_element001]
  conduct = 2
  density = 1
  expand = 3
  formula = Pr
  name = G4_Pr
  specific = 4
FEATURE [App::DocumentObjectGroupPython] Nd_element001  label="Nd_element : 1"  # scripted group (container) (typed FeaturePython)
  n = 1
  ref = Nd_element
FEATURE [App::DocumentObjectGroupPython] G4_Nd  # scripted group (container) (typed FeaturePython)
  Dunit = g/cm3
  Dvalue = 6.9
  Group = -> [Nd_element001]
  conduct = 2
  density = 1
  expand = 3
  formula = Nd
  name = G4_Nd
  specific = 4
FEATURE [App::DocumentObjectGroupPython] Pm_element001  label="Pm_element : 1"  # scripted group (container) (typed FeaturePython)
  n = 1
  ref = Pm_element
FEATURE [App::DocumentObjectGroupPython] G4_Pm  # scripted group (container) (typed FeaturePython)
  Dunit = g/cm3
  Dvalue = 7.22
  Group = -> [Pm_element001]
  conduct = 2
  density = 1
  expand = 3
  formula = Pm
  name = G4_Pm
  specific = 4
FEATURE [App::DocumentObjectGroupPython] Sm_element001  label="Sm_element : 1"  # scripted group (container) (typed FeaturePython)
  n = 1
  ref = Sm_element
FEATURE [App::DocumentObjectGroupPython] G4_Sm  # scripted group (container) (typed FeaturePython)
  Dunit = g/cm3
  Dvalue = 7.46
  Group = -> [Sm_element001]
  conduct = 2
  density = 1
  expand = 3
  formula = Sm
  name = G4_Sm
  specific = 4
FEATURE [App::DocumentObjectGroupPython] Eu_element001  label="Eu_element : 1"  # scripted group (container) (typed FeaturePython)
  n = 1
  ref = Eu_element
FEATURE [App::DocumentObjectGroupPython] G4_Eu  # scripted group (container) (typed FeaturePython)
  Dunit = g/cm3
  Dvalue = 5.243
  Group = -> [Eu_element001]
  conduct = 2
  density = 1
  expand = 3
  formula = Eu
  name = G4_Eu
  specific = 4
FEATURE [App::DocumentObjectGroupPython] Gd_element002  label="Gd_element : 1"  # scripted group (container) (typed FeaturePython)
  n = 1
  ref = Gd_element
FEATURE [App::DocumentObjectGroupPython] G4_Gd  # scripted group (container) (typed FeaturePython)
  Dunit = g/cm3
  Dvalue = 7.9004
  Group = -> [Gd_element002]
  conduct = 2
  density = 1
  expand = 3
  formula = Gd
  name = G4_Gd
  specific = 4
FEATURE [App::DocumentObjectGroupPython] Tb_element001  label="Tb_element : 1"  # scripted group (container) (typed FeaturePython)
  n = 1
  ref = Tb_element
FEATURE [App::DocumentObjectGroupPython] G4_Tb  # scripted group (container) (typed FeaturePython)
  Dunit = g/cm3
  Dvalue = 8.229
  Group = -> [Tb_element001]
  conduct = 2
  density = 1
  expand = 3
  formula = Tb
  name = G4_Tb
  specific = 4
FEATURE [App::DocumentObjectGroupPython] Dy_element001  label="Dy_element : 1"  # scripted group (container) (typed FeaturePython)
  n = 1
  ref = Dy_element
FEATURE [App::DocumentObjectGroupPython] G4_Dy  # scripted group (container) (typed FeaturePython)
  Dunit = g/cm3
  Dvalue = 8.55
  Group = -> [Dy_element001]
  conduct = 2
  density = 1
  expand = 3
  formula = Dy
  name = G4_Dy
  specific = 4
FEATURE [App::DocumentObjectGroupPython] Ho_element001  label="Ho_element : 1"  # scripted group (container) (typed FeaturePython)
  n = 1
  ref = Ho_element
FEATURE [App::DocumentObjectGroupPython] G4_Ho  # scripted group (container) (typed FeaturePython)
  Dunit = g/cm3
  Dvalue = 8.795
  Group = -> [Ho_element001]
  conduct = 2
  density = 1
  expand = 3
  formula = Ho
  name = G4_Ho
  specific = 4
FEATURE [App::DocumentObjectGroupPython] Er_element001  label="Er_element : 1"  # scripted group (container) (typed FeaturePython)
  n = 1
  ref = Er_element
FEATURE [App::DocumentObjectGroupPython] G4_Er  # scripted group (container) (typed FeaturePython)
  Dunit = g/cm3
  Dvalue = 9.066
  Group = -> [Er_element001]
  conduct = 2
  density = 1
  expand = 3
  formula = Er
  name = G4_Er
  specific = 4
FEATURE [App::DocumentObjectGroupPython] Tm_element001  label="Tm_element : 1"  # scripted group (container) (typed FeaturePython)
  n = 1
  ref = Tm_element
FEATURE [App::DocumentObjectGroupPython] G4_Tm  # scripted group (container) (typed FeaturePython)
  Dunit = g/cm3
  Dvalue = 9.321
  Group = -> [Tm_element001]
  conduct = 2
  density = 1
  expand = 3
  formula = Tm
  name = G4_Tm
  specific = 4
FEATURE [App::DocumentObjectGroupPython] Yb_element001  label="Yb_element : 1"  # scripted group (container) (typed FeaturePython)
  n = 1
  ref = Yb_element
FEATURE [App::DocumentObjectGroupPython] G4_Yb  # scripted group (container) (typed FeaturePython)
  Dunit = g/cm3
  Dvalue = 6.73
  Group = -> [Yb_element001]
  conduct = 2
  density = 1
  expand = 3
  formula = Yb
  name = G4_Yb
  specific = 4
FEATURE [App::DocumentObjectGroupPython] Lu_element001  label="Lu_element : 1"  # scripted group (container) (typed FeaturePython)
  n = 1
  ref = Lu_element
FEATURE [App::DocumentObjectGroupPython] G4_Lu  # scripted group (container) (typed FeaturePython)
  Dunit = g/cm3
  Dvalue = 9.84
  Group = -> [Lu_element001]
  conduct = 2
  density = 1
  expand = 3
  formula = Lu
  name = G4_Lu
  specific = 4
FEATURE [App::DocumentObjectGroupPython] Hf_element001  label="Hf_element : 1"  # scripted group (container) (typed FeaturePython)
  n = 1
  ref = Hf_element
FEATURE [App::DocumentObjectGroupPython] G4_Hf  # scripted group (container) (typed FeaturePython)
  Dunit = g/cm3
  Dvalue = 13.31
  Group = -> [Hf_element001]
  conduct = 2
  density = 1
  expand = 3
  formula = Hf
  name = G4_Hf
  specific = 4
FEATURE [App::DocumentObjectGroupPython] Ta_element001  label="Ta_element : 1"  # scripted group (container) (typed FeaturePython)
  n = 1
  ref = Ta_element
FEATURE [App::DocumentObjectGroupPython] G4_Ta  # scripted group (container) (typed FeaturePython)
  Dunit = g/cm3
  Dvalue = 16.654
  Group = -> [Ta_element001]
  conduct = 2
  density = 1
  expand = 3
  formula = Ta
  name = G4_Ta
  specific = 4
FEATURE [App::DocumentObjectGroupPython] W_element004  label="W_element : 004"  # scripted group (container) (typed FeaturePython)
  n = 1
  ref = W_element
FEATURE [App::DocumentObjectGroupPython] G4_W  # scripted group (container) (typed FeaturePython)
  Dunit = g/cm3
  Dvalue = 19.3
  Group = -> [W_element004]
  conduct = 2
  density = 1
  expand = 3
  formula = W
  name = G4_W
  specific = 4
FEATURE [App::DocumentObjectGroupPython] Re_element001  label="Re_element : 1"  # scripted group (container) (typed FeaturePython)
  n = 1
  ref = Re_element
FEATURE [App::DocumentObjectGroupPython] G4_Re  # scripted group (container) (typed FeaturePython)
  Dunit = g/cm3
  Dvalue = 21.02
  Group = -> [Re_element001]
  conduct = 2
  density = 1
  expand = 3
  formula = Re
  name = G4_Re
  specific = 4
FEATURE [App::DocumentObjectGroupPython] Os_element001  label="Os_element : 1"  # scripted group (container) (typed FeaturePython)
  n = 1
  ref = Os_element
FEATURE [App::DocumentObjectGroupPython] G4_Os  # scripted group (container) (typed FeaturePython)
  Dunit = g/cm3
  Dvalue = 22.57
  Group = -> [Os_element001]
  conduct = 2
  density = 1
  expand = 3
  formula = Os
  name = G4_Os
  specific = 4
FEATURE [App::DocumentObjectGroupPython] Ir_element001  label="Ir_element : 1"  # scripted group (container) (typed FeaturePython)
  n = 1
  ref = Ir_element
FEATURE [App::DocumentObjectGroupPython] G4_Ir  # scripted group (container) (typed FeaturePython)
  Dunit = g/cm3
  Dvalue = 22.42
  Group = -> [Ir_element001]
  conduct = 2
  density = 1
  expand = 3
  formula = Ir
  name = G4_Ir
  specific = 4
FEATURE [App::DocumentObjectGroupPython] Pt_element001  label="Pt_element : 1"  # scripted group (container) (typed FeaturePython)
  n = 1
  ref = Pt_element
FEATURE [App::DocumentObjectGroupPython] G4_Pt  # scripted group (container) (typed FeaturePython)
  Dunit = g/cm3
  Dvalue = 21.45
  Group = -> [Pt_element001]
  conduct = 2
  density = 1
  expand = 3
  formula = Pt
  name = G4_Pt
  specific = 4
FEATURE [App::DocumentObjectGroupPython] Au_element001  label="Au_element : 1"  # scripted group (container) (typed FeaturePython)
  n = 1
  ref = Au_element
FEATURE [App::DocumentObjectGroupPython] G4_Au  # scripted group (container) (typed FeaturePython)
  Dunit = g/cm3
  Dvalue = 19.32
  Group = -> [Au_element001]
  conduct = 2
  density = 1
  expand = 3
  formula = Au
  name = G4_Au
  specific = 4
FEATURE [App::DocumentObjectGroupPython] Hg_element002  label="Hg_element : 002"  # scripted group (container) (typed FeaturePython)
  n = 1
  ref = Hg_element
FEATURE [App::DocumentObjectGroupPython] G4_Hg  # scripted group (container) (typed FeaturePython)
  Dunit = g/cm3
  Dvalue = 13.546
  Group = -> [Hg_element002]
  conduct = 2
  density = 1
  expand = 3
  formula = Hg
  name = G4_Hg
  specific = 4
FEATURE [App::DocumentObjectGroupPython] Tl_element002  label="Tl_element : 002"  # scripted group (container) (typed FeaturePython)
  n = 1
  ref = Tl_element
FEATURE [App::DocumentObjectGroupPython] G4_Tl  # scripted group (container) (typed FeaturePython)
  Dunit = g/cm3
  Dvalue = 11.72
  Group = -> [Tl_element002]
  conduct = 2
  density = 1
  expand = 3
  formula = Tl
  name = G4_Tl
  specific = 4
FEATURE [App::DocumentObjectGroupPython] Pb_element003  label="Pb_element : 1"  # scripted group (container) (typed FeaturePython)
  n = 1
  ref = Pb_element
FEATURE [App::DocumentObjectGroupPython] G4_Pb  # scripted group (container) (typed FeaturePython)
  Dunit = g/cm3
  Dvalue = 11.35
  Group = -> [Pb_element003]
  conduct = 2
  density = 1
  expand = 3
  formula = Pb
  name = G4_Pb
  specific = 4
FEATURE [App::DocumentObjectGroupPython] Bi_element002  label="Bi_element : 1"  # scripted group (container) (typed FeaturePython)
  n = 1
  ref = Bi_element
FEATURE [App::DocumentObjectGroupPython] G4_Bi  # scripted group (container) (typed FeaturePython)
  Dunit = g/cm3
  Dvalue = 9.747
  Group = -> [Bi_element002]
  conduct = 2
  density = 1
  expand = 3
  formula = Bi
  name = G4_Bi
  specific = 4
FEATURE [App::DocumentObjectGroupPython] Po_element001  label="Po_element : 1"  # scripted group (container) (typed FeaturePython)
  n = 1
  ref = Po_element
FEATURE [App::DocumentObjectGroupPython] G4_Po  # scripted group (container) (typed FeaturePython)
  Dunit = g/cm3
  Dvalue = 9.32
  Group = -> [Po_element001]
  conduct = 2
  density = 1
  expand = 3
  formula = Po
  name = G4_Po
  specific = 4
FEATURE [App::DocumentObjectGroupPython] At_element001  label="At_element : 1"  # scripted group (container) (typed FeaturePython)
  n = 1
  ref = At_element
FEATURE [App::DocumentObjectGroupPython] G4_At  # scripted group (container) (typed FeaturePython)
  Dunit = g/cm3
  Dvalue = 9.32
  Group = -> [At_element001]
  conduct = 2
  density = 1
  expand = 3
  formula = At
  name = G4_At
  specific = 4
FEATURE [App::DocumentObjectGroupPython] Rn_element001  label="Rn_element : 1"  # scripted group (container) (typed FeaturePython)
  n = 1
  ref = Rn_element
FEATURE [App::DocumentObjectGroupPython] G4_Rn  # scripted group (container) (typed FeaturePython)
  Dunit = g/cm3
  Dvalue = 0.00900662
  Group = -> [Rn_element001]
  conduct = 2
  density = 1
  expand = 3
  formula = Rn
  name = G4_Rn
  specific = 4
FEATURE [App::DocumentObjectGroupPython] Fr_element001  label="Fr_element : 1"  # scripted group (container) (typed FeaturePython)
  n = 1
  ref = Fr_element
FEATURE [App::DocumentObjectGroupPython] G4_Fr  # scripted group (container) (typed FeaturePython)
  Dunit = g/cm3
  Dvalue = 1
  Group = -> [Fr_element001]
  conduct = 2
  density = 1
  expand = 3
  formula = Fr
  name = G4_Fr
  specific = 4
FEATURE [App::DocumentObjectGroupPython] Ra_element001  label="Ra_element : 1"  # scripted group (container) (typed FeaturePython)
  n = 1
  ref = Ra_element
FEATURE [App::DocumentObjectGroupPython] G4_Ra  # scripted group (container) (typed FeaturePython)
  Dunit = g/cm3
  Dvalue = 5
  Group = -> [Ra_element001]
  conduct = 2
  density = 1
  expand = 3
  formula = Ra
  name = G4_Ra
  specific = 4
FEATURE [App::DocumentObjectGroupPython] Ac_element001  label="Ac_element : 1"  # scripted group (container) (typed FeaturePython)
  n = 1
  ref = Ac_element
FEATURE [App::DocumentObjectGroupPython] G4_Ac  # scripted group (container) (typed FeaturePython)
  Dunit = g/cm3
  Dvalue = 10.07
  Group = -> [Ac_element001]
  conduct = 2
  density = 1
  expand = 3
  formula = Ac
  name = G4_Ac
  specific = 4
FEATURE [App::DocumentObjectGroupPython] Th_element001  label="Th_element : 1"  # scripted group (container) (typed FeaturePython)
  n = 1
  ref = Th_element
FEATURE [App::DocumentObjectGroupPython] G4_Th  # scripted group (container) (typed FeaturePython)
  Dunit = g/cm3
  Dvalue = 11.72
  Group = -> [Th_element001]
  conduct = 2
  density = 1
  expand = 3
  formula = Th
  name = G4_Th
  specific = 4
FEATURE [App::DocumentObjectGroupPython] Pa_element001  label="Pa_element : 1"  # scripted group (container) (typed FeaturePython)
  n = 1
  ref = Pa_element
FEATURE [App::DocumentObjectGroupPython] G4_Pa  # scripted group (container) (typed FeaturePython)
  Dunit = g/cm3
  Dvalue = 15.37
  Group = -> [Pa_element001]
  conduct = 2
  density = 1
  expand = 3
  formula = Pa
  name = G4_Pa
  specific = 4
FEATURE [App::DocumentObjectGroupPython] U_element004  label="U_element : 004"  # scripted group (container) (typed FeaturePython)
  n = 1
  ref = U_element
FEATURE [App::DocumentObjectGroupPython] G4_U  # scripted group (container) (typed FeaturePython)
  Dunit = g/cm3
  Dvalue = 18.95
  Group = -> [U_element004]
  conduct = 2
  density = 1
  expand = 3
  formula = U
  name = G4_U
  specific = 4
FEATURE [App::DocumentObjectGroupPython] Np_element001  label="Np_element : 1"  # scripted group (container) (typed FeaturePython)
  n = 1
  ref = Np_element
FEATURE [App::DocumentObjectGroupPython] G4_Np  # scripted group (container) (typed FeaturePython)
  Dunit = g/cm3
  Dvalue = 20.25
  Group = -> [Np_element001]
  conduct = 2
  density = 1
  expand = 3
  formula = Np
  name = G4_Np
  specific = 4
FEATURE [App::DocumentObjectGroupPython] Pu_element002  label="Pu_element : 002"  # scripted group (container) (typed FeaturePython)
  n = 1
  ref = Pu_element
FEATURE [App::DocumentObjectGroupPython] G4_Pu  # scripted group (container) (typed FeaturePython)
  Dunit = g/cm3
  Dvalue = 19.84
  Group = -> [Pu_element002]
  conduct = 2
  density = 1
  expand = 3
  formula = Pu
  name = G4_Pu
  specific = 4
FEATURE [App::DocumentObjectGroupPython] Am_element001  label="Am_element : 1"  # scripted group (container) (typed FeaturePython)
  n = 1
  ref = Am_element
FEATURE [App::DocumentObjectGroupPython] G4_Am  # scripted group (container) (typed FeaturePython)
  Dunit = g/cm3
  Dvalue = 13.67
  Group = -> [Am_element001]
  conduct = 2
  density = 1
  expand = 3
  formula = Am
  name = G4_Am
  specific = 4
FEATURE [App::DocumentObjectGroupPython] Cm_element001  label="Cm_element : 1"  # scripted group (container) (typed FeaturePython)
  n = 1
  ref = Cm_element
FEATURE [App::DocumentObjectGroupPython] G4_Cm  # scripted group (container) (typed FeaturePython)
  Dunit = g/cm3
  Dvalue = 13.51
  Group = -> [Cm_element001]
  conduct = 2
  density = 1
  expand = 3
  formula = Cm
  name = G4_Cm
  specific = 4
FEATURE [App::DocumentObjectGroupPython] Bk_element001  label="Bk_element : 1"  # scripted group (container) (typed FeaturePython)
  n = 1
  ref = Bk_element
FEATURE [App::DocumentObjectGroupPython] G4_Bk  # scripted group (container) (typed FeaturePython)
  Dunit = g/cm3
  Dvalue = 14
  Group = -> [Bk_element001]
  conduct = 2
  density = 1
  expand = 3
  formula = Bk
  name = G4_Bk
  specific = 4
FEATURE [App::DocumentObjectGroupPython] Cf_element001  label="Cf_element : 1"  # scripted group (container) (typed FeaturePython)
  n = 1
  ref = Cf_element
FEATURE [App::DocumentObjectGroupPython] G4_Cf  # scripted group (container) (typed FeaturePython)
  Dunit = g/cm3
  Dvalue = 10
  Group = -> [Cf_element001]
  conduct = 2
  density = 1
  expand = 3
  formula = Cf
  name = G4_Cf
  specific = 4
FEATURE [App::DocumentObjectGroupPython] Element  # scripted group (container) (typed FeaturePython)
  Group = -> [G4_H,G4_He,G4_Li,G4_Be,G4_B,G4_C,G4_N,G4_O,G4_F,G4_Ne,G4_Na,G4_Mg,G4_Al,G4_Si,G4_P,G4_S,G4_Cl,G4_Ar,G4_K,G4_Ca,G4_Sc,G4_Ti,G4_V,G4_Cr,G4_Mn,G4_Fe,G4_Co,G4_Ni,G4_Cu,G4_Zn,G4_Ga,G4_Ge,G4_As,G4_Se,G4_Br,G4_Kr,G4_Rb,G4_Sr,G4_Y,G4_Zr,G4_Nb,G4_Mo,G4_Tc,G4_Ru,G4_Rh,G4_Pd,G4_Ag,G4_Cd,G4_In,G4_Sn,G4_Sb,G4_Te,G4_I,G4_Xe,G4_Cs,G4_Ba,G4_La,G4_Ce,G4_Pr,G4_Nd,G4_Pm,G4_Sm,G4_Eu,G4_Gd,G4_Tb,G4_Dy,G4_Ho,G4_Er,+30 more]
FEATURE [App::DocumentObjectGroupPython] H_element114  label="H_element : 063"  # scripted group (container) (typed FeaturePython)
  n = 2
  ref = H_element
FEATURE [App::DocumentObjectGroupPython] G4_lH2  # scripted group (container) (typed FeaturePython)
  Dunit = g/cm3
  Dvalue = 0.0708
  Group = -> [H_element114]
  conduct = 2
  density = 1
  expand = 3
  formula = G4_lH2
  name = G4_lH2
  specific = 4
FEATURE [App::DocumentObjectGroupPython] N_element049  label="N_element : 022"  # scripted group (container) (typed FeaturePython)
  n = 2
  ref = N_element
FEATURE [App::DocumentObjectGroupPython] G4_lN2  # scripted group (container) (typed FeaturePython)
  Dunit = g/cm3
  Dvalue = 0.807
  Group = -> [N_element049]
  conduct = 2
  density = 1
  expand = 3
  formula = G4_lN2
  name = G4_lN2
  specific = 4
FEATURE [App::DocumentObjectGroupPython] O_element106  label="O_element : 060"  # scripted group (container) (typed FeaturePython)
  n = 2
  ref = O_element
FEATURE [App::DocumentObjectGroupPython] G4_lO2  # scripted group (container) (typed FeaturePython)
  Dunit = g/cm3
  Dvalue = 1.141
  Group = -> [O_element106]
  conduct = 2
  density = 1
  expand = 3
  formula = G4_lO2
  name = G4_lO2
  specific = 4
FEATURE [App::DocumentObjectGroupPython] Ar  label="Ar : 1"  # scripted group (container) (typed FeaturePython)
  n = 1
  ref = Ar
FEATURE [App::DocumentObjectGroupPython] G4_lAr  # scripted group (container) (typed FeaturePython)
  Dunit = g/cm3
  Dvalue = 1.396
  Group = -> [Ar]
  conduct = 2
  density = 1
  expand = 3
  formula = G4_lAr
  name = G4_lAr
  specific = 4
FEATURE [App::DocumentObjectGroupPython] Br  label="Br : 1"  # scripted group (container) (typed FeaturePython)
  n = 1
  ref = Br
FEATURE [App::DocumentObjectGroupPython] G4_lBr  # scripted group (container) (typed FeaturePython)
  Dunit = g/cm3
  Dvalue = 3.1028
  Group = -> [Br]
  conduct = 2
  density = 1
  expand = 3
  formula = G4_lBr
  name = G4_lBr
  specific = 4
FEATURE [App::DocumentObjectGroupPython] Kr  label="Kr : 1"  # scripted group (container) (typed FeaturePython)
  n = 1
  ref = Kr
FEATURE [App::DocumentObjectGroupPython] G4_lKr  # scripted group (container) (typed FeaturePython)
  Dunit = g/cm3
  Dvalue = 2.418
  Group = -> [Kr]
  conduct = 2
  density = 1
  expand = 3
  formula = G4_lKr
  name = G4_lKr
  specific = 4
FEATURE [App::DocumentObjectGroupPython] Xe  label="Xe : 1"  # scripted group (container) (typed FeaturePython)
  n = 1
  ref = Xe
FEATURE [App::DocumentObjectGroupPython] G4_lXe  # scripted group (container) (typed FeaturePython)
  Dunit = g/cm3
  Dvalue = 2.953
  Group = -> [Xe]
  conduct = 2
  density = 1
  expand = 3
  formula = G4_lXe
  name = G4_lXe
  specific = 4
FEATURE [App::DocumentObjectGroupPython] O_element107  label="O_element : 061"  # scripted group (container) (typed FeaturePython)
  n = 4
  ref = O_element
FEATURE [App::DocumentObjectGroupPython] Pb_element004  label="Pb_element : 002"  # scripted group (container) (typed FeaturePython)
  n = 1
  ref = Pb_element
FEATURE [App::DocumentObjectGroupPython] W_element005  label="W_element : 005"  # scripted group (container) (typed FeaturePython)
  n = 1
  ref = W_element
FEATURE [App::DocumentObjectGroupPython] G4_PbWO4  # scripted group (container) (typed FeaturePython)
  Dunit = g/cm3
  Dvalue = 8.28
  Group = -> [O_element107,Pb_element004,W_element005]
  conduct = 2
  density = 1
  expand = 3
  formula = G4_PbWO4
  name = G4_PbWO4
  specific = 4
FEATURE [App::DocumentObjectGroupPython] alactic  label="alactic : 1"  # scripted group (container) (typed FeaturePython)
  n = 1
  ref = alactic
FEATURE [App::DocumentObjectGroupPython] G4_Galactic  # scripted group (container) (typed FeaturePython)
  Dunit = g/cm3
  Dvalue = 0
  Group = -> [alactic]
  conduct = 2
  density = 1
  expand = 3
  formula = G4_Galactic
  name = G4_Galactic
  specific = 4
FEATURE [App::DocumentObjectGroupPython] RAPHITE_POROUS  label="RAPHITE_POROUS : 1"  # scripted group (container) (typed FeaturePython)
  n = 1
  ref = RAPHITE_POROUS
FEATURE [App::DocumentObjectGroupPython] G4_GRAPHITE_POROUS  # scripted group (container) (typed FeaturePython)
  Dunit = g/cm3
  Dvalue = 1.7
  Group = -> [RAPHITE_POROUS]
  conduct = 2
  density = 1
  expand = 3
  formula = G4_GRAPHITE_POROUS
  name = G4_GRAPHITE_POROUS
  specific = 4
FEATURE [App::DocumentObjectGroupPython] H_element115  label="H_element : 0.150"  # scripted group (container) (typed FeaturePython)
  n = 0.080538
FEATURE [App::DocumentObjectGroupPython] C_element125  label="C_element : 0.600"  # scripted group (container) (typed FeaturePython)
  n = 0.599848
FEATURE [App::DocumentObjectGroupPython] O_element108  label="O_element : 0.320"  # scripted group (container) (typed FeaturePython)
  n = 0.319614
FEATURE [App::DocumentObjectGroupPython] G4_LUCITE  # scripted group (container) (typed FeaturePython)
  Dunit = g/cm3
  Dvalue = 1.19
  Group = -> [H_element115,C_element125,O_element108]
  conduct = 2
  density = 1
  expand = 3
  formula = G4_LUCITE
  name = G4_LUCITE
  specific = 4
FEATURE [App::DocumentObjectGroupPython] Cu_element002  label="Cu_element : 62"  # scripted group (container) (typed FeaturePython)
  n = 62
  ref = Cu_element
FEATURE [App::DocumentObjectGroupPython] Zn_element002  label="Zn_element : 35"  # scripted group (container) (typed FeaturePython)
  n = 35
  ref = Zn_element
FEATURE [App::DocumentObjectGroupPython] Pb_element005  label="Pb_element : 3"  # scripted group (container) (typed FeaturePython)
  n = 3
  ref = Pb_element
FEATURE [App::DocumentObjectGroupPython] G4_BRASS  # scripted group (container) (typed FeaturePython)
  Dunit = g/cm3
  Dvalue = 8.52
  Group = -> [Cu_element002,Zn_element002,Pb_element005]
  conduct = 2
  density = 1
  expand = 3
  formula = G4_BRASS
  name = G4_BRASS
  specific = 4
FEATURE [App::DocumentObjectGroupPython] Cu_element003  label="Cu_element : 89"  # scripted group (container) (typed FeaturePython)
  n = 89
  ref = Cu_element
FEATURE [App::DocumentObjectGroupPython] Zn_element003  label="Zn_element : 9"  # scripted group (container) (typed FeaturePython)
  n = 9
  ref = Zn_element
FEATURE [App::DocumentObjectGroupPython] Pb_element006  label="Pb_element : 2"  # scripted group (container) (typed FeaturePython)
  n = 2
  ref = Pb_element
FEATURE [App::DocumentObjectGroupPython] G4_BRONZE  # scripted group (container) (typed FeaturePython)
  Dunit = g/cm3
  Dvalue = 8.82
  Group = -> [Cu_element003,Zn_element003,Pb_element006]
  conduct = 2
  density = 1
  expand = 3
  formula = G4_BRONZE
  name = G4_BRONZE
  specific = 4
FEATURE [App::DocumentObjectGroupPython] Fe_element008  label="Fe_element : 74"  # scripted group (container) (typed FeaturePython)
  n = 74
  ref = Fe_element
FEATURE [App::DocumentObjectGroupPython] Cr_element002  label="Cr_element : 18"  # scripted group (container) (typed FeaturePython)
  n = 18
  ref = Cr_element
FEATURE [App::DocumentObjectGroupPython] Ni_element002  label="Ni_element : 8"  # scripted group (container) (typed FeaturePython)
  n = 8
  ref = Ni_element
FEATURE [App::DocumentObjectGroupPython] G4_STAINLESS_STEEL  label="G4_STAINLESS-STEEL"  # scripted group (container) (typed FeaturePython)
  Dunit = g/cm3
  Dvalue = 8
  Group = -> [Fe_element008,Cr_element002,Ni_element002]
  conduct = 2
  density = 1
  expand = 3
  formula = G4_STAINLESS-STEEL
  name = G4_STAINLESS-STEEL
  specific = 4
FEATURE [App::DocumentObjectGroupPython] H_element116  label="H_element : 064"  # scripted group (container) (typed FeaturePython)
  n = 18
  ref = H_element
FEATURE [App::DocumentObjectGroupPython] C_element126  label="C_element : 071"  # scripted group (container) (typed FeaturePython)
  n = 12
  ref = C_element
FEATURE [App::DocumentObjectGroupPython] O_element109  label="O_element : 062"  # scripted group (container) (typed FeaturePython)
  n = 7
  ref = O_element
FEATURE [App::DocumentObjectGroupPython] G4_CR39  # scripted group (container) (typed FeaturePython)
  Dunit = g/cm3
  Dvalue = 1.32
  Group = -> [H_element116,C_element126,O_element109]
  conduct = 2
  density = 1
  expand = 3
  formula = G4_CR39
  name = G4_CR39
  specific = 4
FEATURE [App::DocumentObjectGroupPython] H_element117  label="H_element : 38"  # scripted group (container) (typed FeaturePython)
  n = 38
  ref = H_element
FEATURE [App::DocumentObjectGroupPython] C_element127  label="C_element : 072"  # scripted group (container) (typed FeaturePython)
  n = 18
  ref = C_element
FEATURE [App::DocumentObjectGroupPython] O_element110  label="O_element : 063"  # scripted group (container) (typed FeaturePython)
  n = 1
  ref = O_element
FEATURE [App::DocumentObjectGroupPython] G4_OCTADECANOL  # scripted group (container) (typed FeaturePython)
  Dunit = g/cm3
  Dvalue = 0.812
  Group = -> [H_element117,C_element127,O_element110]
  conduct = 2
  density = 1
  expand = 3
  formula = G4_OCTADECANOL
  name = G4_OCTADECANOL
  specific = 4
FEATURE [App::DocumentObjectGroupPython] HEP  # scripted group (container) (typed FeaturePython)
  Group = -> [G4_lH2,G4_lN2,G4_lO2,G4_lAr,G4_lBr,G4_lKr,G4_lXe,G4_PbWO4,G4_Galactic,G4_GRAPHITE_POROUS,G4_LUCITE,G4_BRASS,G4_BRONZE,G4_STAINLESS_STEEL,G4_CR39,G4_OCTADECANOL]
FEATURE [App::DocumentObjectGroupPython] C_element128  label="C_element : 073"  # scripted group (container) (typed FeaturePython)
  n = 14
  ref = C_element
FEATURE [App::DocumentObjectGroupPython] H_element118  label="H_element : 065"  # scripted group (container) (typed FeaturePython)
  n = 10
  ref = H_element
FEATURE [App::DocumentObjectGroupPython] O_element111  label="O_element : 064"  # scripted group (container) (typed FeaturePython)
  n = 2
  ref = O_element
FEATURE [App::DocumentObjectGroupPython] N_element050  label="N_element : 023"  # scripted group (container) (typed FeaturePython)
  n = 2
  ref = N_element
FEATURE [App::DocumentObjectGroupPython] G4_KEVLAR  # scripted group (container) (typed FeaturePython)
  Dunit = g/cm3
  Dvalue = 1.44
  Group = -> [C_element128,H_element118,O_element111,N_element050]
  conduct = 2
  density = 1
  expand = 3
  formula = G4_KEVLAR
  name = G4_KEVLAR
  specific = 4
FEATURE [App::DocumentObjectGroupPython] C_element129  label="C_element : 074"  # scripted group (container) (typed FeaturePython)
  n = 10
  ref = C_element
FEATURE [App::DocumentObjectGroupPython] H_element119  label="H_element : 066"  # scripted group (container) (typed FeaturePython)
  n = 8
  ref = H_element
FEATURE [App::DocumentObjectGroupPython] O_element112  label="O_element : 065"  # scripted group (container) (typed FeaturePython)
  n = 4
  ref = O_element
FEATURE [App::DocumentObjectGroupPython] G4_DACRON  # scripted group (container) (typed FeaturePython)
  Dunit = g/cm3
  Dvalue = 1.4
  Group = -> [C_element129,H_element119,O_element112]
  conduct = 2
  density = 1
  expand = 3
  formula = G4_DACRON
  name = G4_DACRON
  specific = 4
FEATURE [App::DocumentObjectGroupPython] C_element130  label="C_element : 075"  # scripted group (container) (typed FeaturePython)
  n = 4
  ref = C_element
FEATURE [App::DocumentObjectGroupPython] H_element120  label="H_element : 067"  # scripted group (container) (typed FeaturePython)
  n = 5
  ref = H_element
FEATURE [App::DocumentObjectGroupPython] Cl_element030  label="Cl_element : 016"  # scripted group (container) (typed FeaturePython)
  n = 1
  ref = Cl_element
FEATURE [App::DocumentObjectGroupPython] G4_NEOPRENE  # scripted group (container) (typed FeaturePython)
  Dunit = g/cm3
  Dvalue = 1.23
  Group = -> [C_element130,H_element120,Cl_element030]
  conduct = 2
  density = 1
  expand = 3
  formula = G4_NEOPRENE
  name = G4_NEOPRENE
  specific = 4
FEATURE [App::DocumentObjectGroupPython] Space  # scripted group (container) (typed FeaturePython)
  Group = -> [G4_KEVLAR,G4_DACRON,G4_NEOPRENE]
FEATURE [App::DocumentObjectGroupPython] H_element121  label="H_element : 068"  # scripted group (container) (typed FeaturePython)
  n = 5
  ref = H_element
FEATURE [App::DocumentObjectGroupPython] C_element131  label="C_element : 076"  # scripted group (container) (typed FeaturePython)
  n = 4
  ref = C_element
FEATURE [App::DocumentObjectGroupPython] N_element051  label="N_element : 3"  # scripted group (container) (typed FeaturePython)
  n = 3
  ref = N_element
FEATURE [App::DocumentObjectGroupPython] O_element113  label="O_element : 066"  # scripted group (container) (typed FeaturePython)
  n = 1
  ref = O_element
FEATURE [App::DocumentObjectGroupPython] G4_CYTOSINE  # scripted group (container) (typed FeaturePython)
  Dunit = g/cm3
  Dvalue = 1.55
  Group = -> [H_element121,C_element131,N_element051,O_element113]
  conduct = 2
  density = 1
  expand = 3
  formula = G4_CYTOSINE
  name = G4_CYTOSINE
  specific = 4
FEATURE [App::DocumentObjectGroupPython] H_element122  label="H_element : 069"  # scripted group (container) (typed FeaturePython)
  n = 6
  ref = H_element
FEATURE [App::DocumentObjectGroupPython] C_element132  label="C_element : 077"  # scripted group (container) (typed FeaturePython)
  n = 5
  ref = C_element
FEATURE [App::DocumentObjectGroupPython] N_element052  label="N_element : 024"  # scripted group (container) (typed FeaturePython)
  n = 2
  ref = N_element
FEATURE [App::DocumentObjectGroupPython] O_element114  label="O_element : 067"  # scripted group (container) (typed FeaturePython)
  n = 2
  ref = O_element
FEATURE [App::DocumentObjectGroupPython] G4_THYMINE  # scripted group (container) (typed FeaturePython)
  Dunit = g/cm3
  Dvalue = 1.23
  Group = -> [H_element122,C_element132,N_element052,O_element114]
  conduct = 2
  density = 1
  expand = 3
  formula = G4_THYMINE
  name = G4_THYMINE
  specific = 4
FEATURE [App::DocumentObjectGroupPython] H_element123  label="H_element : 070"  # scripted group (container) (typed FeaturePython)
  n = 4
  ref = H_element
FEATURE [App::DocumentObjectGroupPython] C_element133  label="C_element : 078"  # scripted group (container) (typed FeaturePython)
  n = 4
  ref = C_element
FEATURE [App::DocumentObjectGroupPython] N_element053  label="N_element : 025"  # scripted group (container) (typed FeaturePython)
  n = 2
  ref = N_element
FEATURE [App::DocumentObjectGroupPython] O_element115  label="O_element : 068"  # scripted group (container) (typed FeaturePython)
  n = 2
  ref = O_element
FEATURE [App::DocumentObjectGroupPython] G4_URACIL  # scripted group (container) (typed FeaturePython)
  Dunit = g/cm3
  Dvalue = 1.32
  Group = -> [H_element123,C_element133,N_element053,O_element115]
  conduct = 2
  density = 1
  expand = 3
  formula = G4_URACIL
  name = G4_URACIL
  specific = 4
FEATURE [App::DocumentObjectGroupPython] H_element124  label="H_element : 071"  # scripted group (container) (typed FeaturePython)
  n = 4
  ref = H_element
FEATURE [App::DocumentObjectGroupPython] C_element134  label="C_element : 079"  # scripted group (container) (typed FeaturePython)
  n = 5
  ref = C_element
FEATURE [App::DocumentObjectGroupPython] N_element054  label="N_element : 026"  # scripted group (container) (typed FeaturePython)
  n = 5
  ref = N_element
FEATURE [App::DocumentObjectGroupPython] G4_DNA_ADENINE  # scripted group (container) (typed FeaturePython)
  Dunit = g/cm3
  Dvalue = 1
  Group = -> [H_element124,C_element134,N_element054]
  conduct = 2
  density = 1
  expand = 3
  formula = G4_DNA_ADENINE
  name = G4_DNA_ADENINE
  specific = 4
FEATURE [App::DocumentObjectGroupPython] H_element125  label="H_element : 072"  # scripted group (container) (typed FeaturePython)
  n = 4
  ref = H_element
FEATURE [App::DocumentObjectGroupPython] C_element135  label="C_element : 080"  # scripted group (container) (typed FeaturePython)
  n = 5
  ref = C_element
FEATURE [App::DocumentObjectGroupPython] N_element055  label="N_element : 027"  # scripted group (container) (typed FeaturePython)
  n = 5
  ref = N_element
FEATURE [App::DocumentObjectGroupPython] O_element116  label="O_element : 069"  # scripted group (container) (typed FeaturePython)
  n = 1
  ref = O_element
FEATURE [App::DocumentObjectGroupPython] G4_DNA_GUANINE  # scripted group (container) (typed FeaturePython)
  Dunit = g/cm3
  Dvalue = 1
  Group = -> [H_element125,C_element135,N_element055,O_element116]
  conduct = 2
  density = 1
  expand = 3
  formula = G4_DNA_GUANINE
  name = G4_DNA_GUANINE
  specific = 4
FEATURE [App::DocumentObjectGroupPython] H_element126  label="H_element : 073"  # scripted group (container) (typed FeaturePython)
  n = 4
  ref = H_element
FEATURE [App::DocumentObjectGroupPython] C_element136  label="C_element : 081"  # scripted group (container) (typed FeaturePython)
  n = 4
  ref = C_element
FEATURE [App::DocumentObjectGroupPython] N_element056  label="N_element : 028"  # scripted group (container) (typed FeaturePython)
  n = 3
  ref = N_element
FEATURE [App::DocumentObjectGroupPython] O_element117  label="O_element : 070"  # scripted group (container) (typed FeaturePython)
  n = 1
  ref = O_element
FEATURE [App::DocumentObjectGroupPython] G4_DNA_CYTOSINE  # scripted group (container) (typed FeaturePython)
  Dunit = g/cm3
  Dvalue = 1
  Group = -> [H_element126,C_element136,N_element056,O_element117]
  conduct = 2
  density = 1
  expand = 3
  formula = G4_DNA_CYTOSINE
  name = G4_DNA_CYTOSINE
  specific = 4
FEATURE [App::DocumentObjectGroupPython] H_element127  label="H_element : 074"  # scripted group (container) (typed FeaturePython)
  n = 5
  ref = H_element
FEATURE [App::DocumentObjectGroupPython] C_element137  label="C_element : 082"  # scripted group (container) (typed FeaturePython)
  n = 5
  ref = C_element
FEATURE [App::DocumentObjectGroupPython] N_element057  label="N_element : 029"  # scripted group (container) (typed FeaturePython)
  n = 2
  ref = N_element
FEATURE [App::DocumentObjectGroupPython] O_element118  label="O_element : 071"  # scripted group (container) (typed FeaturePython)
  n = 2
  ref = O_element
FEATURE [App::DocumentObjectGroupPython] G4_DNA_THYMINE  # scripted group (container) (typed FeaturePython)
  Dunit = g/cm3
  Dvalue = 1
  Group = -> [H_element127,C_element137,N_element057,O_element118]
  conduct = 2
  density = 1
  expand = 3
  formula = G4_DNA_THYMINE
  name = G4_DNA_THYMINE
  specific = 4
FEATURE [App::DocumentObjectGroupPython] H_element128  label="H_element : 075"  # scripted group (container) (typed FeaturePython)
  n = 3
  ref = H_element
FEATURE [App::DocumentObjectGroupPython] C_element138  label="C_element : 083"  # scripted group (container) (typed FeaturePython)
  n = 4
  ref = C_element
FEATURE [App::DocumentObjectGroupPython] N_element058  label="N_element : 030"  # scripted group (container) (typed FeaturePython)
  n = 2
  ref = N_element
FEATURE [App::DocumentObjectGroupPython] O_element119  label="O_element : 072"  # scripted group (container) (typed FeaturePython)
  n = 2
  ref = O_element
FEATURE [App::DocumentObjectGroupPython] G4_DNA_URACIL  # scripted group (container) (typed FeaturePython)
  Dunit = g/cm3
  Dvalue = 1
  Group = -> [H_element128,C_element138,N_element058,O_element119]
  conduct = 2
  density = 1
  expand = 3
  formula = G4_DNA_URACIL
  name = G4_DNA_URACIL
  specific = 4
FEATURE [App::DocumentObjectGroupPython] H_element129  label="H_element : 076"  # scripted group (container) (typed FeaturePython)
  n = 10
  ref = H_element
FEATURE [App::DocumentObjectGroupPython] C_element139  label="C_element : 084"  # scripted group (container) (typed FeaturePython)
  n = 10
  ref = C_element
FEATURE [App::DocumentObjectGroupPython] N_element059  label="N_element : 031"  # scripted group (container) (typed FeaturePython)
  n = 5
  ref = N_element
FEATURE [App::DocumentObjectGroupPython] O_element120  label="O_element : 073"  # scripted group (container) (typed FeaturePython)
  n = 4
  ref = O_element
FEATURE [App::DocumentObjectGroupPython] G4_DNA_ADENOSINE  # scripted group (container) (typed FeaturePython)
  Dunit = g/cm3
  Dvalue = 1
  Group = -> [H_element129,C_element139,N_element059,O_element120]
  conduct = 2
  density = 1
  expand = 3
  formula = G4_DNA_ADENOSINE
  name = G4_DNA_ADENOSINE
  specific = 4
FEATURE [App::DocumentObjectGroupPython] H_element130  label="H_element : 077"  # scripted group (container) (typed FeaturePython)
  n = 10
  ref = H_element
FEATURE [App::DocumentObjectGroupPython] C_element140  label="C_element : 085"  # scripted group (container) (typed FeaturePython)
  n = 10
  ref = C_element
FEATURE [App::DocumentObjectGroupPython] N_element060  label="N_element : 032"  # scripted group (container) (typed FeaturePython)
  n = 5
  ref = N_element
FEATURE [App::DocumentObjectGroupPython] O_element121  label="O_element : 074"  # scripted group (container) (typed FeaturePython)
  n = 5
  ref = O_element
FEATURE [App::DocumentObjectGroupPython] G4_DNA_GUANOSINE  # scripted group (container) (typed FeaturePython)
  Dunit = g/cm3
  Dvalue = 1
  Group = -> [H_element130,C_element140,N_element060,O_element121]
  conduct = 2
  density = 1
  expand = 3
  formula = G4_DNA_GUANOSINE
  name = G4_DNA_GUANOSINE
  specific = 4
FEATURE [App::DocumentObjectGroupPython] H_element131  label="H_element : 078"  # scripted group (container) (typed FeaturePython)
  n = 10
  ref = H_element
FEATURE [App::DocumentObjectGroupPython] C_element141  label="C_element : 086"  # scripted group (container) (typed FeaturePython)
  n = 9
  ref = C_element
FEATURE [App::DocumentObjectGroupPython] N_element061  label="N_element : 033"  # scripted group (container) (typed FeaturePython)
  n = 3
  ref = N_element
FEATURE [App::DocumentObjectGroupPython] O_element122  label="O_element : 075"  # scripted group (container) (typed FeaturePython)
  n = 5
  ref = O_element
FEATURE [App::DocumentObjectGroupPython] G4_DNA_CYTIDINE  # scripted group (container) (typed FeaturePython)
  Dunit = g/cm3
  Dvalue = 1
  Group = -> [H_element131,C_element141,N_element061,O_element122]
  conduct = 2
  density = 1
  expand = 3
  formula = G4_DNA_CYTIDINE
  name = G4_DNA_CYTIDINE
  specific = 4
FEATURE [App::DocumentObjectGroupPython] H_element132  label="H_element : 079"  # scripted group (container) (typed FeaturePython)
  n = 9
  ref = H_element
FEATURE [App::DocumentObjectGroupPython] C_element142  label="C_element : 087"  # scripted group (container) (typed FeaturePython)
  n = 9
  ref = C_element
FEATURE [App::DocumentObjectGroupPython] N_element062  label="N_element : 034"  # scripted group (container) (typed FeaturePython)
  n = 2
  ref = N_element
FEATURE [App::DocumentObjectGroupPython] O_element123  label="O_element : 076"  # scripted group (container) (typed FeaturePython)
  n = 6
  ref = O_element
FEATURE [App::DocumentObjectGroupPython] G4_DNA_URIDINE  # scripted group (container) (typed FeaturePython)
  Dunit = g/cm3
  Dvalue = 1
  Group = -> [H_element132,C_element142,N_element062,O_element123]
  conduct = 2
  density = 1
  expand = 3
  formula = G4_DNA_URIDINE
  name = G4_DNA_URIDINE
  specific = 4
FEATURE [App::DocumentObjectGroupPython] H_element133  label="H_element : 080"  # scripted group (container) (typed FeaturePython)
  n = 11
  ref = H_element
FEATURE [App::DocumentObjectGroupPython] C_element143  label="C_element : 088"  # scripted group (container) (typed FeaturePython)
  n = 10
  ref = C_element
FEATURE [App::DocumentObjectGroupPython] N_element063  label="N_element : 035"  # scripted group (container) (typed FeaturePython)
  n = 2
  ref = N_element
FEATURE [App::DocumentObjectGroupPython] O_element124  label="O_element : 077"  # scripted group (container) (typed FeaturePython)
  n = 6
  ref = O_element
FEATURE [App::DocumentObjectGroupPython] G4_DNA_METHYLURIDINE  # scripted group (container) (typed FeaturePython)
  Dunit = g/cm3
  Dvalue = 1
  Group = -> [H_element133,C_element143,N_element063,O_element124]
  conduct = 2
  density = 1
  expand = 3
  formula = G4_DNA_METHYLURIDINE
  name = G4_DNA_METHYLURIDINE
  specific = 4
FEATURE [App::DocumentObjectGroupPython] P_element014  label="P_element : 003"  # scripted group (container) (typed FeaturePython)
  n = 1
  ref = P_element
FEATURE [App::DocumentObjectGroupPython] O_element125  label="O_element : 078"  # scripted group (container) (typed FeaturePython)
  n = 3
  ref = O_element
FEATURE [App::DocumentObjectGroupPython] G4_DNA_MONOPHOSPHATE  # scripted group (container) (typed FeaturePython)
  Dunit = g/cm3
  Dvalue = 1
  Group = -> [P_element014,O_element125]
  conduct = 2
  density = 1
  expand = 3
  formula = G4_DNA_MONOPHOSPHATE
  name = G4_DNA_MONOPHOSPHATE
  specific = 4
FEATURE [App::DocumentObjectGroupPython] H_element134  label="H_element : 081"  # scripted group (container) (typed FeaturePython)
  n = 10
  ref = H_element
FEATURE [App::DocumentObjectGroupPython] C_element144  label="C_element : 089"  # scripted group (container) (typed FeaturePython)
  n = 10
  ref = C_element
FEATURE [App::DocumentObjectGroupPython] N_element064  label="N_element : 036"  # scripted group (container) (typed FeaturePython)
  n = 5
  ref = N_element
FEATURE [App::DocumentObjectGroupPython] O_element126  label="O_element : 079"  # scripted group (container) (typed FeaturePython)
  n = 7
  ref = O_element
FEATURE [App::DocumentObjectGroupPython] P_element015  label="P_element : 004"  # scripted group (container) (typed FeaturePython)
  n = 1
  ref = P_element
FEATURE [App::DocumentObjectGroupPython] G4_DNA_A  # scripted group (container) (typed FeaturePython)
  Dunit = g/cm3
  Dvalue = 1
  Group = -> [H_element134,C_element144,N_element064,O_element126,P_element015]
  conduct = 2
  density = 1
  expand = 3
  formula = G4_DNA_A
  name = G4_DNA_A
  specific = 4
FEATURE [App::DocumentObjectGroupPython] H_element135  label="H_element : 082"  # scripted group (container) (typed FeaturePython)
  n = 10
  ref = H_element
FEATURE [App::DocumentObjectGroupPython] C_element145  label="C_element : 090"  # scripted group (container) (typed FeaturePython)
  n = 10
  ref = C_element
FEATURE [App::DocumentObjectGroupPython] N_element065  label="N_element : 037"  # scripted group (container) (typed FeaturePython)
  n = 5
  ref = N_element
FEATURE [App::DocumentObjectGroupPython] O_element127  label="O_element : 8"  # scripted group (container) (typed FeaturePython)
  n = 8
  ref = O_element
FEATURE [App::DocumentObjectGroupPython] P_element016  label="P_element : 005"  # scripted group (container) (typed FeaturePython)
  n = 1
  ref = P_element
FEATURE [App::DocumentObjectGroupPython] G4_DNA_G  # scripted group (container) (typed FeaturePython)
  Dunit = g/cm3
  Dvalue = 1
  Group = -> [H_element135,C_element145,N_element065,O_element127,P_element016]
  conduct = 2
  density = 1
  expand = 3
  formula = G4_DNA_G
  name = G4_DNA_G
  specific = 4
FEATURE [App::DocumentObjectGroupPython] H_element136  label="H_element : 083"  # scripted group (container) (typed FeaturePython)
  n = 10
  ref = H_element
FEATURE [App::DocumentObjectGroupPython] C_element146  label="C_element : 091"  # scripted group (container) (typed FeaturePython)
  n = 9
  ref = C_element
FEATURE [App::DocumentObjectGroupPython] N_element066  label="N_element : 038"  # scripted group (container) (typed FeaturePython)
  n = 3
  ref = N_element
FEATURE [App::DocumentObjectGroupPython] O_element128  label="O_element : 080"  # scripted group (container) (typed FeaturePython)
  n = 8
  ref = O_element
FEATURE [App::DocumentObjectGroupPython] P_element017  label="P_element : 006"  # scripted group (container) (typed FeaturePython)
  n = 1
  ref = P_element
FEATURE [App::DocumentObjectGroupPython] G4_DNA_C  # scripted group (container) (typed FeaturePython)
  Dunit = g/cm3
  Dvalue = 1
  Group = -> [H_element136,C_element146,N_element066,O_element128,P_element017]
  conduct = 2
  density = 1
  expand = 3
  formula = G4_DNA_C
  name = G4_DNA_C
  specific = 4
FEATURE [App::DocumentObjectGroupPython] H_element137  label="H_element : 084"  # scripted group (container) (typed FeaturePython)
  n = 9
  ref = H_element
FEATURE [App::DocumentObjectGroupPython] C_element147  label="C_element : 092"  # scripted group (container) (typed FeaturePython)
  n = 9
  ref = C_element
FEATURE [App::DocumentObjectGroupPython] N_element067  label="N_element : 039"  # scripted group (container) (typed FeaturePython)
  n = 2
  ref = N_element
FEATURE [App::DocumentObjectGroupPython] O_element129  label="O_element : 9"  # scripted group (container) (typed FeaturePython)
  n = 9
  ref = O_element
FEATURE [App::DocumentObjectGroupPython] P_element018  label="P_element : 007"  # scripted group (container) (typed FeaturePython)
  n = 1
  ref = P_element
FEATURE [App::DocumentObjectGroupPython] G4_DNA_U  # scripted group (container) (typed FeaturePython)
  Dunit = g/cm3
  Dvalue = 1
  Group = -> [H_element137,C_element147,N_element067,O_element129,P_element018]
  conduct = 2
  density = 1
  expand = 3
  formula = G4_DNA_U
  name = G4_DNA_U
  specific = 4
FEATURE [App::DocumentObjectGroupPython] H_element138  label="H_element : 085"  # scripted group (container) (typed FeaturePython)
  n = 11
  ref = H_element
FEATURE [App::DocumentObjectGroupPython] C_element148  label="C_element : 093"  # scripted group (container) (typed FeaturePython)
  n = 10
  ref = C_element
FEATURE [App::DocumentObjectGroupPython] N_element068  label="N_element : 040"  # scripted group (container) (typed FeaturePython)
  n = 2
  ref = N_element
FEATURE [App::DocumentObjectGroupPython] O_element130  label="O_element : 081"  # scripted group (container) (typed FeaturePython)
  n = 9
  ref = O_element
FEATURE [App::DocumentObjectGroupPython] P_element019  label="P_element : 008"  # scripted group (container) (typed FeaturePython)
  n = 1
  ref = P_element
FEATURE [App::DocumentObjectGroupPython] G4_DNA_MU  # scripted group (container) (typed FeaturePython)
  Dunit = g/cm3
  Dvalue = 1
  Group = -> [H_element138,C_element148,N_element068,O_element130,P_element019]
  conduct = 2
  density = 1
  expand = 3
  formula = G4_DNA_MU
  name = G4_DNA_MU
  specific = 4
FEATURE [App::DocumentObjectGroupPython] BioChemical  # scripted group (container) (typed FeaturePython)
  Group = -> [G4_CYTOSINE,G4_THYMINE,G4_URACIL,G4_DNA_ADENINE,G4_DNA_GUANINE,G4_DNA_CYTOSINE,G4_DNA_THYMINE,G4_DNA_URACIL,G4_DNA_ADENOSINE,G4_DNA_GUANOSINE,G4_DNA_CYTIDINE,G4_DNA_URIDINE,G4_DNA_METHYLURIDINE,G4_DNA_MONOPHOSPHATE,G4_DNA_A,G4_DNA_G,G4_DNA_C,G4_DNA_U,G4_DNA_MU]
FEATURE [App::DocumentObjectGroupPython] G4Materials  # scripted group (container) (typed FeaturePython)
  Group = -> [NIST,Element,HEP,Space,BioChemical]
  version = 1
FEATURE [App::DocumentObjectGroupPython] Geant4  # scripted group (container) (typed FeaturePython)
  Group = -> [G4Isotopes,G4Elements,G4Materials]
FEATURE [App::DocumentObjectGroupPython] Materials  # scripted group (container) (typed FeaturePython)
  Group = -> [Geant4]
FEATURE [Part::FeaturePython] GDMLBox_WorldBox  # WARN: FeaturePython — macro-defined, semantics opaque (R4)
  lunit = 2
  material = 5
  x = 200
  y = 200
  z = 200
FEATURE [Sketcher::SketchObject] Sketch
  FullyConstrained = false
  sketch-geometry (36):
    g0: ArcOfParabola CenterX=18.1274 CenterY=-16.2535 CenterZ=0 NormalX=0 NormalY=0 NormalZ=1 Focal=8.09223 AngleXU=-3.10749 StartAngle=-21.4534 EndAngle=19.9625
    g1: GeomPoint X=10.0399 Y=-16.5294 Z=0
    g2: LineSegment StartX=18.1274 StartY=-16.2535 StartZ=0 EndX=10.0399 EndY=-16.5294 EndZ=0
    g3: ArcOfCircle CenterX=-6.88152 CenterY=-4.99689 CenterZ=0 NormalX=0 NormalY=0 NormalZ=1 AngleXU=0 Radius=13.9794 StartAngle=2.38084 EndAngle=7.05
    g4: ArcOfEllipse CenterX=-7.78764 CenterY=-33.8957 CenterZ=0 NormalX=0 NormalY=0 NormalZ=1 MajorRadius=18.086 MinorRadius=7.91522 AngleXU=-0.556234 StartAngle=4.96298 EndAngle=7.00481
    g5: LineSegment StartX=7.57186 StartY=-43.4449 StartZ=0 EndX=-23.1471 EndY=-24.3464 EndZ=0
    g6: LineSegment StartX=-3.60847 StartY=-27.1737 StartZ=0 EndX=-11.9668 EndY=-40.6177 EndZ=0
    g7: GeomPoint X=6.02282 Y=-42.4819 Z=0
    g8: GeomPoint X=-21.5981 Y=-25.3095 Z=0
    g9-g16: Circle x8 (B-spline internal-alignment scaffolding for g17; pole/knot coordinates omitted)
    g17: BSplineCurve PolesCount=8 KnotsCount=6 Degree=3 IsPeriodic=0
    g18-g23: GeomPoint x6 (B-spline internal-alignment scaffolding for g17; pole/knot coordinates omitted)
    g24: LineSegment StartX=-41.714 StartY=-18.5032 StartZ=0 EndX=-43.2734 EndY=-9.67993 EndZ=0
    g25: LineSegment StartX=-35.6082 StartY=7.90793 StartZ=0 EndX=-17.007 EndY=4.64145 EndZ=0
    g26: Circle CenterX=-9.18911 CenterY=-31.0442 CenterZ=0 NormalX=0 NormalY=0 NormalZ=1 AngleXU=0 Radius=8.40034
    g27: ArcOfHyperbola CenterX=-68.367 CenterY=18.2732 CenterZ=0 NormalX=0 NormalY=0 NormalZ=1 MajorRadius=22.1156 MinorRadius=7.852 AngleXU=-0.565391 StartAngle=-1.07469 EndAngle=0.964065
    g28: LineSegment StartX=-49.6931 StartY=6.4249 StartZ=0 EndX=-87.0409 EndY=30.1216 EndZ=0
    g29: LineSegment StartX=-45.4864 StartY=13.055 StartZ=0 EndX=-53.8998 EndY=-0.205161 EndZ=0
    g30: GeomPoint X=-48.551 Y=5.70028 Z=0
    g31: Ellipse CenterX=-34.2322 CenterY=-6.26645 CenterZ=0 NormalX=0 NormalY=0 NormalZ=1 MajorRadius=7.12528 MinorRadius=4.84017 AngleXU=-0.84953
    g32: LineSegment StartX=-29.5272 StartY=-11.6173 StartZ=0 EndX=-38.9373 EndY=-0.915575 EndZ=0
    g33: LineSegment StartX=-30.5974 StartY=-3.07031 StartZ=0 EndX=-37.8671 EndY=-9.46258 EndZ=0
    g34: GeomPoint X=-30.7794 Y=-10.1933 Z=0
    g35: GeomPoint X=-37.6851 Y=-2.33963 Z=0
  constraints (18):
    c: InternalAlignment(g1,g0)
    c: InternalAlignment(g2,g0)
    c: Coincident(g3,g0)
    c: InternalAlignment(g5-g8 -> g4) x4
    c: Coincident(g4,g0)
    c: Coincident(g17,g4)
    c: Weight(g9) = 1
    c: Equal(g9, g10-g16) x7
    c: InternalAlignment(g9-g16 -> g17) x8
    c: InternalAlignment(g18-g23 -> g17) x6
    c: Coincident(g24,g17)
    c: Coincident(g25,g3)
    c: InternalAlignment(g28,g27)
    c: InternalAlignment(g29,g27)
    c: InternalAlignment(g30,g27)
    c: Coincident(g24,g27)
    c: Coincident(g25,g27)
    c: InternalAlignment(g32-g35 -> g31) x4
FEATURE [Part::Extrusion] Extrude
  Base = -> Sketch
  Dir = (0,0,1)
  DirMode = 2
  FaceMakerClass = Part::FaceMakerBullseye
  LengthFwd = 10
  LengthRev = 0
  Solid = true
  Symmetric = false
FEATURE [App::Part] Part
  Group = -> [Sketch,Extrude]
  Origin = -> Origin001
  material = 5
FEATURE [App::Part] worldVOL
  Group = -> [GDMLBox_WorldBox,Part]
  Origin = -> Origin
